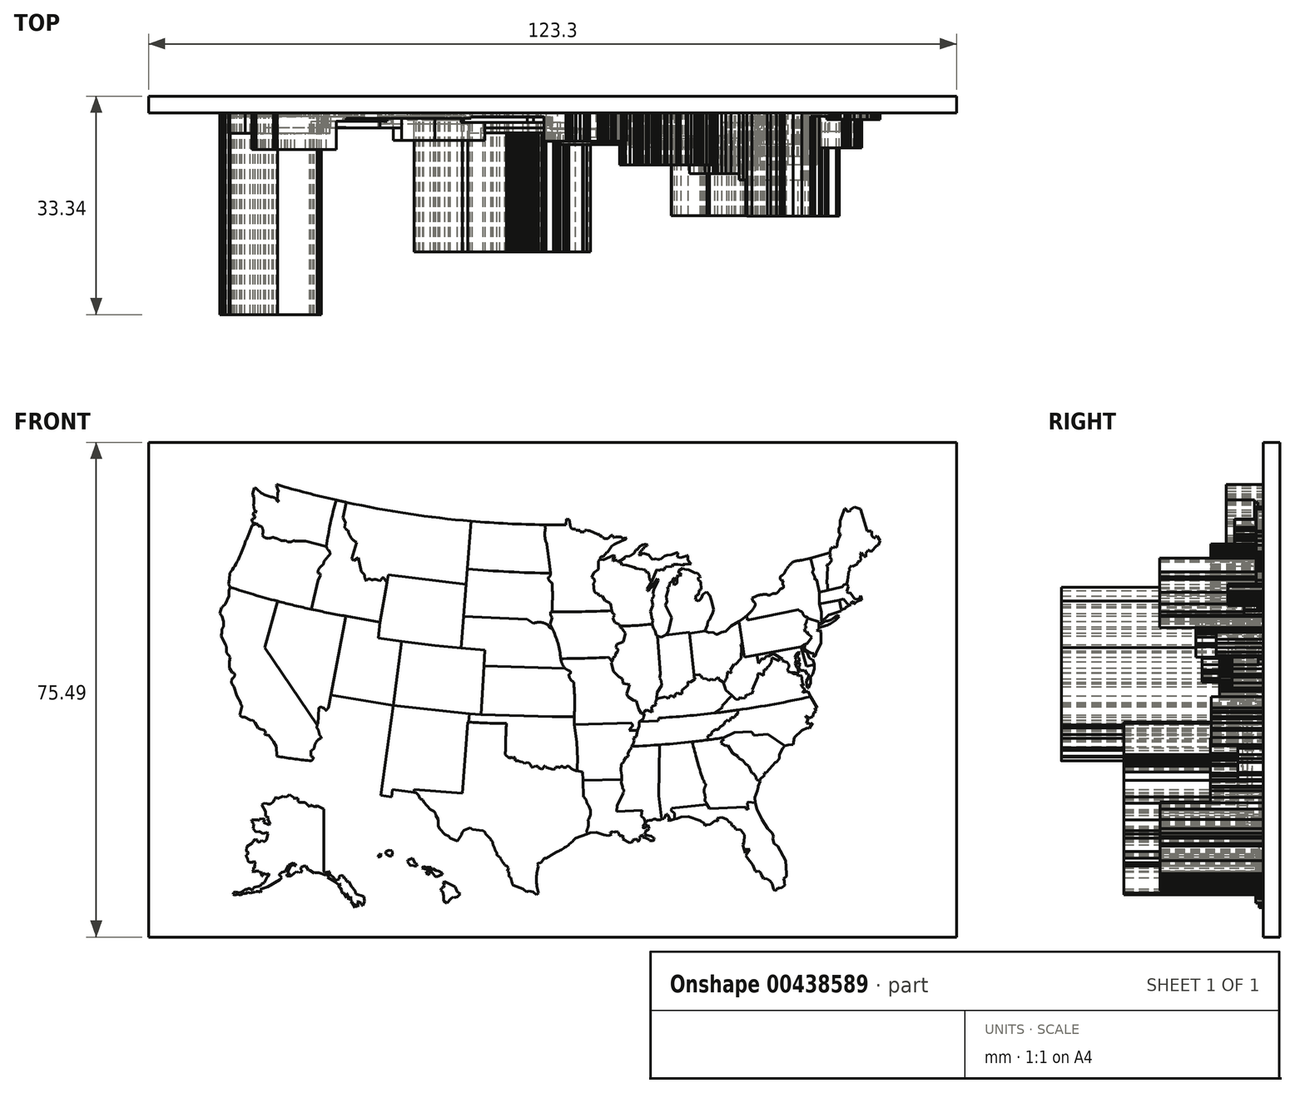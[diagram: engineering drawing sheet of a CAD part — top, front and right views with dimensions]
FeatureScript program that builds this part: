
annotation { "Feature Type Name" : "Feature", "Feature Type Description" : "" }
export const myFeature = defineFeature(function(context is Context, id is Id, definition is map)
    precondition{}
    {
        {
            var Q0;
            Q0=qCreatedBy(makeId("Front.planeOp"),FACE);
            var sketch = newSketch(context, id + "F0", { "sketchPlane" : qUnion([Q0])});
            skLineSegment(sketch, "E0.bottom", {"start": v(-61.56, 41.77) * mm, "end": v(61.74, 41.77) * mm});
            skLineSegment(sketch, "E0.top", {"start": v(-61.56, -33.72) * mm, "end": v(61.74, -33.72) * mm});
            skLineSegment(sketch, "E0.left", {"start": v(-61.56, 41.77) * mm, "end": v(-61.56, -33.72) * mm});
            skLineSegment(sketch, "E0.right", {"start": v(61.74, 41.77) * mm, "end": v(61.74, -33.72) * mm});
            skSolve(sketch);
        }
        {
            var Q0;
            Q0 = qSketchRegion(id + "F0", true);
            extrude(context, id + "F1", {"entities" : qUnion([Q0]), "depth" : 2.54 * mm, "offsetDistance" : 25.4 * mm});
        }
        {
            var Q0;
            Q0=makeQuery(id+"F1.opExtrude","CAP_FACE",FACE,{"disambiguationData":[OSD([sQuery(id+"F0.wireOp",EDGE,"E0.bottom"),sQuery(id+"F0.wireOp",EDGE,"E0.top"),sQuery(id+"F0.wireOp",EDGE,"E0.left"),sQuery(id+"F0.wireOp",EDGE,"E0.right")])],"isStart":false});
            var sketch = newSketch(context, id + "F2", { "sketchPlane" : qUnion([Q0])});
            skLineSegment(sketch, "E1", {"start": v(-6.58, -23.8) * mm, "end": v(-6.79, -23.67) * mm});
            skLineSegment(sketch, "E2", {"start": v(-6.79, -23.67) * mm, "end": v(-6.62, -23.2) * mm});
            skLineSegment(sketch, "E3", {"start": v(-6.86, -22.87) * mm, "end": v(-6.62, -23.2) * mm});
            skLineSegment(sketch, "E4", {"start": v(-6.86, -22.87) * mm, "end": v(-7.18, -22.74) * mm});
            skArc(sketch, "E5", {"start": v(-7.96, -21.52) * mm, "mid": v(-7.6, -22.15) * mm, "end": v(-7.18, -22.74) * mm});
            skArc(sketch, "E6", {"start": v(-8.39, -21.24) * mm, "mid": v(-8.17, -21.38) * mm, "end": v(-7.96, -21.52) * mm});
            skArc(sketch, "E7", {"start": v(-8.39, -20.98) * mm, "mid": v(-8.39, -21.1) * mm, "end": v(-8.39, -21.24) * mm});
            skArc(sketch, "E8", {"start": v(-8.98, -19.66) * mm, "mid": v(-8.7, -20.33) * mm, "end": v(-8.39, -20.98) * mm});
            skArc(sketch, "E9", {"start": v(-9.07, -19.19) * mm, "mid": v(-9.17, -19.07) * mm, "end": v(-9.29, -18.98) * mm});
            skArc(sketch, "E10", {"start": v(-9.07, -19.19) * mm, "mid": v(-9.03, -19.42) * mm, "end": v(-8.98, -19.66) * mm});
            skLineSegment(sketch, "E11", {"start": v(-22.96, 11.38) * mm, "end": v(-24.2, 1.61) * mm});
            skLineSegment(sketch, "E12", {"start": v(-10.22, 10.07) * mm, "end": v(-10.37, 7.64) * mm});
            skLineSegment(sketch, "E13", {"start": v(-31.44, 15.25) * mm, "end": v(-26.22, 14.33) * mm});
            skLineSegment(sketch, "E14", {"start": v(-26.22, 14.33) * mm, "end": v(-26.5, 11.9) * mm});
            skLineSegment(sketch, "E15", {"start": v(-26.5, 11.9) * mm, "end": v(-22.96, 11.38) * mm});
            skLineSegment(sketch, "E16", {"start": v(-33.75, 3.22) * mm, "end": v(-31.44, 15.25) * mm});
            skArc(sketch, "E17", {"start": v(-49.13, 19.66) * mm, "mid": v(-40.36, 17.15) * mm, "end": v(-31.44, 15.25) * mm});
            skLineSegment(sketch, "E18", {"start": v(-43.82, 10.48) * mm, "end": v(-41.9, 17.54) * mm});
            skLineSegment(sketch, "E19", {"start": v(-43.82, 10.48) * mm, "end": v(-35.84, -1.39) * mm});
            skLineSegment(sketch, "E20", {"start": v(-26.22, 14.33) * mm, "end": v(-24.95, 21.56) * mm});
            skLineSegment(sketch, "E21", {"start": v(-13.08, 20.1) * mm, "end": v(-24.95, 21.56) * mm});
            skLineSegment(sketch, "E22", {"start": v(-13.67, -11.77) * mm, "end": v(-12.83, -0.9) * mm});
            skLineSegment(sketch, "E23", {"start": v(-12.83, -0.9) * mm, "end": v(-12.71, -0.9) * mm});
            skLineSegment(sketch, "E24", {"start": v(-12.71, -0.9) * mm, "end": v(-12.62, 0.37) * mm});
            skLineSegment(sketch, "E25", {"start": v(-26.15, -12.1) * mm, "end": v(-24.45, -12.34) * mm});
            skLineSegment(sketch, "E26", {"start": v(-24.45, -12.34) * mm, "end": v(-24.33, -11.2) * mm});
            skLineSegment(sketch, "E27", {"start": v(-24.33, -11.2) * mm, "end": v(-21.02, -11.66) * mm});
            skLineSegment(sketch, "E28", {"start": v(-21.02, -11.66) * mm, "end": v(-21.02, -11.2) * mm});
            skLineSegment(sketch, "E29", {"start": v(-21.02, -11.2) * mm, "end": v(-13.67, -11.77) * mm});
            skLineSegment(sketch, "E30", {"start": v(-37.29, -7.31) * mm, "end": v(-30.35, -11.42) * mm});
            skLineSegment(sketch, "E31", {"start": v(-30.35, -11.42) * mm, "end": v(-26.15, -12.1) * mm});
            skArc(sketch, "E32", {"start": v(-12.71, -0.9) * mm, "mid": v(-9.83, -1.07) * mm, "end": v(-6.95, -1.13) * mm});
            skArc(sketch, "E33", {"start": v(-6.95, -1.13) * mm, "mid": v(-7.05, -3.5) * mm, "end": v(-7.1, -5.86) * mm});
            skArc(sketch, "E34", {"start": v(-41.92, 35.31) * mm, "mid": v(-20.1, 30.62) * mm, "end": v(2.16, 29.2) * mm});
            skLineSegment(sketch, "E35", {"start": v(-13.08, 20.1) * mm, "end": v(-12.32, 29.75) * mm});
            skLineSegment(sketch, "E36", {"start": v(-13.46, 15.24) * mm, "end": v(-3.77, 14.75) * mm});
            skLineSegment(sketch, "E37", {"start": v(-10.37, 7.64) * mm, "end": v(2.04, 7.28) * mm});
            skArc(sketch, "E38", {"start": v(-0.2, 15.89) * mm, "mid": v(4.47, 15.94) * mm, "end": v(9.13, 16.1) * mm});
            skArc(sketch, "E39", {"start": v(1.33, 8.76) * mm, "mid": v(4.97, 8.83) * mm, "end": v(8.6, 8.97) * mm});
            skArc(sketch, "E40", {"start": v(10.38, 13.78) * mm, "mid": v(12.85, 13.82) * mm, "end": v(15.3, 14.07) * mm});
            skLineSegment(sketch, "E41", {"start": v(17.33, 12.38) * mm, "end": v(20.97, 12.8) * mm});
            skLineSegment(sketch, "E42", {"start": v(20.97, 12.8) * mm, "end": v(21.7, 6.25) * mm});
            skLineSegment(sketch, "E43", {"start": v(21, 12.63) * mm, "end": v(23.37, 13) * mm});
            skLineSegment(sketch, "E44", {"start": v(29.76, 15.36) * mm, "end": v(29.82, 14.67) * mm});
            skLineSegment(sketch, "E45", {"start": v(29.82, 14.67) * mm, "end": v(37.59, 16.24) * mm});
            skLineSegment(sketch, "E46", {"start": v(3.4, -0.12) * mm, "end": v(3.4, -1.32) * mm});
            skLineSegment(sketch, "E47", {"start": v(3.4, -1.32) * mm, "end": v(12.08, -1.02) * mm});
            skArc(sketch, "E48", {"start": v(3.4, -0.12) * mm, "mid": v(3.46, 2.54) * mm, "end": v(3.32, 5.2) * mm});
            skArc(sketch, "E49", {"start": v(-32.92, 32.97) * mm, "mid": v(-33.8, 29.44) * mm, "end": v(-34.4, 25.85) * mm});
            skArc(sketch, "E50", {"start": v(16.29, -0.29) * mm, "mid": v(27.94, 0.87) * mm, "end": v(39.47, 2.95) * mm});
            skLineSegment(sketch, "E51", {"start": v(13.29, -0.87) * mm, "end": v(16.25, -0.73) * mm});
            skLineSegment(sketch, "E52", {"start": v(16.25, -0.73) * mm, "end": v(16.29, -0.29) * mm});
            skArc(sketch, "E53", {"start": v(12.12, -4.62) * mm, "mid": v(19.15, -4.15) * mm, "end": v(26.15, -3.3) * mm});
            skLineSegment(sketch, "E54", {"start": v(4.75, -9.79) * mm, "end": v(10.62, -9.67) * mm});
            skLineSegment(sketch, "E55", {"start": v(-35.84, -1.39) * mm, "end": v(-35.69, -1.16) * mm});
            skLineSegment(sketch, "E56", {"start": v(-35.69, -1.16) * mm, "end": v(-35.58, 1.24) * mm});
            skArc(sketch, "E57", {"start": v(-35.22, 1.38) * mm, "mid": v(-35.42, 1.34) * mm, "end": v(-35.58, 1.24) * mm});
            skArc(sketch, "E58", {"start": v(-34.96, 1.24) * mm, "mid": v(-35.08, 1.33) * mm, "end": v(-35.22, 1.38) * mm});
            skArc(sketch, "E59", {"start": v(-34.77, 1.24) * mm, "mid": v(-34.86, 1.24) * mm, "end": v(-34.96, 1.24) * mm});
            skArc(sketch, "E60", {"start": v(-34.1, 1.24) * mm, "mid": v(-34.26, 1.1) * mm, "end": v(-34.37, 0.9) * mm});
            skArc(sketch, "E61", {"start": v(-34.61, 0.92) * mm, "mid": v(-34.67, 1.09) * mm, "end": v(-34.77, 1.24) * mm});
            skArc(sketch, "E62", {"start": v(-34.61, 0.92) * mm, "mid": v(-34.5, 0.9) * mm, "end": v(-34.37, 0.9) * mm});
            skLineSegment(sketch, "E63", {"start": v(-34.1, 1.24) * mm, "end": v(-33.75, 3.22) * mm});
            skArc(sketch, "E64", {"start": v(-42, -6.13) * mm, "mid": v(-39.51, -6.5) * mm, "end": v(-37, -6.82) * mm});
            skArc(sketch, "E65", {"start": v(-37, -6.82) * mm, "mid": v(-37.16, -7.06) * mm, "end": v(-37.29, -7.31) * mm});
            skLineSegment(sketch, "E66", {"start": v(-42.06, -4.67) * mm, "end": v(-42, -6.13) * mm});
            skLineSegment(sketch, "E67", {"start": v(-42.06, -4.67) * mm, "end": v(-42.49, -3.88) * mm});
            skLineSegment(sketch, "E68", {"start": v(-42.49, -3.88) * mm, "end": v(-42.72, -3.66) * mm});
            skLineSegment(sketch, "E69", {"start": v(-42.72, -3.66) * mm, "end": v(-43.18, -2.97) * mm});
            skLineSegment(sketch, "E70", {"start": v(-43.18, -2.97) * mm, "end": v(-43.84, -2.85) * mm});
            skLineSegment(sketch, "E71", {"start": v(-43.84, -2.85) * mm, "end": v(-43.84, -2.72) * mm});
            skLineSegment(sketch, "E72", {"start": v(-43.84, -2.72) * mm, "end": v(-43.74, -2.65) * mm});
            skLineSegment(sketch, "E73", {"start": v(-43.74, -2.65) * mm, "end": v(-43.78, -2.32) * mm});
            skLineSegment(sketch, "E74", {"start": v(-43.78, -2.32) * mm, "end": v(-43.93, -2.1) * mm});
            skLineSegment(sketch, "E75", {"start": v(-43.93, -2.1) * mm, "end": v(-44.47, -2) * mm});
            skLineSegment(sketch, "E76", {"start": v(-44.47, -2) * mm, "end": v(-44.88, -1.78) * mm});
            skLineSegment(sketch, "E77", {"start": v(-44.88, -1.78) * mm, "end": v(-45.3, -1.03) * mm});
            skLineSegment(sketch, "E78", {"start": v(-45.3, -1.03) * mm, "end": v(-45.63, -0.64) * mm});
            skLineSegment(sketch, "E79", {"start": v(-45.63, -0.64) * mm, "end": v(-46.03, -0.6) * mm});
            skLineSegment(sketch, "E80", {"start": v(-46.03, -0.6) * mm, "end": v(-46.9, -0.18) * mm});
            skLineSegment(sketch, "E81", {"start": v(-46.9, -0.18) * mm, "end": v(-47.32, -0.12) * mm});
            skLineSegment(sketch, "E82", {"start": v(-47.32, -0.12) * mm, "end": v(-47.62, 0.17) * mm});
            skLineSegment(sketch, "E83", {"start": v(-47.62, 0.17) * mm, "end": v(-47.32, 1.4) * mm});
            skLineSegment(sketch, "E84", {"start": v(-47.32, 1.4) * mm, "end": v(-47.32, 1.65) * mm});
            skLineSegment(sketch, "E85", {"start": v(-47.32, 1.65) * mm, "end": v(-47.5, 1.8) * mm});
            skLineSegment(sketch, "E86", {"start": v(-47.5, 1.8) * mm, "end": v(-47.5, 2.07) * mm});
            skLineSegment(sketch, "E87", {"start": v(-47.5, 2.07) * mm, "end": v(-48.07, 3.06) * mm});
            skLineSegment(sketch, "E88", {"start": v(-48.07, 3.06) * mm, "end": v(-48.53, 4.45) * mm});
            skLineSegment(sketch, "E89", {"start": v(-48.53, 4.45) * mm, "end": v(-48.84, 4.92) * mm});
            skLineSegment(sketch, "E90", {"start": v(-48.84, 4.92) * mm, "end": v(-48.94, 5.2) * mm});
            skLineSegment(sketch, "E91", {"start": v(-48.94, 5.2) * mm, "end": v(-48.88, 5.7) * mm});
            skArc(sketch, "E92", {"start": v(-48.88, 5.7) * mm, "mid": v(-48.47, 6.05) * mm, "end": v(-48.5, 6.58) * mm});
            skLineSegment(sketch, "E93", {"start": v(-48.5, 6.58) * mm, "end": v(-48.77, 6.64) * mm});
            skLineSegment(sketch, "E94", {"start": v(-48.77, 6.64) * mm, "end": v(-49.26, 7.32) * mm});
            skLineSegment(sketch, "E95", {"start": v(-49.26, 7.32) * mm, "end": v(-49.26, 8.3) * mm});
            skLineSegment(sketch, "E96", {"start": v(-49.26, 8.3) * mm, "end": v(-49.08, 9) * mm});
            skLineSegment(sketch, "E97", {"start": v(-49.08, 9) * mm, "end": v(-49.69, 9.7) * mm});
            skLineSegment(sketch, "E98", {"start": v(-49.69, 9.7) * mm, "end": v(-49.69, 9.96) * mm});
            skArc(sketch, "E99", {"start": v(-49.69, 9.96) * mm, "mid": v(-49.66, 10.43) * mm, "end": v(-49.81, 10.88) * mm});
            skLineSegment(sketch, "E100", {"start": v(-50.52, 12.25) * mm, "end": v(-49.81, 10.88) * mm});
            skLineSegment(sketch, "E101", {"start": v(-50.52, 12.25) * mm, "end": v(-50.4, 12.67) * mm});
            skLineSegment(sketch, "E102", {"start": v(-50.4, 12.67) * mm, "end": v(-50.35, 13.32) * mm});
            skLineSegment(sketch, "E103", {"start": v(-50.35, 13.32) * mm, "end": v(-50.15, 13.64) * mm});
            skLineSegment(sketch, "E104", {"start": v(-50.15, 13.64) * mm, "end": v(-50.12, 14.44) * mm});
            skLineSegment(sketch, "E105", {"start": v(-50.12, 14.44) * mm, "end": v(-50.4, 15.26) * mm});
            skLineSegment(sketch, "E106", {"start": v(-50.4, 15.26) * mm, "end": v(-50.7, 15.68) * mm});
            skLineSegment(sketch, "E107", {"start": v(-50.7, 15.68) * mm, "end": v(-50.46, 16.55) * mm});
            skLineSegment(sketch, "E108", {"start": v(-50.46, 16.55) * mm, "end": v(-50.27, 16.6) * mm});
            skLineSegment(sketch, "E109", {"start": v(-50.27, 16.6) * mm, "end": v(-50.23, 16.77) * mm});
            skLineSegment(sketch, "E110", {"start": v(-50.23, 16.77) * mm, "end": v(-49.9, 17.06) * mm});
            skLineSegment(sketch, "E111", {"start": v(-49.9, 17.06) * mm, "end": v(-49.32, 18.34) * mm});
            skLineSegment(sketch, "E112", {"start": v(-49.32, 18.34) * mm, "end": v(-49.32, 19.18) * mm});
            skLineSegment(sketch, "E113", {"start": v(-49.32, 19.18) * mm, "end": v(-49.13, 19.66) * mm});
            skArc(sketch, "E114", {"start": v(-35.53, -2.8) * mm, "mid": v(-35.62, -2.26) * mm, "end": v(-35.89, -1.79) * mm});
            skLineSegment(sketch, "E115", {"start": v(-35.84, -1.39) * mm, "end": v(-35.89, -1.79) * mm});
            skArc(sketch, "E116", {"start": v(-37, -6.82) * mm, "mid": v(-36.56, -6.69) * mm, "end": v(-36.45, -6.23) * mm});
            skLineSegment(sketch, "E117", {"start": v(-36.45, -6.23) * mm, "end": v(-36.81, -6.15) * mm});
            skLineSegment(sketch, "E118", {"start": v(-36.81, -6.15) * mm, "end": v(-36.77, -5.26) * mm});
            skArc(sketch, "E119", {"start": v(-36.77, -5.26) * mm, "mid": v(-36.48, -5.1) * mm, "end": v(-36.25, -4.85) * mm});
            skArc(sketch, "E120", {"start": v(-35.2, -3.37) * mm, "mid": v(-35.98, -3.93) * mm, "end": v(-36.25, -4.85) * mm});
            skArc(sketch, "E121", {"start": v(-35.2, -3.37) * mm, "mid": v(-35.32, -3.06) * mm, "end": v(-35.53, -2.8) * mm});
            skLineSegment(sketch, "E122", {"start": v(-36.71, 16.3) * mm, "end": v(-35.69, 20.66) * mm});
            skLineSegment(sketch, "E123", {"start": v(-35.69, 20.66) * mm, "end": v(-35.3, 21.49) * mm});
            skLineSegment(sketch, "E124", {"start": v(-35.3, 21.49) * mm, "end": v(-35.42, 21.74) * mm});
            skLineSegment(sketch, "E125", {"start": v(-35.42, 21.74) * mm, "end": v(-35.73, 21.82) * mm});
            skLineSegment(sketch, "E126", {"start": v(-34.4, 25.85) * mm, "end": v(-37.6, 26.7) * mm});
            skLineSegment(sketch, "E127", {"start": v(-37.6, 26.7) * mm, "end": v(-39.29, 26.7) * mm});
            skLineSegment(sketch, "E128", {"start": v(-39.29, 26.7) * mm, "end": v(-39.29, 26.82) * mm});
            skLineSegment(sketch, "E129", {"start": v(-39.29, 26.82) * mm, "end": v(-39.85, 26.6) * mm});
            skLineSegment(sketch, "E130", {"start": v(-39.85, 26.6) * mm, "end": v(-40.34, 26.6) * mm});
            skLineSegment(sketch, "E131", {"start": v(-40.34, 26.6) * mm, "end": v(-40.67, 26.84) * mm});
            skLineSegment(sketch, "E132", {"start": v(-40.67, 26.84) * mm, "end": v(-40.81, 26.76) * mm});
            skLineSegment(sketch, "E133", {"start": v(-40.81, 26.76) * mm, "end": v(-41.31, 26.76) * mm});
            skArc(sketch, "E134", {"start": v(-41.31, 26.76) * mm, "mid": v(-41.96, 27.09) * mm, "end": v(-42.67, 27.29) * mm});
            skArc(sketch, "E135", {"start": v(-44.22, 27.59) * mm, "mid": v(-43.5, 27.14) * mm, "end": v(-42.67, 27.29) * mm});
            skArc(sketch, "E136", {"start": v(-44.22, 27.59) * mm, "mid": v(-44.1, 28.32) * mm, "end": v(-44.4, 29) * mm});
            skLineSegment(sketch, "E137", {"start": v(-44.4, 29) * mm, "end": v(-44.82, 29) * mm});
            skLineSegment(sketch, "E138", {"start": v(-44.82, 29) * mm, "end": v(-44.82, 29.3) * mm});
            skLineSegment(sketch, "E139", {"start": v(-44.82, 29.3) * mm, "end": v(-45.08, 29.3) * mm});
            skLineSegment(sketch, "E140", {"start": v(-45.08, 29.3) * mm, "end": v(-45.37, 29.53) * mm});
            skLineSegment(sketch, "E141", {"start": v(-45.37, 29.53) * mm, "end": v(-45.56, 29.45) * mm});
            skLineSegment(sketch, "E142", {"start": v(-45.56, 29.45) * mm, "end": v(-45.81, 29.75) * mm});
            skLineSegment(sketch, "E143", {"start": v(-45.81, 29.75) * mm, "end": v(-45.78, 30.08) * mm});
            skLineSegment(sketch, "E144", {"start": v(-45.78, 30.08) * mm, "end": v(-45.5, 30.08) * mm});
            skLineSegment(sketch, "E145", {"start": v(-45.5, 30.08) * mm, "end": v(-45.31, 30.55) * mm});
            skLineSegment(sketch, "E146", {"start": v(-45.31, 30.55) * mm, "end": v(-45.58, 30.7) * mm});
            skLineSegment(sketch, "E147", {"start": v(-45.58, 30.7) * mm, "end": v(-45.55, 31.09) * mm});
            skLineSegment(sketch, "E148", {"start": v(-45.55, 31.09) * mm, "end": v(-45.04, 31.14) * mm});
            skLineSegment(sketch, "E149", {"start": v(-45.04, 31.14) * mm, "end": v(-45.4, 31.48) * mm});
            skLineSegment(sketch, "E150", {"start": v(-45.4, 31.48) * mm, "end": v(-45.54, 32.25) * mm});
            skLineSegment(sketch, "E151", {"start": v(-45.54, 32.25) * mm, "end": v(-45.47, 32.5) * mm});
            skLineSegment(sketch, "E152", {"start": v(-45.47, 32.5) * mm, "end": v(-45.47, 33.45) * mm});
            skLineSegment(sketch, "E153", {"start": v(-45.47, 33.45) * mm, "end": v(-45.66, 33.77) * mm});
            skLineSegment(sketch, "E154", {"start": v(-45.66, 33.77) * mm, "end": v(-45.66, 33.96) * mm});
            skLineSegment(sketch, "E155", {"start": v(-45.66, 33.96) * mm, "end": v(-45.45, 34.83) * mm});
            skLineSegment(sketch, "E156", {"start": v(-45.45, 34.83) * mm, "end": v(-45.2, 34.8) * mm});
            skArc(sketch, "E157", {"start": v(-45.2, 34.8) * mm, "mid": v(-43.98, 33.84) * mm, "end": v(-42.5, 33.4) * mm});
            skArc(sketch, "E158", {"start": v(-41.95, 32.72) * mm, "mid": v(-42.12, 33.15) * mm, "end": v(-42.5, 33.4) * mm});
            skArc(sketch, "E159", {"start": v(-41.83, 33.55) * mm, "mid": v(-41.91, 33.21) * mm, "end": v(-41.75, 32.9) * mm});
            skArc(sketch, "E160", {"start": v(-41.71, 34.33) * mm, "mid": v(-41.88, 33.96) * mm, "end": v(-41.83, 33.55) * mm});
            skLineSegment(sketch, "E161", {"start": v(-41.75, 32.9) * mm, "end": v(-41.75, 32.72) * mm});
            skLineSegment(sketch, "E162", {"start": v(-41.75, 32.72) * mm, "end": v(-41.95, 32.72) * mm});
            skLineSegment(sketch, "E163", {"start": v(-41.71, 34.33) * mm, "end": v(-42.05, 35.14) * mm});
            skLineSegment(sketch, "E164", {"start": v(-42.05, 35.14) * mm, "end": v(-42, 35.32) * mm});
            skLineSegment(sketch, "E165", {"start": v(-42, 35.32) * mm, "end": v(-41.92, 35.31) * mm});
            skArc(sketch, "E166", {"start": v(-34.98, 23.04) * mm, "mid": v(-35.52, 22.54) * mm, "end": v(-35.73, 21.82) * mm});
            skArc(sketch, "E167", {"start": v(-34.98, 23.04) * mm, "mid": v(-34.87, 23.25) * mm, "end": v(-34.84, 23.49) * mm});
            skArc(sketch, "E168", {"start": v(-33.85, 24.71) * mm, "mid": v(-34.37, 24.12) * mm, "end": v(-34.84, 23.49) * mm});
            skArc(sketch, "E169", {"start": v(-34.4, 25.85) * mm, "mid": v(-34.24, 25.45) * mm, "end": v(-33.9, 25.17) * mm});
            skLineSegment(sketch, "E170", {"start": v(-33.9, 25.17) * mm, "end": v(-33.85, 24.71) * mm});
            skArc(sketch, "E171", {"start": v(29.76, 15.36) * mm, "mid": v(30.49, 16.06) * mm, "end": v(31.05, 16.9) * mm});
            skArc(sketch, "E172", {"start": v(30.53, 18) * mm, "mid": v(30.63, 17.74) * mm, "end": v(30.73, 17.47) * mm});
            skArc(sketch, "E173", {"start": v(31.05, 16.9) * mm, "mid": v(30.98, 17.24) * mm, "end": v(30.73, 17.47) * mm});
            skArc(sketch, "E174", {"start": v(32.87, 18.54) * mm, "mid": v(31.66, 18.47) * mm, "end": v(30.53, 18) * mm});
            skArc(sketch, "E175", {"start": v(32.87, 18.54) * mm, "mid": v(33.13, 18.43) * mm, "end": v(33.4, 18.54) * mm});
            skArc(sketch, "E176", {"start": v(34.3, 18.7) * mm, "mid": v(33.83, 18.7) * mm, "end": v(33.4, 18.54) * mm});
            skArc(sketch, "E177", {"start": v(34.3, 18.7) * mm, "mid": v(34.63, 19.09) * mm, "end": v(34.94, 19.49) * mm});
            skArc(sketch, "E178", {"start": v(34.94, 19.49) * mm, "mid": v(35.35, 19.65) * mm, "end": v(35.2, 20.07) * mm});
            skArc(sketch, "E179", {"start": v(35.34, 20.66) * mm, "mid": v(35.23, 20.38) * mm, "end": v(35.2, 20.07) * mm});
            skArc(sketch, "E180", {"start": v(35.14, 21.47) * mm, "mid": v(34.83, 20.97) * mm, "end": v(35.34, 20.66) * mm});
            skArc(sketch, "E181", {"start": v(35.14, 21.47) * mm, "mid": v(35.32, 21.65) * mm, "end": v(35.49, 21.84) * mm});
            skArc(sketch, "E182", {"start": v(36.8, 23.54) * mm, "mid": v(36.05, 22.76) * mm, "end": v(35.49, 21.84) * mm});
            skArc(sketch, "E183", {"start": v(37.59, 16.24) * mm, "mid": v(37.87, 16.03) * mm, "end": v(38.21, 15.93) * mm});
            skArc(sketch, "E184", {"start": v(38.21, 15.93) * mm, "mid": v(38.36, 15.5) * mm, "end": v(38.65, 15.13) * mm});
            skArc(sketch, "E185", {"start": v(39.13, 14.92) * mm, "mid": v(38.93, 15.11) * mm, "end": v(38.65, 15.13) * mm});
            skLineSegment(sketch, "E186", {"start": v(39.13, 14.92) * mm, "end": v(40.77, 14.41) * mm});
            skLineSegment(sketch, "E187", {"start": v(40.77, 14.41) * mm, "end": v(40.77, 13.52) * mm});
            skArc(sketch, "E188", {"start": v(40.77, 13.52) * mm, "mid": v(42.45, 14.08) * mm, "end": v(43.84, 15.2) * mm});
            skLineSegment(sketch, "E189", {"start": v(43.84, 15.2) * mm, "end": v(43.42, 15.38) * mm});
            skArc(sketch, "E190", {"start": v(42.11, 14.53) * mm, "mid": v(42.84, 14.85) * mm, "end": v(43.42, 15.38) * mm});
            skArc(sketch, "E191", {"start": v(41.68, 14.53) * mm, "mid": v(41.9, 14.5) * mm, "end": v(42.11, 14.53) * mm});
            skLineSegment(sketch, "E192", {"start": v(41.68, 14.53) * mm, "end": v(41.18, 14.1) * mm});
            skLineSegment(sketch, "E193", {"start": v(41.18, 14.1) * mm, "end": v(40.99, 14.05) * mm});
            skLineSegment(sketch, "E194", {"start": v(40.99, 14.05) * mm, "end": v(40.99, 14.2) * mm});
            skLineSegment(sketch, "E195", {"start": v(40.99, 14.2) * mm, "end": v(41.18, 14.4) * mm});
            skLineSegment(sketch, "E196", {"start": v(41.18, 14.4) * mm, "end": v(41.18, 14.59) * mm});
            skLineSegment(sketch, "E197", {"start": v(41.18, 14.59) * mm, "end": v(40.98, 14.78) * mm});
            skLineSegment(sketch, "E198", {"start": v(40.98, 14.78) * mm, "end": v(41.1, 14.92) * mm});
            skLineSegment(sketch, "E199", {"start": v(41.1, 14.92) * mm, "end": v(41.1, 15.93) * mm});
            skLineSegment(sketch, "E200", {"start": v(41.1, 15.93) * mm, "end": v(40.82, 17.1) * mm});
            skLineSegment(sketch, "E201", {"start": v(40.82, 17.1) * mm, "end": v(40.82, 18.87) * mm});
            skLineSegment(sketch, "E202", {"start": v(40.82, 18.87) * mm, "end": v(40.42, 20.72) * mm});
            skArc(sketch, "E203", {"start": v(40.42, 20.72) * mm, "mid": v(40.27, 20.87) * mm, "end": v(40.08, 20.79) * mm});
            skArc(sketch, "E204", {"start": v(38.13, 23.76) * mm, "mid": v(37.46, 23.7) * mm, "end": v(36.8, 23.54) * mm});
            skLineSegment(sketch, "E205", {"start": v(38.13, 23.76) * mm, "end": v(39.46, 24.13) * mm});
            skLineSegment(sketch, "E206", {"start": v(39.46, 24.13) * mm, "end": v(39.88, 22.6) * mm});
            skArc(sketch, "E207", {"start": v(39.74, 21.98) * mm, "mid": v(39.89, 22.27) * mm, "end": v(39.88, 22.6) * mm});
            skLineSegment(sketch, "E208", {"start": v(39.74, 21.98) * mm, "end": v(40.12, 21.25) * mm});
            skLineSegment(sketch, "E209", {"start": v(40.12, 21.25) * mm, "end": v(40.08, 20.79) * mm});
            skLineSegment(sketch, "E210", {"start": v(-49.13, 19.66) * mm, "end": v(-49.38, 20.16) * mm});
            skLineSegment(sketch, "E211", {"start": v(-49.38, 20.16) * mm, "end": v(-49.22, 20.84) * mm});
            skLineSegment(sketch, "E212", {"start": v(-49.22, 20.84) * mm, "end": v(-49.15, 21.8) * mm});
            skArc(sketch, "E213", {"start": v(-49.15, 21.8) * mm, "mid": v(-47.77, 24.1) * mm, "end": v(-46.8, 26.59) * mm});
            skLineSegment(sketch, "E214", {"start": v(-45.08, 29.3) * mm, "end": v(-45.78, 29.15) * mm});
            skArc(sketch, "E215", {"start": v(-46.8, 26.59) * mm, "mid": v(-46.23, 27.84) * mm, "end": v(-45.78, 29.15) * mm});
            skLineSegment(sketch, "E216", {"start": v(-3.77, 14.75) * mm, "end": v(-2.83, 14.13) * mm});
            skArc(sketch, "E217", {"start": v(-0.54, 13.83) * mm, "mid": v(-1.65, 14.3) * mm, "end": v(-2.83, 14.13) * mm});
            skArc(sketch, "E218", {"start": v(-0.54, 13.83) * mm, "mid": v(-0.35, 13.5) * mm, "end": v(0.01, 13.4) * mm});
            skArc(sketch, "E219", {"start": v(1.33, 8.76) * mm, "mid": v(0.9, 11.14) * mm, "end": v(0.01, 13.4) * mm});
            skArc(sketch, "E220", {"start": v(1.33, 8.76) * mm, "mid": v(1.57, 7.96) * mm, "end": v(2.04, 7.28) * mm});
            skArc(sketch, "E221", {"start": v(2.04, 7.28) * mm, "mid": v(2.37, 7.03) * mm, "end": v(2.76, 6.9) * mm});
            skArc(sketch, "E222", {"start": v(2.6, 6.36) * mm, "mid": v(2.84, 6.58) * mm, "end": v(2.76, 6.9) * mm});
            skArc(sketch, "E223", {"start": v(2.6, 6.36) * mm, "mid": v(2.8, 5.67) * mm, "end": v(3.32, 5.2) * mm});
            skLineSegment(sketch, "E224", {"start": v(-31.41, 32.63) * mm, "end": v(-31.88, 30.28) * mm});
            skLineSegment(sketch, "E225", {"start": v(-31.88, 30.28) * mm, "end": v(-31.53, 29.54) * mm});
            skLineSegment(sketch, "E226", {"start": v(-31.53, 29.54) * mm, "end": v(-31.64, 28.82) * mm});
            skArc(sketch, "E227", {"start": v(-31.64, 28.82) * mm, "mid": v(-31.43, 28.53) * mm, "end": v(-31.12, 28.34) * mm});
            skArc(sketch, "E228", {"start": v(-31.12, 28.34) * mm, "mid": v(-30.7, 27.26) * mm, "end": v(-29.8, 26.51) * mm});
            skLineSegment(sketch, "E229", {"start": v(-30.57, 23.98) * mm, "end": v(-29.8, 26.51) * mm});
            skLineSegment(sketch, "E230", {"start": v(-30.24, 23.7) * mm, "end": v(-30.57, 23.98) * mm});
            skLineSegment(sketch, "E231", {"start": v(-28.57, 21.55) * mm, "end": v(-29.1, 22.08) * mm});
            skLineSegment(sketch, "E232", {"start": v(-29.1, 22.08) * mm, "end": v(-29.53, 24.14) * mm});
            skLineSegment(sketch, "E233", {"start": v(-29.53, 24.14) * mm, "end": v(-30.24, 23.7) * mm});
            skArc(sketch, "E234", {"start": v(-28.57, 21.55) * mm, "mid": v(-28.55, 21.07) * mm, "end": v(-28.35, 20.63) * mm});
            skArc(sketch, "E235", {"start": v(-27.48, 20.74) * mm, "mid": v(-27.95, 20.92) * mm, "end": v(-28.35, 20.63) * mm});
            skArc(sketch, "E236", {"start": v(-26.39, 20.63) * mm, "mid": v(-26.92, 20.86) * mm, "end": v(-27.48, 20.74) * mm});
            skArc(sketch, "E237", {"start": v(-26.39, 20.63) * mm, "mid": v(-26.1, 20.75) * mm, "end": v(-25.98, 21.04) * mm});
            skArc(sketch, "E238", {"start": v(-25.56, 21.03) * mm, "mid": v(-25.41, 20.68) * mm, "end": v(-25.15, 20.41) * mm});
            skArc(sketch, "E239", {"start": v(-25.56, 21.03) * mm, "mid": v(-25.77, 21.1) * mm, "end": v(-25.98, 21.04) * mm});
            skArc(sketch, "E240", {"start": v(3.84, -8.37) * mm, "mid": v(3.84, -4.83) * mm, "end": v(3.4, -1.32) * mm});
            skLineSegment(sketch, "E241", {"start": v(3.84, -8.37) * mm, "end": v(4.68, -8.52) * mm});
            skLineSegment(sketch, "E242", {"start": v(4.68, -8.52) * mm, "end": v(4.75, -9.79) * mm});
            skLineSegment(sketch, "E243", {"start": v(4.75, -9.79) * mm, "end": v(4.8, -12.33) * mm});
            skLineSegment(sketch, "E244", {"start": v(-6.58, -23.8) * mm, "end": v(-6.58, -24.24) * mm});
            skArc(sketch, "E245", {"start": v(-6.58, -24.24) * mm, "mid": v(-6.5, -24.51) * mm, "end": v(-6.25, -24.67) * mm});
            skArc(sketch, "E246", {"start": v(-6.25, -24.67) * mm, "mid": v(-6.14, -25.25) * mm, "end": v(-5.96, -25.81) * mm});
            skLineSegment(sketch, "E247", {"start": v(-2.03, -27) * mm, "end": v(-2.35, -27.24) * mm});
            skLineSegment(sketch, "E248", {"start": v(-2.35, -27.24) * mm, "end": v(-2.88, -26.82) * mm});
            skLineSegment(sketch, "E249", {"start": v(-2.88, -26.82) * mm, "end": v(-3.49, -26.72) * mm});
            skLineSegment(sketch, "E250", {"start": v(-3.49, -26.72) * mm, "end": v(-3.72, -26.79) * mm});
            skLineSegment(sketch, "E251", {"start": v(-3.72, -26.79) * mm, "end": v(-3.92, -26.8) * mm});
            skLineSegment(sketch, "E252", {"start": v(-3.92, -26.8) * mm, "end": v(-4.38, -26.37) * mm});
            skLineSegment(sketch, "E253", {"start": v(-4.38, -26.37) * mm, "end": v(-5.96, -25.81) * mm});
            skLineSegment(sketch, "E254", {"start": v(13.06, -2.2) * mm, "end": v(11.8, -2.2) * mm});
            skArc(sketch, "E255", {"start": v(12.28, -1.61) * mm, "mid": v(12, -1.86) * mm, "end": v(11.8, -2.2) * mm});
            skArc(sketch, "E256", {"start": v(12.28, -1.61) * mm, "mid": v(12.26, -1.29) * mm, "end": v(12.08, -1.02) * mm});
            skLineSegment(sketch, "E257", {"start": v(0.01, 13.4) * mm, "end": v(-0.29, 13.99) * mm});
            skLineSegment(sketch, "E258", {"start": v(-0.29, 13.99) * mm, "end": v(0.01, 15.11) * mm});
            skArc(sketch, "E259", {"start": v(-0.2, 15.89) * mm, "mid": v(-0.2, 15.47) * mm, "end": v(0.01, 15.11) * mm});
            skArc(sketch, "E260", {"start": v(-12.9, 22.47) * mm, "mid": v(-6.57, 22.02) * mm, "end": v(-0.24, 21.8) * mm});
            skArc(sketch, "E261", {"start": v(0.01, 15.89) * mm, "mid": v(0.08, 18.1) * mm, "end": v(0.04, 20.3) * mm});
            skArc(sketch, "E262", {"start": v(-0.58, 21.14) * mm, "mid": v(-0.28, 21.4) * mm, "end": v(-0.24, 21.8) * mm});
            skArc(sketch, "E263", {"start": v(-0.58, 21.14) * mm, "mid": v(-0.37, 20.65) * mm, "end": v(0.04, 20.3) * mm});
            skArc(sketch, "E264", {"start": v(-1.03, 28.4) * mm, "mid": v(-1.02, 28.82) * mm, "end": v(-1.2, 29.2) * mm});
            skArc(sketch, "E265", {"start": v(-1.03, 28.4) * mm, "mid": v(-1.06, 27.27) * mm, "end": v(-0.76, 26.18) * mm});
            skLineSegment(sketch, "E266", {"start": v(-0.76, 26.18) * mm, "end": v(-0.31, 22.92) * mm});
            skLineSegment(sketch, "E267", {"start": v(-0.31, 22.92) * mm, "end": v(-0.24, 21.8) * mm});
            skArc(sketch, "E268", {"start": v(5.3, -13.32) * mm, "mid": v(5.2, -12.75) * mm, "end": v(4.8, -12.33) * mm});
            skArc(sketch, "E269", {"start": v(5.5, -15.85) * mm, "mid": v(5.9, -14.55) * mm, "end": v(5.3, -13.32) * mm});
            skArc(sketch, "E270", {"start": v(5.3, -17.48) * mm, "mid": v(5.56, -16.68) * mm, "end": v(5.5, -15.85) * mm});
            skLineSegment(sketch, "E271", {"start": v(5.3, -17.48) * mm, "end": v(5.4, -17.97) * mm});
            skLineSegment(sketch, "E272", {"start": v(5.4, -17.97) * mm, "end": v(3.57, -18.63) * mm});
            skArc(sketch, "E273", {"start": v(0.84, -20.66) * mm, "mid": v(2.33, -19.81) * mm, "end": v(3.57, -18.63) * mm});
            skArc(sketch, "E274", {"start": v(0.84, -20.66) * mm, "mid": v(-0.02, -21.14) * mm, "end": v(-0.82, -21.71) * mm});
            skArc(sketch, "E275", {"start": v(-2.03, -22.86) * mm, "mid": v(-2.37, -24.93) * mm, "end": v(-2.03, -27) * mm});
            skLineSegment(sketch, "E276", {"start": v(-0.82, -21.71) * mm, "end": v(-1.19, -21.71) * mm});
            skLineSegment(sketch, "E277", {"start": v(-1.19, -21.71) * mm, "end": v(-1.65, -22.39) * mm});
            skLineSegment(sketch, "E278", {"start": v(-1.65, -22.39) * mm, "end": v(-2.1, -22.43) * mm});
            skLineSegment(sketch, "E279", {"start": v(-2.1, -22.43) * mm, "end": v(-2.22, -22.65) * mm});
            skLineSegment(sketch, "E280", {"start": v(-2.22, -22.65) * mm, "end": v(-2.03, -22.86) * mm});
            skLineSegment(sketch, "E281", {"start": v(-9.29, -18.98) * mm, "end": v(-9.29, -18.82) * mm});
            skLineSegment(sketch, "E282", {"start": v(-9.29, -18.82) * mm, "end": v(-10.2, -17.93) * mm});
            skLineSegment(sketch, "E283", {"start": v(-10.2, -17.93) * mm, "end": v(-10.2, -17.76) * mm});
            skLineSegment(sketch, "E284", {"start": v(-10.2, -17.76) * mm, "end": v(-10.52, -17.52) * mm});
            skLineSegment(sketch, "E285", {"start": v(-10.52, -17.52) * mm, "end": v(-12.13, -17.32) * mm});
            skLineSegment(sketch, "E286", {"start": v(-12.13, -17.32) * mm, "end": v(-12.48, -17.04) * mm});
            skLineSegment(sketch, "E287", {"start": v(-12.48, -17.04) * mm, "end": v(-13.4, -17.41) * mm});
            skLineSegment(sketch, "E288", {"start": v(-13.4, -17.41) * mm, "end": v(-13.74, -17.82) * mm});
            skLineSegment(sketch, "E289", {"start": v(-13.74, -17.82) * mm, "end": v(-13.77, -18.12) * mm});
            skLineSegment(sketch, "E290", {"start": v(-13.77, -18.12) * mm, "end": v(-14.47, -19.07) * mm});
            skLineSegment(sketch, "E291", {"start": v(-14.47, -19.07) * mm, "end": v(-15.5, -18.65) * mm});
            skLineSegment(sketch, "E292", {"start": v(-15.5, -18.65) * mm, "end": v(-15.75, -18.3) * mm});
            skLineSegment(sketch, "E293", {"start": v(-15.75, -18.3) * mm, "end": v(-16.33, -18.05) * mm});
            skLineSegment(sketch, "E294", {"start": v(-16.33, -18.05) * mm, "end": v(-17.1, -17.24) * mm});
            skLineSegment(sketch, "E295", {"start": v(-17.1, -17.24) * mm, "end": v(-17.35, -16.8) * mm});
            skLineSegment(sketch, "E296", {"start": v(-17.35, -16.8) * mm, "end": v(-17.37, -15.79) * mm});
            skLineSegment(sketch, "E297", {"start": v(-17.37, -15.79) * mm, "end": v(-17.71, -15.17) * mm});
            skLineSegment(sketch, "E298", {"start": v(-17.71, -15.17) * mm, "end": v(-17.78, -14.79) * mm});
            skLineSegment(sketch, "E299", {"start": v(-17.78, -14.79) * mm, "end": v(-18.07, -14.5) * mm});
            skLineSegment(sketch, "E300", {"start": v(-18.07, -14.5) * mm, "end": v(-18.6, -14.24) * mm});
            skLineSegment(sketch, "E301", {"start": v(-18.6, -14.24) * mm, "end": v(-19.57, -13.1) * mm});
            skLineSegment(sketch, "E302", {"start": v(-19.57, -13.1) * mm, "end": v(-19.7, -12.79) * mm});
            skLineSegment(sketch, "E303", {"start": v(-19.7, -12.79) * mm, "end": v(-20.17, -12.57) * mm});
            skLineSegment(sketch, "E304", {"start": v(-20.17, -12.57) * mm, "end": v(-20.35, -12.1) * mm});
            skLineSegment(sketch, "E305", {"start": v(-20.35, -12.1) * mm, "end": v(-20.72, -11.73) * mm});
            skLineSegment(sketch, "E306", {"start": v(-20.72, -11.73) * mm, "end": v(-21.02, -11.66) * mm});
            skArc(sketch, "E307", {"start": v(21.4, -3.92) * mm, "mid": v(22.16, -6.77) * mm, "end": v(23, -9.6) * mm});
            skLineSegment(sketch, "E308", {"start": v(16.4, -4.38) * mm, "end": v(16.3, -12.15) * mm});
            skLineSegment(sketch, "E309", {"start": v(16.3, -12.15) * mm, "end": v(16.74, -15.71) * mm});
            skLineSegment(sketch, "E310", {"start": v(16.74, -15.71) * mm, "end": v(17.12, -15.67) * mm});
            skLineSegment(sketch, "E311", {"start": v(17.12, -15.67) * mm, "end": v(17.42, -14.93) * mm});
            skLineSegment(sketch, "E312", {"start": v(17.42, -14.93) * mm, "end": v(17.64, -15.03) * mm});
            skLineSegment(sketch, "E313", {"start": v(17.64, -15.03) * mm, "end": v(18, -15.7) * mm});
            skLineSegment(sketch, "E314", {"start": v(18, -15.7) * mm, "end": v(17.67, -15.93) * mm});
            skLineSegment(sketch, "E315", {"start": v(17.67, -15.93) * mm, "end": v(17.92, -15.98) * mm});
            skLineSegment(sketch, "E316", {"start": v(17.92, -15.98) * mm, "end": v(18.7, -15.69) * mm});
            skLineSegment(sketch, "E317", {"start": v(18.7, -15.69) * mm, "end": v(19.12, -15.62) * mm});
            skLineSegment(sketch, "E318", {"start": v(19.12, -15.62) * mm, "end": v(19.74, -15.42) * mm});
            skLineSegment(sketch, "E319", {"start": v(19.74, -15.42) * mm, "end": v(20.83, -15.3) * mm});
            skLineSegment(sketch, "E320", {"start": v(20.83, -15.3) * mm, "end": v(22.65, -15.95) * mm});
            skLineSegment(sketch, "E321", {"start": v(22.65, -15.95) * mm, "end": v(22.84, -16.18) * mm});
            skLineSegment(sketch, "E322", {"start": v(22.84, -16.18) * mm, "end": v(22.97, -16.18) * mm});
            skLineSegment(sketch, "E323", {"start": v(22.97, -16.18) * mm, "end": v(23.2, -16.38) * mm});
            skLineSegment(sketch, "E324", {"start": v(23.2, -16.38) * mm, "end": v(23.32, -16.75) * mm});
            skLineSegment(sketch, "E325", {"start": v(23.32, -16.75) * mm, "end": v(23.59, -16.59) * mm});
            skLineSegment(sketch, "E326", {"start": v(23.59, -16.59) * mm, "end": v(24.18, -16.54) * mm});
            skLineSegment(sketch, "E327", {"start": v(24.18, -16.54) * mm, "end": v(24.9, -15.95) * mm});
            skLineSegment(sketch, "E328", {"start": v(24.9, -15.95) * mm, "end": v(25.29, -16) * mm});
            skLineSegment(sketch, "E329", {"start": v(25.29, -16) * mm, "end": v(25.26, -15.57) * mm});
            skLineSegment(sketch, "E330", {"start": v(25.26, -15.57) * mm, "end": v(25.98, -15.46) * mm});
            skLineSegment(sketch, "E331", {"start": v(25.98, -15.46) * mm, "end": v(26.74, -15.74) * mm});
            skLineSegment(sketch, "E332", {"start": v(26.74, -15.74) * mm, "end": v(27.04, -16.15) * mm});
            skLineSegment(sketch, "E333", {"start": v(27.04, -16.15) * mm, "end": v(27.35, -16.3) * mm});
            skLineSegment(sketch, "E334", {"start": v(27.35, -16.3) * mm, "end": v(27.48, -16.75) * mm});
            skLineSegment(sketch, "E335", {"start": v(27.48, -16.75) * mm, "end": v(27.83, -16.84) * mm});
            skLineSegment(sketch, "E336", {"start": v(27.83, -16.84) * mm, "end": v(28.06, -17.27) * mm});
            skLineSegment(sketch, "E337", {"start": v(28.06, -17.27) * mm, "end": v(28.8, -17.36) * mm});
            skLineSegment(sketch, "E338", {"start": v(24.01, -14.13) * mm, "end": v(29.58, -13.85) * mm});
            skLineSegment(sketch, "E339", {"start": v(18.26, -14.07) * mm, "end": v(23.65, -13.52) * mm});
            skLineSegment(sketch, "E340", {"start": v(23.65, -13.52) * mm, "end": v(24.01, -14.13) * mm});
            skLineSegment(sketch, "E341", {"start": v(18.26, -14.07) * mm, "end": v(18.22, -14.42) * mm});
            skLineSegment(sketch, "E342", {"start": v(18.22, -14.42) * mm, "end": v(18.69, -14.83) * mm});
            skLineSegment(sketch, "E343", {"start": v(18.69, -14.83) * mm, "end": v(18.7, -15.69) * mm});
            skArc(sketch, "E344", {"start": v(23.2, -10.17) * mm, "mid": v(23.18, -9.86) * mm, "end": v(23, -9.6) * mm});
            skArc(sketch, "E345", {"start": v(23.48, -10.56) * mm, "mid": v(23.4, -10.32) * mm, "end": v(23.2, -10.17) * mm});
            skArc(sketch, "E346", {"start": v(23.48, -10.56) * mm, "mid": v(23.23, -11.23) * mm, "end": v(23.33, -11.93) * mm});
            skArc(sketch, "E347", {"start": v(23.33, -12.94) * mm, "mid": v(23.39, -12.44) * mm, "end": v(23.33, -11.93) * mm});
            skArc(sketch, "E348", {"start": v(23.65, -13.52) * mm, "mid": v(23.55, -13.2) * mm, "end": v(23.33, -12.94) * mm});
            skLineSegment(sketch, "E349", {"start": v(13.79, -14.4) * mm, "end": v(9.9, -14.59) * mm});
            skLineSegment(sketch, "E350", {"start": v(9.9, -14.59) * mm, "end": v(9.95, -13.65) * mm});
            skLineSegment(sketch, "E351", {"start": v(9.95, -13.65) * mm, "end": v(10.92, -11.8) * mm});
            skLineSegment(sketch, "E352", {"start": v(13.79, -14.4) * mm, "end": v(13.65, -15.29) * mm});
            skLineSegment(sketch, "E353", {"start": v(13.65, -15.29) * mm, "end": v(14.05, -15.68) * mm});
            skLineSegment(sketch, "E354", {"start": v(14.05, -15.68) * mm, "end": v(14.29, -16.3) * mm});
            skLineSegment(sketch, "E355", {"start": v(14.29, -16.3) * mm, "end": v(14.72, -15.87) * mm});
            skArc(sketch, "E356", {"start": v(14.72, -15.87) * mm, "mid": v(15.01, -15.92) * mm, "end": v(15.3, -15.87) * mm});
            skArc(sketch, "E357", {"start": v(16.05, -15.87) * mm, "mid": v(15.68, -15.72) * mm, "end": v(15.3, -15.87) * mm});
            skLineSegment(sketch, "E358", {"start": v(16.74, -15.71) * mm, "end": v(16.62, -15.84) * mm});
            skLineSegment(sketch, "E359", {"start": v(16.62, -15.84) * mm, "end": v(16.05, -15.87) * mm});
            skArc(sketch, "E360", {"start": v(2.57, -7.66) * mm, "mid": v(3.14, -8.12) * mm, "end": v(3.84, -8.37) * mm});
            skArc(sketch, "E361", {"start": v(2.57, -7.66) * mm, "mid": v(2.33, -7.64) * mm, "end": v(2.17, -7.83) * mm});
            skArc(sketch, "E362", {"start": v(1.75, -7.81) * mm, "mid": v(1.47, -7.67) * mm, "end": v(1.22, -7.87) * mm});
            skLineSegment(sketch, "E363", {"start": v(2.17, -7.83) * mm, "end": v(1.75, -7.81) * mm});
            skLineSegment(sketch, "E364", {"start": v(1.22, -7.87) * mm, "end": v(1.01, -7.77) * mm});
            skLineSegment(sketch, "E365", {"start": v(1.01, -7.77) * mm, "end": v(0.54, -7.78) * mm});
            skLineSegment(sketch, "E366", {"start": v(0.54, -7.78) * mm, "end": v(0.47, -8) * mm});
            skLineSegment(sketch, "E367", {"start": v(0.47, -8) * mm, "end": v(0.22, -8.13) * mm});
            skLineSegment(sketch, "E368", {"start": v(0.22, -8.13) * mm, "end": v(-0.9, -7.81) * mm});
            skLineSegment(sketch, "E369", {"start": v(-0.9, -7.81) * mm, "end": v(-1.04, -7.61) * mm});
            skLineSegment(sketch, "E370", {"start": v(-1.04, -7.61) * mm, "end": v(-1.17, -7.62) * mm});
            skLineSegment(sketch, "E371", {"start": v(-1.17, -7.62) * mm, "end": v(-1.4, -8.05) * mm});
            skLineSegment(sketch, "E372", {"start": v(-1.4, -8.05) * mm, "end": v(-1.55, -8.11) * mm});
            skLineSegment(sketch, "E373", {"start": v(-1.55, -8.11) * mm, "end": v(-2.06, -7.92) * mm});
            skLineSegment(sketch, "E374", {"start": v(-2.06, -7.92) * mm, "end": v(-2.13, -7.67) * mm});
            skLineSegment(sketch, "E375", {"start": v(-2.13, -7.67) * mm, "end": v(-2.49, -7.65) * mm});
            skLineSegment(sketch, "E376", {"start": v(-2.49, -7.65) * mm, "end": v(-2.59, -7.58) * mm});
            skLineSegment(sketch, "E377", {"start": v(-2.59, -7.58) * mm, "end": v(-2.87, -7.84) * mm});
            skLineSegment(sketch, "E378", {"start": v(-2.87, -7.84) * mm, "end": v(-3.13, -7.76) * mm});
            skLineSegment(sketch, "E379", {"start": v(-3.13, -7.76) * mm, "end": v(-3.17, -7.52) * mm});
            skLineSegment(sketch, "E380", {"start": v(-3.17, -7.52) * mm, "end": v(-3.53, -7.12) * mm});
            skLineSegment(sketch, "E381", {"start": v(-3.53, -7.12) * mm, "end": v(-3.9, -7.06) * mm});
            skLineSegment(sketch, "E382", {"start": v(-3.9, -7.06) * mm, "end": v(-4.13, -7.25) * mm});
            skLineSegment(sketch, "E383", {"start": v(-4.13, -7.25) * mm, "end": v(-4.47, -7.01) * mm});
            skLineSegment(sketch, "E384", {"start": v(-4.47, -7.01) * mm, "end": v(-4.87, -6.98) * mm});
            skLineSegment(sketch, "E385", {"start": v(-4.87, -6.98) * mm, "end": v(-5.14, -6.85) * mm});
            skLineSegment(sketch, "E386", {"start": v(-5.14, -6.85) * mm, "end": v(-5.6, -6.82) * mm});
            skLineSegment(sketch, "E387", {"start": v(-5.6, -6.82) * mm, "end": v(-5.6, -6.38) * mm});
            skLineSegment(sketch, "E388", {"start": v(-5.6, -6.38) * mm, "end": v(-5.85, -6.27) * mm});
            skLineSegment(sketch, "E389", {"start": v(-5.85, -6.27) * mm, "end": v(-5.88, -6.4) * mm});
            skLineSegment(sketch, "E390", {"start": v(-5.88, -6.4) * mm, "end": v(-6.06, -6.42) * mm});
            skLineSegment(sketch, "E391", {"start": v(-6.06, -6.42) * mm, "end": v(-6.25, -6.2) * mm});
            skLineSegment(sketch, "E392", {"start": v(-6.25, -6.2) * mm, "end": v(-6.35, -6.4) * mm});
            skLineSegment(sketch, "E393", {"start": v(-6.35, -6.4) * mm, "end": v(-6.48, -6.42) * mm});
            skLineSegment(sketch, "E394", {"start": v(-6.48, -6.42) * mm, "end": v(-7.1, -5.86) * mm});
            skLineSegment(sketch, "E395", {"start": v(5.4, -17.97) * mm, "end": v(5.84, -17.82) * mm});
            skLineSegment(sketch, "E396", {"start": v(5.84, -17.82) * mm, "end": v(6.78, -17.76) * mm});
            skLineSegment(sketch, "E397", {"start": v(6.78, -17.76) * mm, "end": v(7.93, -18.15) * mm});
            skLineSegment(sketch, "E398", {"start": v(7.93, -18.15) * mm, "end": v(8.61, -18.27) * mm});
            skLineSegment(sketch, "E399", {"start": v(8.61, -18.27) * mm, "end": v(9.13, -18.04) * mm});
            skLineSegment(sketch, "E400", {"start": v(9.13, -18.04) * mm, "end": v(8.9, -17.9) * mm});
            skLineSegment(sketch, "E401", {"start": v(8.9, -17.9) * mm, "end": v(8.96, -17.72) * mm});
            skLineSegment(sketch, "E402", {"start": v(8.96, -17.72) * mm, "end": v(9.3, -17.6) * mm});
            skLineSegment(sketch, "E403", {"start": v(9.3, -17.6) * mm, "end": v(9.5, -17.75) * mm});
            skLineSegment(sketch, "E404", {"start": v(9.5, -17.75) * mm, "end": v(9.73, -17.63) * mm});
            skLineSegment(sketch, "E405", {"start": v(9.73, -17.63) * mm, "end": v(10.06, -17.7) * mm});
            skLineSegment(sketch, "E406", {"start": v(10.06, -17.7) * mm, "end": v(10.26, -18.04) * mm});
            skLineSegment(sketch, "E407", {"start": v(10.26, -18.04) * mm, "end": v(10.26, -18.26) * mm});
            skLineSegment(sketch, "E408", {"start": v(10.26, -18.26) * mm, "end": v(10.76, -18.27) * mm});
            skLineSegment(sketch, "E409", {"start": v(10.76, -18.27) * mm, "end": v(10.97, -18.44) * mm});
            skLineSegment(sketch, "E410", {"start": v(10.97, -18.44) * mm, "end": v(10.78, -18.74) * mm});
            skLineSegment(sketch, "E411", {"start": v(10.78, -18.74) * mm, "end": v(11.84, -19.33) * mm});
            skLineSegment(sketch, "E412", {"start": v(11.84, -19.33) * mm, "end": v(12.27, -19.17) * mm});
            skLineSegment(sketch, "E413", {"start": v(12.27, -19.17) * mm, "end": v(12.34, -18.9) * mm});
            skLineSegment(sketch, "E414", {"start": v(12.34, -18.9) * mm, "end": v(12.65, -18.85) * mm});
            skLineSegment(sketch, "E415", {"start": v(12.65, -18.85) * mm, "end": v(12.8, -18.67) * mm});
            skLineSegment(sketch, "E416", {"start": v(12.8, -18.67) * mm, "end": v(13, -18.8) * mm});
            skLineSegment(sketch, "E417", {"start": v(13, -18.8) * mm, "end": v(13.07, -19.1) * mm});
            skLineSegment(sketch, "E418", {"start": v(13.07, -19.1) * mm, "end": v(13.19, -19.16) * mm});
            skLineSegment(sketch, "E419", {"start": v(13.19, -19.16) * mm, "end": v(13.47, -18.77) * mm});
            skLineSegment(sketch, "E420", {"start": v(13.47, -18.77) * mm, "end": v(13.47, -18.7) * mm});
            skLineSegment(sketch, "E421", {"start": v(13.47, -18.7) * mm, "end": v(13.34, -18.66) * mm});
            skLineSegment(sketch, "E422", {"start": v(13.34, -18.66) * mm, "end": v(13.41, -18.54) * mm});
            skLineSegment(sketch, "E423", {"start": v(13.41, -18.54) * mm, "end": v(13.44, -18.3) * mm});
            skLineSegment(sketch, "E424", {"start": v(13.44, -18.3) * mm, "end": v(13.65, -18.27) * mm});
            skLineSegment(sketch, "E425", {"start": v(13.65, -18.27) * mm, "end": v(13.79, -18.11) * mm});
            skLineSegment(sketch, "E426", {"start": v(13.79, -18.11) * mm, "end": v(13.89, -18.2) * mm});
            skLineSegment(sketch, "E427", {"start": v(13.89, -18.2) * mm, "end": v(13.86, -18.5) * mm});
            skLineSegment(sketch, "E428", {"start": v(13.86, -18.5) * mm, "end": v(14.22, -18.57) * mm});
            skLineSegment(sketch, "E429", {"start": v(14.22, -18.57) * mm, "end": v(14.83, -18.85) * mm});
            skLineSegment(sketch, "E430", {"start": v(14.83, -18.85) * mm, "end": v(14.92, -18.99) * mm});
            skLineSegment(sketch, "E431", {"start": v(14.92, -18.99) * mm, "end": v(15.26, -19) * mm});
            skLineSegment(sketch, "E432", {"start": v(15.26, -19) * mm, "end": v(15.38, -19.09) * mm});
            skLineSegment(sketch, "E433", {"start": v(15.38, -19.09) * mm, "end": v(15.64, -18.77) * mm});
            skLineSegment(sketch, "E434", {"start": v(15.64, -18.77) * mm, "end": v(15.63, -18.63) * mm});
            skLineSegment(sketch, "E435", {"start": v(15.63, -18.63) * mm, "end": v(15.48, -18.6) * mm});
            skLineSegment(sketch, "E436", {"start": v(15.48, -18.6) * mm, "end": v(15.13, -18.3) * mm});
            skLineSegment(sketch, "E437", {"start": v(15.13, -18.3) * mm, "end": v(14.45, -18.18) * mm});
            skLineSegment(sketch, "E438", {"start": v(14.45, -18.18) * mm, "end": v(14.13, -17.98) * mm});
            skLineSegment(sketch, "E439", {"start": v(14.13, -17.98) * mm, "end": v(14.36, -17.6) * mm});
            skLineSegment(sketch, "E440", {"start": v(14.36, -17.6) * mm, "end": v(14.32, -17.45) * mm});
            skLineSegment(sketch, "E441", {"start": v(14.32, -17.45) * mm, "end": v(14.66, -17.45) * mm});
            skLineSegment(sketch, "E442", {"start": v(14.66, -17.45) * mm, "end": v(14.85, -17.17) * mm});
            skLineSegment(sketch, "E443", {"start": v(14.85, -17.17) * mm, "end": v(14.68, -16.63) * mm});
            skLineSegment(sketch, "E444", {"start": v(14.68, -16.63) * mm, "end": v(14.34, -16.79) * mm});
            skLineSegment(sketch, "E445", {"start": v(14.34, -16.79) * mm, "end": v(14.3, -17.13) * mm});
            skLineSegment(sketch, "E446", {"start": v(14.3, -17.13) * mm, "end": v(13.94, -17.07) * mm});
            skLineSegment(sketch, "E447", {"start": v(13.94, -17.07) * mm, "end": v(13.83, -16.86) * mm});
            skLineSegment(sketch, "E448", {"start": v(13.83, -16.86) * mm, "end": v(14.29, -16.3) * mm});
            skLineSegment(sketch, "E449", {"start": v(10.92, -11.8) * mm, "end": v(10.83, -11.56) * mm});
            skLineSegment(sketch, "E450", {"start": v(10.83, -11.56) * mm, "end": v(10.99, -11.53) * mm});
            skLineSegment(sketch, "E451", {"start": v(10.99, -11.53) * mm, "end": v(10.97, -11.22) * mm});
            skLineSegment(sketch, "E452", {"start": v(10.97, -11.22) * mm, "end": v(10.79, -11.05) * mm});
            skLineSegment(sketch, "E453", {"start": v(10.79, -11.05) * mm, "end": v(10.78, -10.74) * mm});
            skLineSegment(sketch, "E454", {"start": v(10.78, -10.74) * mm, "end": v(10.57, -10.21) * mm});
            skLineSegment(sketch, "E455", {"start": v(10.57, -10.21) * mm, "end": v(10.62, -9.67) * mm});
            skLineSegment(sketch, "E456", {"start": v(10.62, -9.67) * mm, "end": v(10.67, -9.04) * mm});
            skLineSegment(sketch, "E457", {"start": v(10.67, -9.04) * mm, "end": v(10.51, -8.26) * mm});
            skLineSegment(sketch, "E458", {"start": v(10.51, -8.26) * mm, "end": v(10.59, -7.34) * mm});
            skLineSegment(sketch, "E459", {"start": v(10.59, -7.34) * mm, "end": v(11, -7.03) * mm});
            skLineSegment(sketch, "E460", {"start": v(11, -7.03) * mm, "end": v(10.94, -6.83) * mm});
            skLineSegment(sketch, "E461", {"start": v(10.94, -6.83) * mm, "end": v(11.28, -6.28) * mm});
            skLineSegment(sketch, "E462", {"start": v(11.28, -6.28) * mm, "end": v(11.66, -6.15) * mm});
            skLineSegment(sketch, "E463", {"start": v(11.66, -6.15) * mm, "end": v(11.59, -5.66) * mm});
            skLineSegment(sketch, "E464", {"start": v(11.59, -5.66) * mm, "end": v(11.9, -5.08) * mm});
            skLineSegment(sketch, "E465", {"start": v(11.9, -5.08) * mm, "end": v(12.06, -5) * mm});
            skLineSegment(sketch, "E466", {"start": v(12.06, -5) * mm, "end": v(12.18, -4.83) * mm});
            skLineSegment(sketch, "E467", {"start": v(12.18, -4.83) * mm, "end": v(12.12, -4.62) * mm});
            skLineSegment(sketch, "E468", {"start": v(12.12, -4.62) * mm, "end": v(12.45, -4.23) * mm});
            skLineSegment(sketch, "E469", {"start": v(12.45, -4.23) * mm, "end": v(12.56, -3.73) * mm});
            skLineSegment(sketch, "E470", {"start": v(12.56, -3.73) * mm, "end": v(12.43, -3.35) * mm});
            skLineSegment(sketch, "E471", {"start": v(12.43, -3.35) * mm, "end": v(12.88, -3.15) * mm});
            skLineSegment(sketch, "E472", {"start": v(12.88, -3.15) * mm, "end": v(13.06, -2.2) * mm});
            skLineSegment(sketch, "E473", {"start": v(13.29, -0.87) * mm, "end": v(13.29, -1.54) * mm});
            skLineSegment(sketch, "E474", {"start": v(13.29, -1.54) * mm, "end": v(13.06, -2.2) * mm});
            skLineSegment(sketch, "E475", {"start": v(13.29, -0.87) * mm, "end": v(13.96, -0.41) * mm});
            skLineSegment(sketch, "E476", {"start": v(13.96, -0.41) * mm, "end": v(14, -0.01) * mm});
            skLineSegment(sketch, "E477", {"start": v(14, -0.01) * mm, "end": v(14.08, 0.17) * mm});
            skLineSegment(sketch, "E478", {"start": v(14.08, 0.17) * mm, "end": v(14.07, 0.33) * mm});
            skLineSegment(sketch, "E479", {"start": v(14.07, 0.33) * mm, "end": v(13.9, 0.38) * mm});
            skLineSegment(sketch, "E480", {"start": v(13.9, 0.38) * mm, "end": v(13.61, 0.4) * mm});
            skLineSegment(sketch, "E481", {"start": v(13.61, 0.4) * mm, "end": v(13.22, 1.04) * mm});
            skLineSegment(sketch, "E482", {"start": v(13.22, 1.04) * mm, "end": v(12.9, 2.32) * mm});
            skLineSegment(sketch, "E483", {"start": v(12.9, 2.32) * mm, "end": v(12.49, 2.36) * mm});
            skLineSegment(sketch, "E484", {"start": v(12.49, 2.36) * mm, "end": v(11.62, 2.99) * mm});
            skLineSegment(sketch, "E485", {"start": v(11.62, 2.99) * mm, "end": v(11.43, 3.39) * mm});
            skLineSegment(sketch, "E486", {"start": v(11.43, 3.39) * mm, "end": v(11.68, 4.17) * mm});
            skLineSegment(sketch, "E487", {"start": v(11.68, 4.17) * mm, "end": v(11.83, 4.78) * mm});
            skLineSegment(sketch, "E488", {"start": v(11.83, 4.78) * mm, "end": v(10.82, 5.01) * mm});
            skLineSegment(sketch, "E489", {"start": v(10.82, 5.01) * mm, "end": v(10.78, 5.68) * mm});
            skLineSegment(sketch, "E490", {"start": v(10.78, 5.68) * mm, "end": v(10.19, 6.02) * mm});
            skLineSegment(sketch, "E491", {"start": v(10.19, 6.02) * mm, "end": v(9.38, 6.84) * mm});
            skLineSegment(sketch, "E492", {"start": v(9.38, 6.84) * mm, "end": v(9.07, 8.17) * mm});
            skLineSegment(sketch, "E493", {"start": v(9.07, 8.17) * mm, "end": v(9.16, 8.38) * mm});
            skLineSegment(sketch, "E494", {"start": v(9.16, 8.38) * mm, "end": v(9.32, 8.57) * mm});
            skLineSegment(sketch, "E495", {"start": v(9.32, 8.57) * mm, "end": v(9.3, 8.94) * mm});
            skLineSegment(sketch, "E496", {"start": v(9.3, 8.94) * mm, "end": v(9.7, 9.14) * mm});
            skLineSegment(sketch, "E497", {"start": v(8.6, 8.97) * mm, "end": v(9.16, 8.38) * mm});
            skLineSegment(sketch, "E498", {"start": v(9.7, 9.14) * mm, "end": v(9.7, 9.56) * mm});
            skLineSegment(sketch, "E499", {"start": v(9.7, 9.56) * mm, "end": v(9.98, 9.73) * mm});
            skLineSegment(sketch, "E500", {"start": v(9.98, 9.73) * mm, "end": v(10.05, 10.21) * mm});
            skLineSegment(sketch, "E501", {"start": v(10.05, 10.21) * mm, "end": v(9.73, 10.47) * mm});
            skLineSegment(sketch, "E502", {"start": v(9.73, 10.47) * mm, "end": v(9.86, 10.95) * mm});
            skLineSegment(sketch, "E503", {"start": v(9.86, 10.95) * mm, "end": v(10.91, 11.37) * mm});
            skLineSegment(sketch, "E504", {"start": v(10.91, 11.37) * mm, "end": v(11.25, 12.66) * mm});
            skLineSegment(sketch, "E505", {"start": v(11.25, 12.66) * mm, "end": v(10.78, 13.17) * mm});
            skLineSegment(sketch, "E506", {"start": v(10.78, 13.17) * mm, "end": v(10.76, 13.35) * mm});
            skLineSegment(sketch, "E507", {"start": v(10.76, 13.35) * mm, "end": v(10.37, 13.57) * mm});
            skLineSegment(sketch, "E508", {"start": v(10.37, 13.57) * mm, "end": v(10.38, 13.78) * mm});
            skLineSegment(sketch, "E509", {"start": v(10.23, 14.01) * mm, "end": v(9.62, 14.23) * mm});
            skLineSegment(sketch, "E510", {"start": v(10.23, 14.01) * mm, "end": v(10.38, 13.78) * mm});
            skLineSegment(sketch, "E511", {"start": v(9.62, 14.23) * mm, "end": v(9.36, 14.68) * mm});
            skLineSegment(sketch, "E512", {"start": v(9.36, 14.68) * mm, "end": v(9.34, 15.02) * mm});
            skLineSegment(sketch, "E513", {"start": v(9.34, 15.02) * mm, "end": v(9.54, 15.38) * mm});
            skLineSegment(sketch, "E514", {"start": v(9.54, 15.38) * mm, "end": v(9.53, 15.54) * mm});
            skLineSegment(sketch, "E515", {"start": v(9.53, 15.54) * mm, "end": v(9.27, 15.73) * mm});
            skLineSegment(sketch, "E516", {"start": v(9.27, 15.73) * mm, "end": v(9.13, 16.1) * mm});
            skLineSegment(sketch, "E517", {"start": v(16.58, 6.46) * mm, "end": v(16.1, 12.23) * mm});
            skLineSegment(sketch, "E518", {"start": v(16.1, 12.23) * mm, "end": v(16.68, 12.04) * mm});
            skLineSegment(sketch, "E519", {"start": v(16.68, 12.04) * mm, "end": v(17.33, 12.38) * mm});
            skLineSegment(sketch, "E520", {"start": v(15.3, 14.07) * mm, "end": v(15.45, 13.44) * mm});
            skLineSegment(sketch, "E521", {"start": v(15.45, 13.44) * mm, "end": v(15.74, 13.03) * mm});
            skLineSegment(sketch, "E522", {"start": v(15.74, 13.03) * mm, "end": v(15.95, 12.33) * mm});
            skLineSegment(sketch, "E523", {"start": v(15.95, 12.33) * mm, "end": v(16.1, 12.23) * mm});
            skLineSegment(sketch, "E524", {"start": v(2.16, 29.2) * mm, "end": v(2.23, 30.1) * mm});
            skLineSegment(sketch, "E525", {"start": v(2.23, 30.1) * mm, "end": v(2.62, 30.02) * mm});
            skLineSegment(sketch, "E526", {"start": v(2.62, 30.02) * mm, "end": v(2.86, 28.78) * mm});
            skLineSegment(sketch, "E527", {"start": v(2.86, 28.78) * mm, "end": v(3.1, 28.52) * mm});
            skLineSegment(sketch, "E528", {"start": v(3.1, 28.52) * mm, "end": v(3.63, 28.53) * mm});
            skLineSegment(sketch, "E529", {"start": v(3.63, 28.53) * mm, "end": v(3.64, 28.38) * mm});
            skLineSegment(sketch, "E530", {"start": v(3.64, 28.38) * mm, "end": v(4.32, 28.33) * mm});
            skLineSegment(sketch, "E531", {"start": v(4.32, 28.33) * mm, "end": v(4.3, 28.08) * mm});
            skLineSegment(sketch, "E532", {"start": v(4.3, 28.08) * mm, "end": v(4.95, 28.1) * mm});
            skLineSegment(sketch, "E533", {"start": v(4.95, 28.1) * mm, "end": v(5.08, 28.34) * mm});
            skLineSegment(sketch, "E534", {"start": v(5.08, 28.34) * mm, "end": v(5.3, 28.43) * mm});
            skLineSegment(sketch, "E535", {"start": v(5.3, 28.43) * mm, "end": v(5.47, 28.32) * mm});
            skLineSegment(sketch, "E536", {"start": v(5.47, 28.32) * mm, "end": v(5.77, 28.32) * mm});
            skLineSegment(sketch, "E537", {"start": v(5.77, 28.32) * mm, "end": v(7.03, 27.7) * mm});
            skLineSegment(sketch, "E538", {"start": v(7.03, 27.7) * mm, "end": v(7.26, 27.75) * mm});
            skLineSegment(sketch, "E539", {"start": v(7.26, 27.75) * mm, "end": v(7.29, 27.58) * mm});
            skLineSegment(sketch, "E540", {"start": v(7.29, 27.58) * mm, "end": v(7.6, 27.43) * mm});
            skLineSegment(sketch, "E541", {"start": v(7.6, 27.43) * mm, "end": v(7.74, 27.42) * mm});
            skLineSegment(sketch, "E542", {"start": v(7.74, 27.42) * mm, "end": v(7.78, 27.23) * mm});
            skLineSegment(sketch, "E543", {"start": v(7.78, 27.23) * mm, "end": v(8.07, 27.1) * mm});
            skLineSegment(sketch, "E544", {"start": v(8.07, 27.1) * mm, "end": v(8.32, 27.07) * mm});
            skLineSegment(sketch, "E545", {"start": v(8.32, 27.07) * mm, "end": v(8.53, 27.11) * mm});
            skLineSegment(sketch, "E546", {"start": v(8.53, 27.11) * mm, "end": v(9.05, 27.57) * mm});
            skLineSegment(sketch, "E547", {"start": v(9.05, 27.57) * mm, "end": v(9.25, 27.58) * mm});
            skLineSegment(sketch, "E548", {"start": v(9.25, 27.58) * mm, "end": v(9.35, 27.3) * mm});
            skLineSegment(sketch, "E549", {"start": v(9.35, 27.3) * mm, "end": v(9.52, 27.23) * mm});
            skLineSegment(sketch, "E550", {"start": v(9.52, 27.23) * mm, "end": v(9.66, 27.35) * mm});
            skLineSegment(sketch, "E551", {"start": v(9.66, 27.35) * mm, "end": v(10.56, 27.36) * mm});
            skLineSegment(sketch, "E552", {"start": v(10.56, 27.36) * mm, "end": v(10.76, 27.07) * mm});
            skLineSegment(sketch, "E553", {"start": v(10.76, 27.07) * mm, "end": v(10.93, 27.06) * mm});
            skLineSegment(sketch, "E554", {"start": v(10.93, 27.06) * mm, "end": v(11.02, 27.15) * mm});
            skLineSegment(sketch, "E555", {"start": v(11.02, 27.15) * mm, "end": v(11.42, 27.19) * mm});
            skLineSegment(sketch, "E556", {"start": v(11.42, 27.19) * mm, "end": v(11.2, 26.95) * mm});
            skLineSegment(sketch, "E557", {"start": v(11.2, 26.95) * mm, "end": v(10.74, 26.77) * mm});
            skLineSegment(sketch, "E558", {"start": v(10.74, 26.77) * mm, "end": v(9.5, 26.2) * mm});
            skLineSegment(sketch, "E559", {"start": v(9.5, 26.2) * mm, "end": v(9.13, 25.94) * mm});
            skLineSegment(sketch, "E560", {"start": v(9.13, 25.94) * mm, "end": v(8.9, 25.6) * mm});
            skLineSegment(sketch, "E561", {"start": v(8.9, 25.6) * mm, "end": v(8.52, 25) * mm});
            skLineSegment(sketch, "E562", {"start": v(8.52, 25) * mm, "end": v(8.36, 24.97) * mm});
            skLineSegment(sketch, "E563", {"start": v(8.36, 24.97) * mm, "end": v(7.86, 24.36) * mm});
            skLineSegment(sketch, "E564", {"start": v(7.86, 24.36) * mm, "end": v(7.54, 24.37) * mm});
            skLineSegment(sketch, "E565", {"start": v(7.54, 24.37) * mm, "end": v(7.28, 24.06) * mm});
            skLineSegment(sketch, "E566", {"start": v(7.28, 24.06) * mm, "end": v(7.37, 23.92) * mm});
            skLineSegment(sketch, "E567", {"start": v(7.37, 23.92) * mm, "end": v(7.82, 23.88) * mm});
            skLineSegment(sketch, "E568", {"start": v(7.82, 23.88) * mm, "end": v(9.42, 24.57) * mm});
            skLineSegment(sketch, "E569", {"start": v(9.42, 24.57) * mm, "end": v(9.64, 24.4) * mm});
            skLineSegment(sketch, "E570", {"start": v(9.64, 24.4) * mm, "end": v(9.28, 23.82) * mm});
            skLineSegment(sketch, "E571", {"start": v(9.28, 23.82) * mm, "end": v(9.32, 23.63) * mm});
            skLineSegment(sketch, "E572", {"start": v(9.32, 23.63) * mm, "end": v(9.59, 23.77) * mm});
            skLineSegment(sketch, "E573", {"start": v(9.59, 23.77) * mm, "end": v(9.92, 23.77) * mm});
            skLineSegment(sketch, "E574", {"start": v(9.92, 23.77) * mm, "end": v(10.05, 23.54) * mm});
            skLineSegment(sketch, "E575", {"start": v(10.05, 23.54) * mm, "end": v(10.13, 23.54) * mm});
            skLineSegment(sketch, "E576", {"start": v(10.13, 23.54) * mm, "end": v(10.3, 23.74) * mm});
            skLineSegment(sketch, "E577", {"start": v(10.3, 23.74) * mm, "end": v(10.65, 23.88) * mm});
            skLineSegment(sketch, "E578", {"start": v(10.65, 23.88) * mm, "end": v(11.13, 24.16) * mm});
            skLineSegment(sketch, "E579", {"start": v(11.13, 24.16) * mm, "end": v(11.11, 24.24) * mm});
            skLineSegment(sketch, "E580", {"start": v(11.11, 24.24) * mm, "end": v(11.2, 24.36) * mm});
            skLineSegment(sketch, "E581", {"start": v(11.2, 24.36) * mm, "end": v(11.91, 24.45) * mm});
            skLineSegment(sketch, "E582", {"start": v(11.91, 24.45) * mm, "end": v(12.56, 24.87) * mm});
            skLineSegment(sketch, "E583", {"start": v(12.56, 24.87) * mm, "end": v(12.83, 25.37) * mm});
            skLineSegment(sketch, "E584", {"start": v(12.83, 25.37) * mm, "end": v(13.03, 25.42) * mm});
            skLineSegment(sketch, "E585", {"start": v(13.03, 25.42) * mm, "end": v(13.4, 25.9) * mm});
            skLineSegment(sketch, "E586", {"start": v(13.4, 25.9) * mm, "end": v(13.83, 26.16) * mm});
            skLineSegment(sketch, "E587", {"start": v(13.83, 26.16) * mm, "end": v(14.37, 26.23) * mm});
            skLineSegment(sketch, "E588", {"start": v(14.37, 26.23) * mm, "end": v(14.56, 26.12) * mm});
            skLineSegment(sketch, "E589", {"start": v(14.56, 26.12) * mm, "end": v(14.52, 25.98) * mm});
            skLineSegment(sketch, "E590", {"start": v(14.52, 25.98) * mm, "end": v(14.13, 25.9) * mm});
            skLineSegment(sketch, "E591", {"start": v(14.13, 25.9) * mm, "end": v(13.93, 25.53) * mm});
            skLineSegment(sketch, "E592", {"start": v(13.93, 25.53) * mm, "end": v(13.69, 25.4) * mm});
            skLineSegment(sketch, "E593", {"start": v(13.69, 25.4) * mm, "end": v(13.65, 25.23) * mm});
            skLineSegment(sketch, "E594", {"start": v(13.65, 25.23) * mm, "end": v(13.33, 24.78) * mm});
            skLineSegment(sketch, "E595", {"start": v(13.33, 24.78) * mm, "end": v(13.37, 24.52) * mm});
            skLineSegment(sketch, "E596", {"start": v(13.37, 24.52) * mm, "end": v(13.43, 24.46) * mm});
            skLineSegment(sketch, "E597", {"start": v(13.43, 24.46) * mm, "end": v(13.93, 24.93) * mm});
            skLineSegment(sketch, "E598", {"start": v(13.93, 24.93) * mm, "end": v(14.07, 24.78) * mm});
            skLineSegment(sketch, "E599", {"start": v(14.07, 24.78) * mm, "end": v(14.8, 24.6) * mm});
            skLineSegment(sketch, "E600", {"start": v(14.8, 24.6) * mm, "end": v(15.26, 23.94) * mm});
            skLineSegment(sketch, "E601", {"start": v(15.26, 23.94) * mm, "end": v(15.75, 23.95) * mm});
            skLineSegment(sketch, "E602", {"start": v(29.76, 15.36) * mm, "end": v(29.21, 14.87) * mm});
            skLineSegment(sketch, "E603", {"start": v(29.21, 14.87) * mm, "end": v(28.57, 14.43) * mm});
            skLineSegment(sketch, "E604", {"start": v(28.57, 14.43) * mm, "end": v(29.41, 8.98) * mm});
            skLineSegment(sketch, "E605", {"start": v(29.41, 8.98) * mm, "end": v(38, 10.58) * mm});
            skLineSegment(sketch, "E606", {"start": v(38, 10.58) * mm, "end": v(38.85, 7.6) * mm});
            skLineSegment(sketch, "E607", {"start": v(38.85, 7.6) * mm, "end": v(40.04, 7.82) * mm});
            skLineSegment(sketch, "E608", {"start": v(44.17, 16.2) * mm, "end": v(43.85, 17.71) * mm});
            skLineSegment(sketch, "E609", {"start": v(43.85, 17.71) * mm, "end": v(44.5, 17.9) * mm});
            skLineSegment(sketch, "E610", {"start": v(44.5, 17.9) * mm, "end": v(45.32, 16.86) * mm});
            skLineSegment(sketch, "E611", {"start": v(45.32, 16.86) * mm, "end": v(44.86, 16.58) * mm});
            skLineSegment(sketch, "E612", {"start": v(44.86, 16.58) * mm, "end": v(44.75, 16.41) * mm});
            skLineSegment(sketch, "E613", {"start": v(44.75, 16.41) * mm, "end": v(44.17, 16.2) * mm});
            skLineSegment(sketch, "E614", {"start": v(44.17, 16.2) * mm, "end": v(44.1, 16.06) * mm});
            skLineSegment(sketch, "E615", {"start": v(44.1, 16.06) * mm, "end": v(42.42, 15.45) * mm});
            skLineSegment(sketch, "E616", {"start": v(42.42, 15.45) * mm, "end": v(42.36, 15.51) * mm});
            skLineSegment(sketch, "E617", {"start": v(42.36, 15.51) * mm, "end": v(41.75, 14.94) * mm});
            skLineSegment(sketch, "E618", {"start": v(41.75, 14.94) * mm, "end": v(41.18, 14.59) * mm});
            skLineSegment(sketch, "E619", {"start": v(43.85, 17.71) * mm, "end": v(40.82, 17.1) * mm});
            skLineSegment(sketch, "E620", {"start": v(40.82, 18.87) * mm, "end": v(44.33, 19.7) * mm});
            skLineSegment(sketch, "E621", {"start": v(44.33, 19.7) * mm, "end": v(44.58, 20.05) * mm});
            skLineSegment(sketch, "E622", {"start": v(44.58, 20.05) * mm, "end": v(44.98, 20.2) * mm});
            skLineSegment(sketch, "E623", {"start": v(44.98, 20.2) * mm, "end": v(45.26, 19.77) * mm});
            skLineSegment(sketch, "E624", {"start": v(45.26, 19.77) * mm, "end": v(45.02, 19.04) * mm});
            skLineSegment(sketch, "E625", {"start": v(45.02, 19.04) * mm, "end": v(45.22, 18.74) * mm});
            skLineSegment(sketch, "E626", {"start": v(45.22, 18.74) * mm, "end": v(45.33, 18.83) * mm});
            skLineSegment(sketch, "E627", {"start": v(45.33, 18.83) * mm, "end": v(45.57, 18.77) * mm});
            skLineSegment(sketch, "E628", {"start": v(45.57, 18.77) * mm, "end": v(46.18, 17.87) * mm});
            skLineSegment(sketch, "E629", {"start": v(46.18, 17.87) * mm, "end": v(46.65, 17.82) * mm});
            skLineSegment(sketch, "E630", {"start": v(46.65, 17.82) * mm, "end": v(46.9, 17.95) * mm});
            skLineSegment(sketch, "E631", {"start": v(46.9, 17.95) * mm, "end": v(47.02, 18.08) * mm});
            skLineSegment(sketch, "E632", {"start": v(45.32, 16.86) * mm, "end": v(45.63, 17) * mm});
            skLineSegment(sketch, "E633", {"start": v(45.63, 17) * mm, "end": v(45.6, 17.26) * mm});
            skLineSegment(sketch, "E634", {"start": v(45.6, 17.26) * mm, "end": v(46, 17.54) * mm});
            skLineSegment(sketch, "E635", {"start": v(46, 17.54) * mm, "end": v(46.11, 17.06) * mm});
            skLineSegment(sketch, "E636", {"start": v(46.11, 17.06) * mm, "end": v(46.36, 17.34) * mm});
            skLineSegment(sketch, "E637", {"start": v(46.36, 17.34) * mm, "end": v(46.69, 17.54) * mm});
            skLineSegment(sketch, "E638", {"start": v(46.69, 17.54) * mm, "end": v(47.07, 17.68) * mm});
            skLineSegment(sketch, "E639", {"start": v(47.07, 17.68) * mm, "end": v(47.3, 17.75) * mm});
            skLineSegment(sketch, "E640", {"start": v(47.3, 17.75) * mm, "end": v(47.25, 18.16) * mm});
            skLineSegment(sketch, "E641", {"start": v(47.25, 18.16) * mm, "end": v(47.07, 18.4) * mm});
            skLineSegment(sketch, "E642", {"start": v(47.02, 18.08) * mm, "end": v(47.07, 18.4) * mm});
            skLineSegment(sketch, "E643", {"start": v(39.46, 24.13) * mm, "end": v(42.4, 24.95) * mm});
            skLineSegment(sketch, "E644", {"start": v(42.4, 24.95) * mm, "end": v(42.52, 24.67) * mm});
            skLineSegment(sketch, "E645", {"start": v(42.52, 24.67) * mm, "end": v(42.42, 24.26) * mm});
            skLineSegment(sketch, "E646", {"start": v(42.42, 24.26) * mm, "end": v(42.69, 23.94) * mm});
            skLineSegment(sketch, "E647", {"start": v(42.69, 23.94) * mm, "end": v(42.63, 23.86) * mm});
            skLineSegment(sketch, "E648", {"start": v(42.63, 23.86) * mm, "end": v(42.7, 23.7) * mm});
            skLineSegment(sketch, "E649", {"start": v(42.7, 23.7) * mm, "end": v(42.23, 23.18) * mm});
            skLineSegment(sketch, "E650", {"start": v(42.23, 23.18) * mm, "end": v(41.98, 23.07) * mm});
            skLineSegment(sketch, "E651", {"start": v(41.98, 23.07) * mm, "end": v(41.98, 22.87) * mm});
            skLineSegment(sketch, "E652", {"start": v(41.98, 22.87) * mm, "end": v(42.09, 22.75) * mm});
            skLineSegment(sketch, "E653", {"start": v(42.09, 22.75) * mm, "end": v(41.98, 20.18) * mm});
            skLineSegment(sketch, "E654", {"start": v(41.98, 20.18) * mm, "end": v(42.09, 20.14) * mm});
            skLineSegment(sketch, "E655", {"start": v(42.09, 20.14) * mm, "end": v(42.07, 19.61) * mm});
            skLineSegment(sketch, "E656", {"start": v(42.07, 19.61) * mm, "end": v(42.07, 19.38) * mm});
            skLineSegment(sketch, "E657", {"start": v(42.07, 19.38) * mm, "end": v(42.26, 19.2) * mm});
            skLineSegment(sketch, "E658", {"start": v(13.9, 0.38) * mm, "end": v(14.14, 0.73) * mm});
            skLineSegment(sketch, "E659", {"start": v(14.14, 0.73) * mm, "end": v(14.44, 0.92) * mm});
            skLineSegment(sketch, "E660", {"start": v(14.44, 0.92) * mm, "end": v(15.25, 0.63) * mm});
            skLineSegment(sketch, "E661", {"start": v(15.25, 0.63) * mm, "end": v(15.36, 0.8) * mm});
            skLineSegment(sketch, "E662", {"start": v(15.36, 0.8) * mm, "end": v(15.2, 1.05) * mm});
            skLineSegment(sketch, "E663", {"start": v(15.2, 1.05) * mm, "end": v(15.23, 1.43) * mm});
            skLineSegment(sketch, "E664", {"start": v(15.23, 1.43) * mm, "end": v(15.62, 1.62) * mm});
            skLineSegment(sketch, "E665", {"start": v(15.62, 1.62) * mm, "end": v(15.93, 1.78) * mm});
            skLineSegment(sketch, "E666", {"start": v(15.93, 1.78) * mm, "end": v(15.72, 2.14) * mm});
            skLineSegment(sketch, "E667", {"start": v(15.72, 2.14) * mm, "end": v(15.93, 2.35) * mm});
            skLineSegment(sketch, "E668", {"start": v(15.93, 2.35) * mm, "end": v(16, 2.63) * mm});
            skLineSegment(sketch, "E669", {"start": v(16, 2.63) * mm, "end": v(16.07, 3.6) * mm});
            skLineSegment(sketch, "E670", {"start": v(16.07, 3.6) * mm, "end": v(16.76, 4.67) * mm});
            skLineSegment(sketch, "E671", {"start": v(16.76, 4.67) * mm, "end": v(16.7, 5.42) * mm});
            skLineSegment(sketch, "E672", {"start": v(16.7, 5.42) * mm, "end": v(16.45, 5.8) * mm});
            skLineSegment(sketch, "E673", {"start": v(16.45, 5.8) * mm, "end": v(16.58, 6.46) * mm});
            skLineSegment(sketch, "E674", {"start": v(16, 2.63) * mm, "end": v(17.3, 2.95) * mm});
            skLineSegment(sketch, "E675", {"start": v(17.3, 2.95) * mm, "end": v(17.75, 2.61) * mm});
            skLineSegment(sketch, "E676", {"start": v(17.75, 2.61) * mm, "end": v(17.89, 2.98) * mm});
            skLineSegment(sketch, "E677", {"start": v(17.89, 2.98) * mm, "end": v(18.25, 3.16) * mm});
            skLineSegment(sketch, "E678", {"start": v(18.25, 3.16) * mm, "end": v(18.57, 2.88) * mm});
            skLineSegment(sketch, "E679", {"start": v(18.57, 2.88) * mm, "end": v(18.74, 2.9) * mm});
            skLineSegment(sketch, "E680", {"start": v(18.74, 2.9) * mm, "end": v(18.8, 3.33) * mm});
            skLineSegment(sketch, "E681", {"start": v(18.8, 3.33) * mm, "end": v(19.19, 3.58) * mm});
            skLineSegment(sketch, "E682", {"start": v(19.19, 3.58) * mm, "end": v(19.33, 3.4) * mm});
            skLineSegment(sketch, "E683", {"start": v(19.33, 3.4) * mm, "end": v(19.83, 3.38) * mm});
            skLineSegment(sketch, "E684", {"start": v(19.83, 3.38) * mm, "end": v(19.87, 3.95) * mm});
            skLineSegment(sketch, "E685", {"start": v(19.87, 3.95) * mm, "end": v(20.75, 4.7) * mm});
            skLineSegment(sketch, "E686", {"start": v(20.75, 4.7) * mm, "end": v(20.77, 5.23) * mm});
            skLineSegment(sketch, "E687", {"start": v(20.77, 5.23) * mm, "end": v(21.13, 5.21) * mm});
            skLineSegment(sketch, "E688", {"start": v(21.13, 5.21) * mm, "end": v(21.83, 5.62) * mm});
            skLineSegment(sketch, "E689", {"start": v(21.83, 5.62) * mm, "end": v(21.81, 5.85) * mm});
            skLineSegment(sketch, "E690", {"start": v(21.81, 5.85) * mm, "end": v(21.55, 6.05) * mm});
            skLineSegment(sketch, "E691", {"start": v(21.55, 6.05) * mm, "end": v(21.7, 6.25) * mm});
            skLineSegment(sketch, "E692", {"start": v(23.88, -3.62) * mm, "end": v(23.8, -3.01) * mm});
            skLineSegment(sketch, "E693", {"start": v(23.8, -3.01) * mm, "end": v(24.38, -2.84) * mm});
            skLineSegment(sketch, "E694", {"start": v(24.38, -2.84) * mm, "end": v(24.35, -2.5) * mm});
            skLineSegment(sketch, "E695", {"start": v(24.35, -2.5) * mm, "end": v(24.86, -2.08) * mm});
            skLineSegment(sketch, "E696", {"start": v(24.86, -2.08) * mm, "end": v(25.36, -2.05) * mm});
            skLineSegment(sketch, "E697", {"start": v(25.36, -2.05) * mm, "end": v(25.72, -1.6) * mm});
            skLineSegment(sketch, "E698", {"start": v(25.72, -1.6) * mm, "end": v(26.28, -1.33) * mm});
            skLineSegment(sketch, "E699", {"start": v(26.28, -1.33) * mm, "end": v(26.31, -1) * mm});
            skLineSegment(sketch, "E700", {"start": v(26.31, -1) * mm, "end": v(26.81, -0.54) * mm});
            skLineSegment(sketch, "E701", {"start": v(26.81, -0.54) * mm, "end": v(26.93, -0.71) * mm});
            skLineSegment(sketch, "E702", {"start": v(26.93, -0.71) * mm, "end": v(27.15, -0.74) * mm});
            skLineSegment(sketch, "E703", {"start": v(27.15, -0.74) * mm, "end": v(27.37, -0.24) * mm});
            skLineSegment(sketch, "E704", {"start": v(27.37, -0.24) * mm, "end": v(27.85, -0.24) * mm});
            skLineSegment(sketch, "E705", {"start": v(27.85, -0.24) * mm, "end": v(28.02, 0.15) * mm});
            skLineSegment(sketch, "E706", {"start": v(28.02, 0.15) * mm, "end": v(28.35, 0.38) * mm});
            skLineSegment(sketch, "E707", {"start": v(28.35, 0.38) * mm, "end": v(28.4, 0.93) * mm});
            skLineSegment(sketch, "E708", {"start": v(24.8, 0.46) * mm, "end": v(25.99, 1.28) * mm});
            skLineSegment(sketch, "E709", {"start": v(25.99, 1.28) * mm, "end": v(25.97, 1.56) * mm});
            skLineSegment(sketch, "E710", {"start": v(25.97, 1.56) * mm, "end": v(27.45, 3.14) * mm});
            skLineSegment(sketch, "E711", {"start": v(27.45, 3.14) * mm, "end": v(26.52, 3.97) * mm});
            skLineSegment(sketch, "E712", {"start": v(26.52, 3.97) * mm, "end": v(26.46, 4.24) * mm});
            skLineSegment(sketch, "E713", {"start": v(26.46, 4.24) * mm, "end": v(26.13, 5.17) * mm});
            skLineSegment(sketch, "E714", {"start": v(26.13, 5.17) * mm, "end": v(25.51, 5.55) * mm});
            skLineSegment(sketch, "E715", {"start": v(25.51, 5.55) * mm, "end": v(25.36, 5.92) * mm});
            skLineSegment(sketch, "E716", {"start": v(25.36, 5.92) * mm, "end": v(24.74, 5.43) * mm});
            skLineSegment(sketch, "E717", {"start": v(24.74, 5.43) * mm, "end": v(24.58, 5.59) * mm});
            skLineSegment(sketch, "E718", {"start": v(24.58, 5.59) * mm, "end": v(24.27, 5.65) * mm});
            skLineSegment(sketch, "E719", {"start": v(24.27, 5.65) * mm, "end": v(23.91, 5.43) * mm});
            skLineSegment(sketch, "E720", {"start": v(23.91, 5.43) * mm, "end": v(23.62, 5.7) * mm});
            skLineSegment(sketch, "E721", {"start": v(23.62, 5.7) * mm, "end": v(22.98, 5.73) * mm});
            skLineSegment(sketch, "E722", {"start": v(22.98, 5.73) * mm, "end": v(22.69, 6.22) * mm});
            skLineSegment(sketch, "E723", {"start": v(22.69, 6.22) * mm, "end": v(22.45, 6.34) * mm});
            skLineSegment(sketch, "E724", {"start": v(22.45, 6.34) * mm, "end": v(21.7, 6.25) * mm});
            skLineSegment(sketch, "E725", {"start": v(38, 10.58) * mm, "end": v(38.43, 10.88) * mm});
            skLineSegment(sketch, "E726", {"start": v(38.43, 10.88) * mm, "end": v(39, 11.1) * mm});
            skLineSegment(sketch, "E727", {"start": v(39, 11.1) * mm, "end": v(39.68, 12.03) * mm});
            skLineSegment(sketch, "E728", {"start": v(39.68, 12.03) * mm, "end": v(39.07, 12.56) * mm});
            skLineSegment(sketch, "E729", {"start": v(39.07, 12.56) * mm, "end": v(38.93, 12.87) * mm});
            skLineSegment(sketch, "E730", {"start": v(38.93, 12.87) * mm, "end": v(38.67, 12.86) * mm});
            skLineSegment(sketch, "E731", {"start": v(38.67, 12.86) * mm, "end": v(38.53, 13.32) * mm});
            skLineSegment(sketch, "E732", {"start": v(38.53, 13.32) * mm, "end": v(38.78, 13.42) * mm});
            skLineSegment(sketch, "E733", {"start": v(38.78, 13.42) * mm, "end": v(38.77, 13.69) * mm});
            skLineSegment(sketch, "E734", {"start": v(38.77, 13.69) * mm, "end": v(38.58, 13.82) * mm});
            skLineSegment(sketch, "E735", {"start": v(38.58, 13.82) * mm, "end": v(38.85, 14.3) * mm});
            skLineSegment(sketch, "E736", {"start": v(38.85, 14.3) * mm, "end": v(38.92, 14.7) * mm});
            skLineSegment(sketch, "E737", {"start": v(38.92, 14.7) * mm, "end": v(39.13, 14.92) * mm});
            skLineSegment(sketch, "E738", {"start": v(38.64, 10.96) * mm, "end": v(38.55, 10.38) * mm});
            skLineSegment(sketch, "E739", {"start": v(38.55, 10.38) * mm, "end": v(38.87, 10) * mm});
            skLineSegment(sketch, "E740", {"start": v(38.87, 10) * mm, "end": v(39.52, 9.66) * mm});
            skLineSegment(sketch, "E741", {"start": v(39.52, 9.66) * mm, "end": v(40, 9.59) * mm});
            skLineSegment(sketch, "E742", {"start": v(40, 9.59) * mm, "end": v(40, 9.38) * mm});
            skLineSegment(sketch, "E743", {"start": v(40, 9.38) * mm, "end": v(39.92, 9.32) * mm});
            skLineSegment(sketch, "E744", {"start": v(39.92, 9.32) * mm, "end": v(39.93, 9) * mm});
            skLineSegment(sketch, "E745", {"start": v(39.93, 9) * mm, "end": v(40.26, 9.24) * mm});
            skLineSegment(sketch, "E746", {"start": v(40.26, 9.24) * mm, "end": v(40.35, 9.73) * mm});
            skLineSegment(sketch, "E747", {"start": v(40.35, 9.73) * mm, "end": v(40.77, 10.44) * mm});
            skLineSegment(sketch, "E748", {"start": v(40.77, 10.44) * mm, "end": v(41.07, 11.18) * mm});
            skLineSegment(sketch, "E749", {"start": v(41.07, 11.18) * mm, "end": v(41.04, 11.74) * mm});
            skLineSegment(sketch, "E750", {"start": v(41.04, 11.74) * mm, "end": v(41.04, 12.81) * mm});
            skLineSegment(sketch, "E751", {"start": v(41.04, 12.81) * mm, "end": v(40.87, 13.1) * mm});
            skLineSegment(sketch, "E752", {"start": v(40.87, 13.1) * mm, "end": v(40.47, 12.97) * mm});
            skLineSegment(sketch, "E753", {"start": v(40.47, 12.97) * mm, "end": v(40.4, 13.08) * mm});
            skLineSegment(sketch, "E754", {"start": v(40.4, 13.08) * mm, "end": v(40.72, 13.34) * mm});
            skLineSegment(sketch, "E755", {"start": v(40.72, 13.34) * mm, "end": v(40.77, 13.52) * mm});
            skLineSegment(sketch, "E756", {"start": v(26.13, 5.17) * mm, "end": v(26.47, 5.3) * mm});
            skLineSegment(sketch, "E757", {"start": v(26.47, 5.3) * mm, "end": v(26.54, 5.67) * mm});
            skLineSegment(sketch, "E758", {"start": v(26.54, 5.67) * mm, "end": v(26.7, 5.72) * mm});
            skLineSegment(sketch, "E759", {"start": v(26.7, 5.72) * mm, "end": v(26.78, 6.72) * mm});
            skLineSegment(sketch, "E760", {"start": v(26.78, 6.72) * mm, "end": v(27, 6.77) * mm});
            skLineSegment(sketch, "E761", {"start": v(27, 6.77) * mm, "end": v(27.18, 6.52) * mm});
            skLineSegment(sketch, "E762", {"start": v(27.18, 6.52) * mm, "end": v(27.38, 6.62) * mm});
            skLineSegment(sketch, "E763", {"start": v(27.38, 6.62) * mm, "end": v(27.4, 6.76) * mm});
            skLineSegment(sketch, "E764", {"start": v(27.4, 6.76) * mm, "end": v(27.22, 7.04) * mm});
            skLineSegment(sketch, "E765", {"start": v(27.22, 7.04) * mm, "end": v(27.82, 7.92) * mm});
            skLineSegment(sketch, "E766", {"start": v(27.82, 7.92) * mm, "end": v(28, 7.83) * mm});
            skLineSegment(sketch, "E767", {"start": v(28, 7.83) * mm, "end": v(28.86, 8.77) * mm});
            skLineSegment(sketch, "E768", {"start": v(28.86, 8.77) * mm, "end": v(28.94, 10.52) * mm});
            skLineSegment(sketch, "E769", {"start": v(28.94, 10.52) * mm, "end": v(28.78, 10.94) * mm});
            skLineSegment(sketch, "E770", {"start": v(28.78, 10.94) * mm, "end": v(29.08, 11.11) * mm});
            skLineSegment(sketch, "E771", {"start": v(23.37, 13) * mm, "end": v(24, 12.75) * mm});
            skLineSegment(sketch, "E772", {"start": v(24, 12.75) * mm, "end": v(24.6, 12.78) * mm});
            skLineSegment(sketch, "E773", {"start": v(24.6, 12.78) * mm, "end": v(25.01, 12.46) * mm});
            skLineSegment(sketch, "E774", {"start": v(25.01, 12.46) * mm, "end": v(25.25, 12.5) * mm});
            skLineSegment(sketch, "E775", {"start": v(25.25, 12.5) * mm, "end": v(25.86, 12.79) * mm});
            skLineSegment(sketch, "E776", {"start": v(25.86, 12.79) * mm, "end": v(26.55, 12.9) * mm});
            skLineSegment(sketch, "E777", {"start": v(26.55, 12.9) * mm, "end": v(27.36, 13.73) * mm});
            skLineSegment(sketch, "E778", {"start": v(27.36, 13.73) * mm, "end": v(28.57, 14.43) * mm});
            skLineSegment(sketch, "E779", {"start": v(9.13, 16.1) * mm, "end": v(9, 16.92) * mm});
            skLineSegment(sketch, "E780", {"start": v(9, 16.92) * mm, "end": v(8.87, 17.22) * mm});
            skLineSegment(sketch, "E781", {"start": v(8.87, 17.22) * mm, "end": v(8.11, 17.61) * mm});
            skLineSegment(sketch, "E782", {"start": v(8.11, 17.61) * mm, "end": v(7.68, 18.31) * mm});
            skLineSegment(sketch, "E783", {"start": v(7.68, 18.31) * mm, "end": v(7.16, 18.36) * mm});
            skLineSegment(sketch, "E784", {"start": v(7.16, 18.36) * mm, "end": v(7.03, 18.74) * mm});
            skLineSegment(sketch, "E785", {"start": v(7.03, 18.74) * mm, "end": v(6.76, 18.73) * mm});
            skLineSegment(sketch, "E786", {"start": v(6.76, 18.73) * mm, "end": v(6.45, 19) * mm});
            skLineSegment(sketch, "E787", {"start": v(6.45, 19) * mm, "end": v(6.33, 20.26) * mm});
            skLineSegment(sketch, "E788", {"start": v(6.33, 20.26) * mm, "end": v(6.5, 20.5) * mm});
            skLineSegment(sketch, "E789", {"start": v(6.5, 20.5) * mm, "end": v(6.45, 20.94) * mm});
            skLineSegment(sketch, "E790", {"start": v(6.45, 20.94) * mm, "end": v(6.1, 21.15) * mm});
            skLineSegment(sketch, "E791", {"start": v(6.1, 21.15) * mm, "end": v(6.37, 21.87) * mm});
            skLineSegment(sketch, "E792", {"start": v(6.37, 21.87) * mm, "end": v(7.08, 22.38) * mm});
            skLineSegment(sketch, "E793", {"start": v(7.08, 22.38) * mm, "end": v(7.08, 23.68) * mm});
            skLineSegment(sketch, "E794", {"start": v(7.08, 23.68) * mm, "end": v(7.37, 23.92) * mm});
            skLineSegment(sketch, "E795", {"start": v(10.3, 23.74) * mm, "end": v(10.72, 23.09) * mm});
            skLineSegment(sketch, "E796", {"start": v(10.72, 23.09) * mm, "end": v(11.41, 23.02) * mm});
            skLineSegment(sketch, "E797", {"start": v(11.41, 23.02) * mm, "end": v(12.57, 22.72) * mm});
            skLineSegment(sketch, "E798", {"start": v(12.57, 22.72) * mm, "end": v(12.84, 22.54) * mm});
            skLineSegment(sketch, "E799", {"start": v(12.84, 22.54) * mm, "end": v(14.25, 22.3) * mm});
            skLineSegment(sketch, "E800", {"start": v(14.25, 22.3) * mm, "end": v(14.34, 22.02) * mm});
            skLineSegment(sketch, "E801", {"start": v(14.34, 22.02) * mm, "end": v(14.76, 21.9) * mm});
            skLineSegment(sketch, "E802", {"start": v(14.76, 21.9) * mm, "end": v(14.88, 20.82) * mm});
            skLineSegment(sketch, "E803", {"start": v(14.88, 20.82) * mm, "end": v(15.23, 20.5) * mm});
            skLineSegment(sketch, "E804", {"start": v(15.75, 23.95) * mm, "end": v(15.9, 24.05) * mm});
            skLineSegment(sketch, "E805", {"start": v(15.9, 24.05) * mm, "end": v(16.17, 23.83) * mm});
            skLineSegment(sketch, "E806", {"start": v(16.17, 23.83) * mm, "end": v(16.41, 23.98) * mm});
            skLineSegment(sketch, "E807", {"start": v(16.41, 23.98) * mm, "end": v(16.57, 23.91) * mm});
            skLineSegment(sketch, "E808", {"start": v(16.57, 23.91) * mm, "end": v(17.18, 24.45) * mm});
            skLineSegment(sketch, "E809", {"start": v(17.18, 24.45) * mm, "end": v(17.6, 24.56) * mm});
            skLineSegment(sketch, "E810", {"start": v(17.6, 24.56) * mm, "end": v(18.21, 24.6) * mm});
            skLineSegment(sketch, "E811", {"start": v(18.21, 24.6) * mm, "end": v(19, 24.93) * mm});
            skLineSegment(sketch, "E812", {"start": v(19, 24.93) * mm, "end": v(19.19, 24.9) * mm});
            skLineSegment(sketch, "E813", {"start": v(19.19, 24.9) * mm, "end": v(19.17, 24.32) * mm});
            skLineSegment(sketch, "E814", {"start": v(19.17, 24.32) * mm, "end": v(19.62, 24.18) * mm});
            skLineSegment(sketch, "E815", {"start": v(19.62, 24.18) * mm, "end": v(20.48, 24.43) * mm});
            skLineSegment(sketch, "E816", {"start": v(20.48, 24.43) * mm, "end": v(20.57, 24.55) * mm});
            skLineSegment(sketch, "E817", {"start": v(20.57, 24.55) * mm, "end": v(20.74, 24.48) * mm});
            skLineSegment(sketch, "E818", {"start": v(20.74, 24.48) * mm, "end": v(20.74, 23.76) * mm});
            skLineSegment(sketch, "E819", {"start": v(20.74, 23.76) * mm, "end": v(21.27, 23.21) * mm});
            skLineSegment(sketch, "E820", {"start": v(21.27, 23.21) * mm, "end": v(20.81, 23.22) * mm});
            skLineSegment(sketch, "E821", {"start": v(20.81, 23.22) * mm, "end": v(20.6, 23.16) * mm});
            skLineSegment(sketch, "E822", {"start": v(20.6, 23.16) * mm, "end": v(20.27, 23.2) * mm});
            skLineSegment(sketch, "E823", {"start": v(20.27, 23.2) * mm, "end": v(19.95, 23.01) * mm});
            skLineSegment(sketch, "E824", {"start": v(19.95, 23.01) * mm, "end": v(19.23, 23.13) * mm});
            skLineSegment(sketch, "E825", {"start": v(19.23, 23.13) * mm, "end": v(18.53, 23.13) * mm});
            skLineSegment(sketch, "E826", {"start": v(18.53, 23.13) * mm, "end": v(18.33, 22.85) * mm});
            skLineSegment(sketch, "E827", {"start": v(18.33, 22.85) * mm, "end": v(17.31, 22.74) * mm});
            skLineSegment(sketch, "E828", {"start": v(17.31, 22.74) * mm, "end": v(17.1, 22.31) * mm});
            skLineSegment(sketch, "E829", {"start": v(17.1, 22.31) * mm, "end": v(17, 22.26) * mm});
            skLineSegment(sketch, "E830", {"start": v(17, 22.26) * mm, "end": v(16.75, 22.41) * mm});
            skLineSegment(sketch, "E831", {"start": v(16.75, 22.41) * mm, "end": v(16.24, 22.18) * mm});
            skLineSegment(sketch, "E832", {"start": v(16.24, 22.18) * mm, "end": v(16.02, 22.36) * mm});
            skLineSegment(sketch, "E833", {"start": v(16.02, 22.36) * mm, "end": v(15.96, 22.35) * mm});
            skLineSegment(sketch, "E834", {"start": v(15.96, 22.35) * mm, "end": v(15.23, 20.5) * mm});
            skLineSegment(sketch, "E835", {"start": v(15.23, 20.5) * mm, "end": v(14.53, 19.36) * mm});
            skLineSegment(sketch, "E836", {"start": v(14.53, 19.36) * mm, "end": v(14.56, 19.13) * mm});
            skLineSegment(sketch, "E837", {"start": v(14.56, 19.13) * mm, "end": v(14.74, 19.07) * mm});
            skLineSegment(sketch, "E838", {"start": v(14.74, 19.07) * mm, "end": v(14.81, 19.34) * mm});
            skLineSegment(sketch, "E839", {"start": v(14.81, 19.34) * mm, "end": v(15.32, 19.77) * mm});
            skLineSegment(sketch, "E840", {"start": v(15.32, 19.77) * mm, "end": v(16.13, 20.99) * mm});
            skLineSegment(sketch, "E841", {"start": v(16.13, 20.99) * mm, "end": v(16.22, 20.7) * mm});
            skLineSegment(sketch, "E842", {"start": v(16.22, 20.7) * mm, "end": v(15.54, 19.3) * mm});
            skLineSegment(sketch, "E843", {"start": v(15.54, 19.3) * mm, "end": v(15.43, 18.64) * mm});
            skLineSegment(sketch, "E844", {"start": v(15.43, 18.64) * mm, "end": v(15.52, 18.54) * mm});
            skLineSegment(sketch, "E845", {"start": v(15.52, 18.54) * mm, "end": v(15.55, 18.28) * mm});
            skLineSegment(sketch, "E846", {"start": v(15.55, 18.28) * mm, "end": v(15.23, 17.83) * mm});
            skLineSegment(sketch, "E847", {"start": v(15.23, 17.83) * mm, "end": v(15.39, 16.95) * mm});
            skLineSegment(sketch, "E848", {"start": v(15.39, 16.95) * mm, "end": v(15.04, 15.99) * mm});
            skLineSegment(sketch, "E849", {"start": v(15.04, 15.99) * mm, "end": v(15.17, 15.6) * mm});
            skLineSegment(sketch, "E850", {"start": v(15.17, 15.6) * mm, "end": v(15.22, 15) * mm});
            skLineSegment(sketch, "E851", {"start": v(15.22, 15) * mm, "end": v(15.41, 14.57) * mm});
            skLineSegment(sketch, "E852", {"start": v(15.41, 14.57) * mm, "end": v(15.3, 14.07) * mm});
            skLineSegment(sketch, "E853", {"start": v(44.98, 20.2) * mm, "end": v(45.14, 20.76) * mm});
            skLineSegment(sketch, "E854", {"start": v(45.14, 20.76) * mm, "end": v(44.84, 20.88) * mm});
            skLineSegment(sketch, "E855", {"start": v(44.84, 20.88) * mm, "end": v(44.83, 21.22) * mm});
            skLineSegment(sketch, "E856", {"start": v(44.83, 21.22) * mm, "end": v(44.43, 21.32) * mm});
            skLineSegment(sketch, "E857", {"start": v(44.43, 21.32) * mm, "end": v(42.98, 25.8) * mm});
            skLineSegment(sketch, "E858", {"start": v(42.98, 25.8) * mm, "end": v(42.92, 25.54) * mm});
            skLineSegment(sketch, "E859", {"start": v(42.92, 25.54) * mm, "end": v(42.71, 25.71) * mm});
            skLineSegment(sketch, "E860", {"start": v(42.71, 25.71) * mm, "end": v(42.6, 25.67) * mm});
            skLineSegment(sketch, "E861", {"start": v(42.6, 25.67) * mm, "end": v(42.4, 24.95) * mm});
            skLineSegment(sketch, "E862", {"start": v(42.98, 25.8) * mm, "end": v(43.13, 25.84) * mm});
            skLineSegment(sketch, "E863", {"start": v(43.13, 25.84) * mm, "end": v(43.5, 25.78) * mm});
            skLineSegment(sketch, "E864", {"start": v(43.5, 25.78) * mm, "end": v(43.59, 26.73) * mm});
            skLineSegment(sketch, "E865", {"start": v(43.59, 26.73) * mm, "end": v(44.04, 27.76) * mm});
            skLineSegment(sketch, "E866", {"start": v(44.04, 27.76) * mm, "end": v(43.82, 28) * mm});
            skLineSegment(sketch, "E867", {"start": v(43.82, 28) * mm, "end": v(43.82, 28.64) * mm});
            skLineSegment(sketch, "E868", {"start": v(43.82, 28.64) * mm, "end": v(44, 28.97) * mm});
            skLineSegment(sketch, "E869", {"start": v(44, 28.97) * mm, "end": v(44, 29.83) * mm});
            skLineSegment(sketch, "E870", {"start": v(44, 29.83) * mm, "end": v(44.67, 31.66) * mm});
            skLineSegment(sketch, "E871", {"start": v(44.67, 31.66) * mm, "end": v(44.84, 31.67) * mm});
            skLineSegment(sketch, "E872", {"start": v(44.84, 31.67) * mm, "end": v(45.04, 31.26) * mm});
            skLineSegment(sketch, "E873", {"start": v(45.04, 31.26) * mm, "end": v(45.4, 31.2) * mm});
            skLineSegment(sketch, "E874", {"start": v(45.4, 31.2) * mm, "end": v(45.54, 31.33) * mm});
            skLineSegment(sketch, "E875", {"start": v(45.54, 31.33) * mm, "end": v(45.52, 31.5) * mm});
            skLineSegment(sketch, "E876", {"start": v(45.52, 31.5) * mm, "end": v(46.15, 31.93) * mm});
            skLineSegment(sketch, "E877", {"start": v(46.15, 31.93) * mm, "end": v(47.1, 31.58) * mm});
            skLineSegment(sketch, "E878", {"start": v(47.1, 31.58) * mm, "end": v(48.1, 28.24) * mm});
            skLineSegment(sketch, "E879", {"start": v(48.1, 28.24) * mm, "end": v(48.72, 28.25) * mm});
            skLineSegment(sketch, "E880", {"start": v(48.72, 28.25) * mm, "end": v(48.84, 28.12) * mm});
            skLineSegment(sketch, "E881", {"start": v(48.84, 28.12) * mm, "end": v(48.81, 27.54) * mm});
            skLineSegment(sketch, "E882", {"start": v(48.81, 27.54) * mm, "end": v(49.16, 27.24) * mm});
            skLineSegment(sketch, "E883", {"start": v(49.16, 27.24) * mm, "end": v(49.35, 27.23) * mm});
            skLineSegment(sketch, "E884", {"start": v(49.35, 27.23) * mm, "end": v(49.39, 27.42) * mm});
            skLineSegment(sketch, "E885", {"start": v(49.39, 27.42) * mm, "end": v(49.65, 27.45) * mm});
            skLineSegment(sketch, "E886", {"start": v(49.65, 27.45) * mm, "end": v(50.1, 26.8) * mm});
            skLineSegment(sketch, "E887", {"start": v(50.1, 26.8) * mm, "end": v(49.84, 26.09) * mm});
            skLineSegment(sketch, "E888", {"start": v(49.84, 26.09) * mm, "end": v(49.66, 26.09) * mm});
            skLineSegment(sketch, "E889", {"start": v(49.66, 26.09) * mm, "end": v(48.7, 25.05) * mm});
            skLineSegment(sketch, "E890", {"start": v(48.7, 25.05) * mm, "end": v(48.54, 25.16) * mm});
            skLineSegment(sketch, "E891", {"start": v(48.54, 25.16) * mm, "end": v(48.45, 25.33) * mm});
            skLineSegment(sketch, "E892", {"start": v(48.45, 25.33) * mm, "end": v(48.22, 25.32) * mm});
            skLineSegment(sketch, "E893", {"start": v(48.22, 25.32) * mm, "end": v(48.16, 25.15) * mm});
            skLineSegment(sketch, "E894", {"start": v(48.16, 25.15) * mm, "end": v(47.85, 24.82) * mm});
            skLineSegment(sketch, "E895", {"start": v(47.85, 24.82) * mm, "end": v(47.91, 24.64) * mm});
            skLineSegment(sketch, "E896", {"start": v(47.91, 24.64) * mm, "end": v(47.9, 24.3) * mm});
            skLineSegment(sketch, "E897", {"start": v(47.9, 24.3) * mm, "end": v(47.68, 24.33) * mm});
            skLineSegment(sketch, "E898", {"start": v(47.68, 24.33) * mm, "end": v(47.63, 24.58) * mm});
            skLineSegment(sketch, "E899", {"start": v(47.44, 24.59) * mm, "end": v(47.23, 24.93) * mm});
            skLineSegment(sketch, "E900", {"start": v(47.23, 24.93) * mm, "end": v(47.04, 24.84) * mm});
            skLineSegment(sketch, "E901", {"start": v(47.04, 24.84) * mm, "end": v(47.16, 24.64) * mm});
            skLineSegment(sketch, "E902", {"start": v(47.16, 24.64) * mm, "end": v(47.12, 24.21) * mm});
            skLineSegment(sketch, "E903", {"start": v(47.12, 24.21) * mm, "end": v(47.13, 23.88) * mm});
            skLineSegment(sketch, "E904", {"start": v(47.13, 23.88) * mm, "end": v(46.97, 23.59) * mm});
            skLineSegment(sketch, "E905", {"start": v(46.97, 23.59) * mm, "end": v(46.77, 23.57) * mm});
            skLineSegment(sketch, "E906", {"start": v(46.77, 23.57) * mm, "end": v(46.65, 23.54) * mm});
            skLineSegment(sketch, "E907", {"start": v(46.65, 23.54) * mm, "end": v(46.65, 23.23) * mm});
            skLineSegment(sketch, "E908", {"start": v(46.65, 23.23) * mm, "end": v(45.9, 22.83) * mm});
            skLineSegment(sketch, "E909", {"start": v(45.9, 22.83) * mm, "end": v(45.67, 22.94) * mm});
            skLineSegment(sketch, "E910", {"start": v(45.67, 22.94) * mm, "end": v(45.37, 22.58) * mm});
            skLineSegment(sketch, "E911", {"start": v(45.37, 22.58) * mm, "end": v(45.45, 22.2) * mm});
            skLineSegment(sketch, "E912", {"start": v(45.45, 22.2) * mm, "end": v(45.33, 22.11) * mm});
            skLineSegment(sketch, "E913", {"start": v(45.33, 22.11) * mm, "end": v(45.14, 20.76) * mm});
            skLineSegment(sketch, "E914", {"start": v(47.44, 24.59) * mm, "end": v(47.63, 24.58) * mm});
            skLineSegment(sketch, "E915", {"start": v(31.3, 9.34) * mm, "end": v(31.54, 8.06) * mm});
            skLineSegment(sketch, "E916", {"start": v(31.54, 8.06) * mm, "end": v(32.06, 8.77) * mm});
            skLineSegment(sketch, "E917", {"start": v(32.06, 8.77) * mm, "end": v(32.4, 8.7) * mm});
            skLineSegment(sketch, "E918", {"start": v(32.4, 8.7) * mm, "end": v(32.73, 9.17) * mm});
            skLineSegment(sketch, "E919", {"start": v(32.73, 9.17) * mm, "end": v(32.96, 9.09) * mm});
            skLineSegment(sketch, "E920", {"start": v(32.96, 9.09) * mm, "end": v(33.16, 9.15) * mm});
            skLineSegment(sketch, "E921", {"start": v(23.37, 13) * mm, "end": v(23.7, 13.86) * mm});
            skLineSegment(sketch, "E922", {"start": v(23.7, 13.86) * mm, "end": v(23.79, 14.47) * mm});
            skLineSegment(sketch, "E923", {"start": v(23.79, 14.47) * mm, "end": v(24.1, 14.77) * mm});
            skLineSegment(sketch, "E924", {"start": v(24.1, 14.77) * mm, "end": v(24.22, 15.18) * mm});
            skLineSegment(sketch, "E925", {"start": v(24.22, 15.18) * mm, "end": v(24.52, 15.6) * mm});
            skLineSegment(sketch, "E926", {"start": v(24.52, 15.6) * mm, "end": v(24.68, 16.23) * mm});
            skLineSegment(sketch, "E927", {"start": v(24.68, 16.23) * mm, "end": v(24.58, 16.82) * mm});
            skLineSegment(sketch, "E928", {"start": v(24.58, 16.82) * mm, "end": v(24.28, 17.75) * mm});
            skLineSegment(sketch, "E929", {"start": v(24.28, 17.75) * mm, "end": v(24.12, 18.4) * mm});
            skLineSegment(sketch, "E930", {"start": v(24.12, 18.4) * mm, "end": v(23.6, 18.94) * mm});
            skLineSegment(sketch, "E931", {"start": v(23.6, 18.94) * mm, "end": v(23.02, 18.6) * mm});
            skLineSegment(sketch, "E932", {"start": v(23.02, 18.6) * mm, "end": v(22.8, 17.95) * mm});
            skLineSegment(sketch, "E933", {"start": v(22.8, 17.95) * mm, "end": v(22.42, 17.57) * mm});
            skLineSegment(sketch, "E934", {"start": v(22.42, 17.57) * mm, "end": v(21.89, 17.77) * mm});
            skLineSegment(sketch, "E935", {"start": v(21.89, 17.77) * mm, "end": v(21.99, 18.42) * mm});
            skLineSegment(sketch, "E936", {"start": v(21.99, 18.42) * mm, "end": v(22.4, 18.54) * mm});
            skLineSegment(sketch, "E937", {"start": v(22.4, 18.54) * mm, "end": v(22.48, 19.21) * mm});
            skLineSegment(sketch, "E938", {"start": v(22.48, 19.21) * mm, "end": v(22.78, 19.35) * mm});
            skLineSegment(sketch, "E939", {"start": v(22.78, 19.35) * mm, "end": v(22.74, 20.46) * mm});
            skLineSegment(sketch, "E940", {"start": v(22.74, 20.46) * mm, "end": v(22.34, 20.83) * mm});
            skLineSegment(sketch, "E941", {"start": v(22.34, 20.83) * mm, "end": v(22.3, 21.01) * mm});
            skLineSegment(sketch, "E942", {"start": v(22.3, 21.01) * mm, "end": v(22.4, 21.19) * mm});
            skLineSegment(sketch, "E943", {"start": v(22.4, 21.19) * mm, "end": v(22.58, 21.15) * mm});
            skLineSegment(sketch, "E944", {"start": v(22.58, 21.15) * mm, "end": v(22.62, 21.29) * mm});
            skLineSegment(sketch, "E945", {"start": v(22.62, 21.29) * mm, "end": v(22.2, 21.84) * mm});
            skLineSegment(sketch, "E946", {"start": v(22.2, 21.84) * mm, "end": v(21.75, 21.88) * mm});
            skLineSegment(sketch, "E947", {"start": v(21.75, 21.88) * mm, "end": v(20.88, 22.35) * mm});
            skLineSegment(sketch, "E948", {"start": v(20.88, 22.35) * mm, "end": v(20.53, 22.4) * mm});
            skLineSegment(sketch, "E949", {"start": v(20.53, 22.4) * mm, "end": v(20.37, 22.3) * mm});
            skLineSegment(sketch, "E950", {"start": v(20.37, 22.3) * mm, "end": v(20.01, 22.6) * mm});
            skLineSegment(sketch, "E951", {"start": v(20.01, 22.6) * mm, "end": v(19.32, 22.22) * mm});
            skLineSegment(sketch, "E952", {"start": v(19.32, 22.22) * mm, "end": v(19.36, 21.8) * mm});
            skLineSegment(sketch, "E953", {"start": v(19.36, 21.8) * mm, "end": v(19.62, 21.74) * mm});
            skLineSegment(sketch, "E954", {"start": v(19.62, 21.74) * mm, "end": v(19.77, 21.56) * mm});
            skLineSegment(sketch, "E955", {"start": v(19.77, 21.56) * mm, "end": v(19.52, 21.45) * mm});
            skLineSegment(sketch, "E956", {"start": v(19.52, 21.45) * mm, "end": v(19.3, 21.49) * mm});
            skLineSegment(sketch, "E957", {"start": v(19.3, 21.49) * mm, "end": v(19.06, 21.2) * mm});
            skLineSegment(sketch, "E958", {"start": v(19.06, 21.2) * mm, "end": v(19.12, 20.28) * mm});
            skLineSegment(sketch, "E959", {"start": v(19.12, 20.28) * mm, "end": v(18.65, 19.96) * mm});
            skLineSegment(sketch, "E960", {"start": v(18.65, 19.96) * mm, "end": v(18.55, 20.46) * mm});
            skLineSegment(sketch, "E961", {"start": v(18.55, 20.46) * mm, "end": v(18.85, 20.97) * mm});
            skLineSegment(sketch, "E962", {"start": v(18.85, 20.97) * mm, "end": v(18.73, 21.1) * mm});
            skLineSegment(sketch, "E963", {"start": v(18.73, 21.1) * mm, "end": v(18.51, 21.01) * mm});
            skLineSegment(sketch, "E964", {"start": v(18.51, 21.01) * mm, "end": v(18.4, 20.62) * mm});
            skLineSegment(sketch, "E965", {"start": v(18.4, 20.62) * mm, "end": v(17.92, 20.24) * mm});
            skLineSegment(sketch, "E966", {"start": v(17.92, 20.24) * mm, "end": v(17.94, 20.08) * mm});
            skLineSegment(sketch, "E967", {"start": v(17.94, 20.08) * mm, "end": v(17.92, 19.75) * mm});
            skLineSegment(sketch, "E968", {"start": v(17.92, 19.75) * mm, "end": v(17.64, 19.73) * mm});
            skLineSegment(sketch, "E969", {"start": v(17.64, 19.73) * mm, "end": v(17.74, 19.27) * mm});
            skLineSegment(sketch, "E970", {"start": v(17.74, 19.27) * mm, "end": v(17.44, 18.26) * mm});
            skLineSegment(sketch, "E971", {"start": v(17.44, 18.26) * mm, "end": v(17.56, 17.5) * mm});
            skLineSegment(sketch, "E972", {"start": v(17.56, 17.5) * mm, "end": v(17.32, 16.92) * mm});
            skLineSegment(sketch, "E973", {"start": v(17.32, 16.92) * mm, "end": v(18.27, 15.02) * mm});
            skLineSegment(sketch, "E974", {"start": v(18.27, 15.02) * mm, "end": v(17.9, 13.34) * mm});
            skLineSegment(sketch, "E975", {"start": v(17.9, 13.34) * mm, "end": v(17.74, 12.87) * mm});
            skLineSegment(sketch, "E976", {"start": v(17.74, 12.87) * mm, "end": v(17.33, 12.38) * mm});
            skLineSegment(sketch, "E977", {"start": v(33.16, 9.15) * mm, "end": v(33.77, 9.59) * mm});
            skLineSegment(sketch, "E978", {"start": v(33.77, 9.59) * mm, "end": v(34.7, 9) * mm});
            skLineSegment(sketch, "E979", {"start": v(34.7, 9) * mm, "end": v(34.64, 8.42) * mm});
            skLineSegment(sketch, "E980", {"start": v(34.64, 8.42) * mm, "end": v(33.58, 8.9) * mm});
            skLineSegment(sketch, "E981", {"start": v(33.58, 8.9) * mm, "end": v(33.48, 8.25) * mm});
            skLineSegment(sketch, "E982", {"start": v(33.48, 8.25) * mm, "end": v(33.14, 7.63) * mm});
            skLineSegment(sketch, "E983", {"start": v(33.14, 7.63) * mm, "end": v(32.84, 7.4) * mm});
            skLineSegment(sketch, "E984", {"start": v(32.84, 7.4) * mm, "end": v(32.8, 7.15) * mm});
            skLineSegment(sketch, "E985", {"start": v(32.8, 7.15) * mm, "end": v(32.4, 7.06) * mm});
            skLineSegment(sketch, "E986", {"start": v(32.4, 7.06) * mm, "end": v(32.3, 6.18) * mm});
            skLineSegment(sketch, "E987", {"start": v(32.3, 6.18) * mm, "end": v(31.66, 6.49) * mm});
            skLineSegment(sketch, "E988", {"start": v(31.66, 6.49) * mm, "end": v(31.43, 6.48) * mm});
            skLineSegment(sketch, "E989", {"start": v(27.45, 3.14) * mm, "end": v(28.02, 2.6) * mm});
            skLineSegment(sketch, "E990", {"start": v(28.02, 2.6) * mm, "end": v(28.46, 2.5) * mm});
            skLineSegment(sketch, "E991", {"start": v(28.46, 2.5) * mm, "end": v(28.74, 2.87) * mm});
            skLineSegment(sketch, "E992", {"start": v(28.74, 2.87) * mm, "end": v(28.86, 2.68) * mm});
            skLineSegment(sketch, "E993", {"start": v(28.86, 2.68) * mm, "end": v(29.48, 2.77) * mm});
            skLineSegment(sketch, "E994", {"start": v(29.48, 2.77) * mm, "end": v(29.62, 3.3) * mm});
            skLineSegment(sketch, "E995", {"start": v(29.62, 3.3) * mm, "end": v(29.95, 3.24) * mm});
            skLineSegment(sketch, "E996", {"start": v(29.95, 3.24) * mm, "end": v(30.3, 3.46) * mm});
            skLineSegment(sketch, "E997", {"start": v(30.3, 3.46) * mm, "end": v(30.52, 3.43) * mm});
            skLineSegment(sketch, "E998", {"start": v(30.52, 3.43) * mm, "end": v(30.73, 3.9) * mm});
            skLineSegment(sketch, "E999", {"start": v(30.73, 3.9) * mm, "end": v(30.58, 4.07) * mm});
            skLineSegment(sketch, "E1000", {"start": v(30.58, 4.07) * mm, "end": v(31.44, 5.96) * mm});
            skLineSegment(sketch, "E1001", {"start": v(31.44, 5.96) * mm, "end": v(31.43, 6.48) * mm});
            skLineSegment(sketch, "E1002", {"start": v(38.55, 10.38) * mm, "end": v(38.43, 10.44) * mm});
            skLineSegment(sketch, "E1003", {"start": v(38.43, 10.44) * mm, "end": v(38.37, 10.27) * mm});
            skLineSegment(sketch, "E1004", {"start": v(38.37, 10.27) * mm, "end": v(38.66, 9.88) * mm});
            skLineSegment(sketch, "E1005", {"start": v(38.66, 9.88) * mm, "end": v(38.87, 9.81) * mm});
            skLineSegment(sketch, "E1006", {"start": v(38.87, 9.81) * mm, "end": v(39.3, 8.87) * mm});
            skLineSegment(sketch, "E1007", {"start": v(39.3, 8.87) * mm, "end": v(39.69, 8.59) * mm});
            skLineSegment(sketch, "E1008", {"start": v(39.69, 8.59) * mm, "end": v(39.82, 8.64) * mm});
            skLineSegment(sketch, "E1009", {"start": v(39.82, 8.64) * mm, "end": v(40.03, 7.9) * mm});
            skLineSegment(sketch, "E1010", {"start": v(40.03, 7.9) * mm, "end": v(40.04, 7.2) * mm});
            skLineSegment(sketch, "E1011", {"start": v(40.04, 7.2) * mm, "end": v(39.8, 6.36) * mm});
            skLineSegment(sketch, "E1012", {"start": v(39.8, 6.36) * mm, "end": v(39.48, 5.92) * mm});
            skLineSegment(sketch, "E1013", {"start": v(39.48, 5.92) * mm, "end": v(39.46, 5.04) * mm});
            skLineSegment(sketch, "E1014", {"start": v(39.46, 5.04) * mm, "end": v(39.18, 4.27) * mm});
            skLineSegment(sketch, "E1015", {"start": v(39.18, 4.27) * mm, "end": v(39.01, 4.27) * mm});
            skLineSegment(sketch, "E1016", {"start": v(39.01, 4.27) * mm, "end": v(38.88, 4.53) * mm});
            skLineSegment(sketch, "E1017", {"start": v(38.88, 4.53) * mm, "end": v(38.86, 5.39) * mm});
            skLineSegment(sketch, "E1018", {"start": v(38.86, 5.39) * mm, "end": v(39.15, 5.9) * mm});
            skLineSegment(sketch, "E1019", {"start": v(39.15, 5.9) * mm, "end": v(39.17, 6.42) * mm});
            skLineSegment(sketch, "E1020", {"start": v(39.17, 6.42) * mm, "end": v(38.97, 6.4) * mm});
            skLineSegment(sketch, "E1021", {"start": v(38.97, 6.4) * mm, "end": v(38.6, 7.05) * mm});
            skLineSegment(sketch, "E1022", {"start": v(38.6, 7.05) * mm, "end": v(38.51, 6.94) * mm});
            skLineSegment(sketch, "E1023", {"start": v(38.51, 6.94) * mm, "end": v(37.92, 6.95) * mm});
            skLineSegment(sketch, "E1024", {"start": v(37.92, 6.95) * mm, "end": v(37.73, 7.31) * mm});
            skLineSegment(sketch, "E1025", {"start": v(37.73, 7.31) * mm, "end": v(37.69, 7.7) * mm});
            skLineSegment(sketch, "E1026", {"start": v(37.69, 7.7) * mm, "end": v(37.92, 7.83) * mm});
            skLineSegment(sketch, "E1027", {"start": v(37.92, 7.83) * mm, "end": v(37.72, 8.11) * mm});
            skLineSegment(sketch, "E1028", {"start": v(37.72, 8.11) * mm, "end": v(37.58, 7.87) * mm});
            skLineSegment(sketch, "E1029", {"start": v(37.58, 7.87) * mm, "end": v(37.5, 8.2) * mm});
            skLineSegment(sketch, "E1030", {"start": v(37.5, 8.2) * mm, "end": v(37.77, 8.4) * mm});
            skLineSegment(sketch, "E1031", {"start": v(37.77, 8.4) * mm, "end": v(37.73, 8.95) * mm});
            skLineSegment(sketch, "E1032", {"start": v(37.73, 8.95) * mm, "end": v(37.5, 8.94) * mm});
            skLineSegment(sketch, "E1033", {"start": v(37.5, 8.94) * mm, "end": v(37.53, 9.33) * mm});
            skLineSegment(sketch, "E1034", {"start": v(37.53, 9.33) * mm, "end": v(37.84, 9.65) * mm});
            skLineSegment(sketch, "E1035", {"start": v(37.84, 9.65) * mm, "end": v(37.72, 9.82) * mm});
            skLineSegment(sketch, "E1036", {"start": v(37.72, 9.82) * mm, "end": v(37.32, 9.48) * mm});
            skLineSegment(sketch, "E1037", {"start": v(37.32, 9.48) * mm, "end": v(37.07, 8.98) * mm});
            skLineSegment(sketch, "E1038", {"start": v(37.07, 8.98) * mm, "end": v(37.3, 8.63) * mm});
            skLineSegment(sketch, "E1039", {"start": v(37.3, 8.63) * mm, "end": v(37.11, 8.07) * mm});
            skLineSegment(sketch, "E1040", {"start": v(37.11, 8.07) * mm, "end": v(37.37, 7.41) * mm});
            skLineSegment(sketch, "E1041", {"start": v(37.37, 7.41) * mm, "end": v(37.59, 7.22) * mm});
            skLineSegment(sketch, "E1042", {"start": v(37.59, 7.22) * mm, "end": v(37.56, 7.04) * mm});
            skLineSegment(sketch, "E1043", {"start": v(37.56, 7.04) * mm, "end": v(37.7, 6.59) * mm});
            skLineSegment(sketch, "E1044", {"start": v(37.7, 6.59) * mm, "end": v(37.1, 6.64) * mm});
            skLineSegment(sketch, "E1045", {"start": v(37.1, 6.64) * mm, "end": v(36.64, 6.67) * mm});
            skLineSegment(sketch, "E1046", {"start": v(36.64, 6.67) * mm, "end": v(36.04, 6.78) * mm});
            skLineSegment(sketch, "E1047", {"start": v(36.04, 6.78) * mm, "end": v(35.95, 7.22) * mm});
            skLineSegment(sketch, "E1048", {"start": v(35.95, 7.22) * mm, "end": v(36.16, 7.48) * mm});
            skLineSegment(sketch, "E1049", {"start": v(36.16, 7.48) * mm, "end": v(36.2, 7.83) * mm});
            skLineSegment(sketch, "E1050", {"start": v(36.2, 7.83) * mm, "end": v(35.86, 8.25) * mm});
            skLineSegment(sketch, "E1051", {"start": v(35.86, 8.25) * mm, "end": v(35.19, 8.42) * mm});
            skLineSegment(sketch, "E1052", {"start": v(35.19, 8.42) * mm, "end": v(35.21, 8.74) * mm});
            skLineSegment(sketch, "E1053", {"start": v(35.21, 8.74) * mm, "end": v(34.7, 9) * mm});
            skLineSegment(sketch, "E1054", {"start": v(36.64, 6.67) * mm, "end": v(36.82, 6.48) * mm});
            skLineSegment(sketch, "E1055", {"start": v(36.82, 6.48) * mm, "end": v(37.46, 6.43) * mm});
            skLineSegment(sketch, "E1056", {"start": v(37.46, 6.43) * mm, "end": v(37.66, 6.16) * mm});
            skLineSegment(sketch, "E1057", {"start": v(37.66, 6.16) * mm, "end": v(38.01, 6.17) * mm});
            skLineSegment(sketch, "E1058", {"start": v(38.01, 6.17) * mm, "end": v(38.16, 6) * mm});
            skLineSegment(sketch, "E1059", {"start": v(38.16, 6) * mm, "end": v(38.13, 5.48) * mm});
            skLineSegment(sketch, "E1060", {"start": v(38.13, 5.48) * mm, "end": v(38.23, 5.42) * mm});
            skLineSegment(sketch, "E1061", {"start": v(38.23, 5.42) * mm, "end": v(38.23, 5.14) * mm});
            skLineSegment(sketch, "E1062", {"start": v(38.23, 5.14) * mm, "end": v(38.42, 4.88) * mm});
            skLineSegment(sketch, "E1063", {"start": v(38.42, 4.88) * mm, "end": v(38.41, 4.7) * mm});
            skLineSegment(sketch, "E1064", {"start": v(38.41, 4.7) * mm, "end": v(38, 4.83) * mm});
            skLineSegment(sketch, "E1065", {"start": v(38, 4.83) * mm, "end": v(38, 4.73) * mm});
            skLineSegment(sketch, "E1066", {"start": v(38, 4.73) * mm, "end": v(38.22, 4.57) * mm});
            skLineSegment(sketch, "E1067", {"start": v(38.22, 4.57) * mm, "end": v(38.22, 4.44) * mm});
            skLineSegment(sketch, "E1068", {"start": v(38.22, 4.44) * mm, "end": v(38.53, 4.17) * mm});
            skLineSegment(sketch, "E1069", {"start": v(38.53, 4.17) * mm, "end": v(38.6, 3.82) * mm});
            skLineSegment(sketch, "E1070", {"start": v(38.6, 3.82) * mm, "end": v(38.3, 3.71) * mm});
            skLineSegment(sketch, "E1071", {"start": v(38.3, 3.71) * mm, "end": v(38.3, 3.6) * mm});
            skLineSegment(sketch, "E1072", {"start": v(38.3, 3.6) * mm, "end": v(39.12, 3.78) * mm});
            skLineSegment(sketch, "E1073", {"start": v(39.12, 3.78) * mm, "end": v(39.47, 2.95) * mm});
            skLineSegment(sketch, "E1074", {"start": v(39.47, 2.95) * mm, "end": v(40.52, 1.25) * mm});
            skLineSegment(sketch, "E1075", {"start": v(40.52, 1.25) * mm, "end": v(40.12, 1.25) * mm});
            skLineSegment(sketch, "E1076", {"start": v(26.15, -3.3) * mm, "end": v(27.83, -2.53) * mm});
            skLineSegment(sketch, "E1077", {"start": v(27.83, -2.53) * mm, "end": v(30.43, -2.37) * mm});
            skLineSegment(sketch, "E1078", {"start": v(30.43, -2.37) * mm, "end": v(30.72, -2.7) * mm});
            skLineSegment(sketch, "E1079", {"start": v(30.72, -2.7) * mm, "end": v(30.8, -2.96) * mm});
            skLineSegment(sketch, "E1080", {"start": v(30.8, -2.96) * mm, "end": v(32.94, -2.77) * mm});
            skLineSegment(sketch, "E1081", {"start": v(32.94, -2.77) * mm, "end": v(35.51, -4.54) * mm});
            skLineSegment(sketch, "E1082", {"start": v(35.51, -4.54) * mm, "end": v(36.07, -4.38) * mm});
            skLineSegment(sketch, "E1083", {"start": v(36.07, -4.38) * mm, "end": v(36.8, -4.32) * mm});
            skLineSegment(sketch, "E1084", {"start": v(36.8, -4.32) * mm, "end": v(36.98, -3.28) * mm});
            skLineSegment(sketch, "E1085", {"start": v(36.98, -3.28) * mm, "end": v(38.16, -2.16) * mm});
            skLineSegment(sketch, "E1086", {"start": v(38.16, -2.16) * mm, "end": v(39, -1.8) * mm});
            skLineSegment(sketch, "E1087", {"start": v(39, -1.8) * mm, "end": v(39.29, -1.89) * mm});
            skLineSegment(sketch, "E1088", {"start": v(39.29, -1.89) * mm, "end": v(39.8, -1.06) * mm});
            skLineSegment(sketch, "E1089", {"start": v(39.8, -1.06) * mm, "end": v(39.45, -1.27) * mm});
            skLineSegment(sketch, "E1090", {"start": v(39.45, -1.27) * mm, "end": v(39.31, -1.09) * mm});
            skLineSegment(sketch, "E1091", {"start": v(39.31, -1.09) * mm, "end": v(38.86, -1.11) * mm});
            skLineSegment(sketch, "E1092", {"start": v(38.86, -1.11) * mm, "end": v(39.12, -0.4) * mm});
            skLineSegment(sketch, "E1093", {"start": v(39.12, -0.4) * mm, "end": v(38.83, -0.28) * mm});
            skLineSegment(sketch, "E1094", {"start": v(38.83, -0.28) * mm, "end": v(38.7, 0.01) * mm});
            skLineSegment(sketch, "E1095", {"start": v(38.7, 0.01) * mm, "end": v(39.26, -0.26) * mm});
            skLineSegment(sketch, "E1096", {"start": v(39.26, -0.26) * mm, "end": v(39.8, -0.1) * mm});
            skLineSegment(sketch, "E1097", {"start": v(39.8, -0.1) * mm, "end": v(40, 0.57) * mm});
            skLineSegment(sketch, "E1098", {"start": v(40, 0.57) * mm, "end": v(40.28, 0.7) * mm});
            skLineSegment(sketch, "E1099", {"start": v(40.28, 0.7) * mm, "end": v(40.12, 1.25) * mm});
            skLineSegment(sketch, "E1100", {"start": v(26.15, -3.3) * mm, "end": v(26.26, -3.54) * mm});
            skLineSegment(sketch, "E1101", {"start": v(26.26, -3.54) * mm, "end": v(25.94, -3.73) * mm});
            skLineSegment(sketch, "E1102", {"start": v(25.94, -3.73) * mm, "end": v(25.85, -4.13) * mm});
            skLineSegment(sketch, "E1103", {"start": v(25.85, -4.13) * mm, "end": v(26.52, -4.53) * mm});
            skLineSegment(sketch, "E1104", {"start": v(26.52, -4.53) * mm, "end": v(26.82, -4.47) * mm});
            skLineSegment(sketch, "E1105", {"start": v(26.82, -4.47) * mm, "end": v(27.6, -5.68) * mm});
            skLineSegment(sketch, "E1106", {"start": v(27.6, -5.68) * mm, "end": v(28.36, -6.12) * mm});
            skLineSegment(sketch, "E1107", {"start": v(28.36, -6.12) * mm, "end": v(28.5, -6.42) * mm});
            skLineSegment(sketch, "E1108", {"start": v(28.5, -6.42) * mm, "end": v(29.1, -6.74) * mm});
            skLineSegment(sketch, "E1109", {"start": v(29.1, -6.74) * mm, "end": v(29.57, -7.32) * mm});
            skLineSegment(sketch, "E1110", {"start": v(29.57, -7.32) * mm, "end": v(30.02, -7.55) * mm});
            skLineSegment(sketch, "E1111", {"start": v(30.02, -7.55) * mm, "end": v(30.5, -8.75) * mm});
            skLineSegment(sketch, "E1112", {"start": v(30.5, -8.75) * mm, "end": v(30.72, -8.75) * mm});
            skLineSegment(sketch, "E1113", {"start": v(30.72, -8.75) * mm, "end": v(31.08, -9.2) * mm});
            skLineSegment(sketch, "E1114", {"start": v(31.08, -9.2) * mm, "end": v(31.19, -9.65) * mm});
            skLineSegment(sketch, "E1115", {"start": v(31.19, -9.65) * mm, "end": v(31.8, -9.9) * mm});
            skLineSegment(sketch, "E1116", {"start": v(31.8, -9.9) * mm, "end": v(31.73, -9.68) * mm});
            skLineSegment(sketch, "E1117", {"start": v(31.73, -9.68) * mm, "end": v(32.5, -9) * mm});
            skLineSegment(sketch, "E1118", {"start": v(32.5, -9) * mm, "end": v(32.34, -8.64) * mm});
            skLineSegment(sketch, "E1119", {"start": v(32.34, -8.64) * mm, "end": v(32.75, -8.62) * mm});
            skLineSegment(sketch, "E1120", {"start": v(32.75, -8.62) * mm, "end": v(34.08, -7.1) * mm});
            skLineSegment(sketch, "E1121", {"start": v(34.08, -7.1) * mm, "end": v(34.28, -7.02) * mm});
            skLineSegment(sketch, "E1122", {"start": v(34.28, -7.02) * mm, "end": v(34.7, -6.53) * mm});
            skLineSegment(sketch, "E1123", {"start": v(34.7, -6.53) * mm, "end": v(34.73, -5.86) * mm});
            skLineSegment(sketch, "E1124", {"start": v(34.73, -5.86) * mm, "end": v(35.23, -4.94) * mm});
            skLineSegment(sketch, "E1125", {"start": v(35.23, -4.94) * mm, "end": v(35.51, -4.54) * mm});
            skLineSegment(sketch, "E1126", {"start": v(31.8, -9.9) * mm, "end": v(31.44, -10.7) * mm});
            skLineSegment(sketch, "E1127", {"start": v(31.44, -10.7) * mm, "end": v(31.47, -10.88) * mm});
            skLineSegment(sketch, "E1128", {"start": v(31.47, -10.88) * mm, "end": v(31.32, -11.38) * mm});
            skLineSegment(sketch, "E1129", {"start": v(31.32, -11.38) * mm, "end": v(30.99, -12.4) * mm});
            skLineSegment(sketch, "E1130", {"start": v(30.99, -12.4) * mm, "end": v(31.05, -13.22) * mm});
            skLineSegment(sketch, "E1131", {"start": v(31.05, -13.22) * mm, "end": v(29.97, -13.13) * mm});
            skLineSegment(sketch, "E1132", {"start": v(29.97, -13.13) * mm, "end": v(29.8, -13.32) * mm});
            skLineSegment(sketch, "E1133", {"start": v(29.8, -13.32) * mm, "end": v(29.88, -13.72) * mm});
            skLineSegment(sketch, "E1134", {"start": v(29.88, -13.72) * mm, "end": v(29.92, -14.22) * mm});
            skLineSegment(sketch, "E1135", {"start": v(29.92, -14.22) * mm, "end": v(29.61, -14.2) * mm});
            skLineSegment(sketch, "E1136", {"start": v(29.61, -14.2) * mm, "end": v(29.57, -13.82) * mm});
            skLineSegment(sketch, "E1137", {"start": v(28.8, -17.36) * mm, "end": v(29.37, -18.15) * mm});
            skLineSegment(sketch, "E1138", {"start": v(29.37, -18.15) * mm, "end": v(29.34, -19.33) * mm});
            skLineSegment(sketch, "E1139", {"start": v(29.34, -19.33) * mm, "end": v(29.11, -19.64) * mm});
            skLineSegment(sketch, "E1140", {"start": v(29.11, -19.64) * mm, "end": v(29.54, -20.91) * mm});
            skLineSegment(sketch, "E1141", {"start": v(29.54, -20.91) * mm, "end": v(29.73, -20.58) * mm});
            skLineSegment(sketch, "E1142", {"start": v(29.73, -20.58) * mm, "end": v(29.4, -20.3) * mm});
            skLineSegment(sketch, "E1143", {"start": v(29.4, -20.3) * mm, "end": v(30.19, -20.32) * mm});
            skLineSegment(sketch, "E1144", {"start": v(30.19, -20.32) * mm, "end": v(29.56, -21.28) * mm});
            skLineSegment(sketch, "E1145", {"start": v(29.56, -21.28) * mm, "end": v(30.21, -22.1) * mm});
            skLineSegment(sketch, "E1146", {"start": v(30.21, -22.1) * mm, "end": v(30.67, -22.72) * mm});
            skLineSegment(sketch, "E1147", {"start": v(30.67, -22.72) * mm, "end": v(31.03, -23.65) * mm});
            skLineSegment(sketch, "E1148", {"start": v(31.03, -23.65) * mm, "end": v(31.26, -23.8) * mm});
            skLineSegment(sketch, "E1149", {"start": v(31.26, -23.8) * mm, "end": v(31.48, -23.6) * mm});
            skLineSegment(sketch, "E1150", {"start": v(31.48, -23.6) * mm, "end": v(31.88, -23.9) * mm});
            skLineSegment(sketch, "E1151", {"start": v(31.88, -23.9) * mm, "end": v(31.96, -24.27) * mm});
            skLineSegment(sketch, "E1152", {"start": v(31.96, -24.27) * mm, "end": v(32.3, -24.8) * mm});
            skLineSegment(sketch, "E1153", {"start": v(32.3, -24.8) * mm, "end": v(32.5, -24.78) * mm});
            skLineSegment(sketch, "E1154", {"start": v(32.5, -24.78) * mm, "end": v(32.87, -24.84) * mm});
            skLineSegment(sketch, "E1155", {"start": v(32.87, -24.84) * mm, "end": v(33.29, -25.18) * mm});
            skLineSegment(sketch, "E1156", {"start": v(33.29, -25.18) * mm, "end": v(33.63, -25.63) * mm});
            skLineSegment(sketch, "E1157", {"start": v(33.63, -25.63) * mm, "end": v(33.8, -26.45) * mm});
            skLineSegment(sketch, "E1158", {"start": v(33.8, -26.45) * mm, "end": v(34, -26.61) * mm});
            skLineSegment(sketch, "E1159", {"start": v(34, -26.61) * mm, "end": v(34.3, -26.5) * mm});
            skLineSegment(sketch, "E1160", {"start": v(34.3, -26.5) * mm, "end": v(34.48, -26.16) * mm});
            skLineSegment(sketch, "E1161", {"start": v(34.48, -26.16) * mm, "end": v(34.7, -26.22) * mm});
            skLineSegment(sketch, "E1162", {"start": v(34.7, -26.22) * mm, "end": v(35.07, -26.16) * mm});
            skLineSegment(sketch, "E1163", {"start": v(35.07, -26.16) * mm, "end": v(35.55, -25.82) * mm});
            skLineSegment(sketch, "E1164", {"start": v(35.55, -25.82) * mm, "end": v(35.46, -25.4) * mm});
            skLineSegment(sketch, "E1165", {"start": v(35.46, -25.4) * mm, "end": v(35.46, -25.15) * mm});
            skLineSegment(sketch, "E1166", {"start": v(35.46, -25.15) * mm, "end": v(35.38, -24.78) * mm});
            skLineSegment(sketch, "E1167", {"start": v(35.38, -24.78) * mm, "end": v(35.8, -24.47) * mm});
            skLineSegment(sketch, "E1168", {"start": v(35.8, -24.47) * mm, "end": v(35.8, -24.02) * mm});
            skLineSegment(sketch, "E1169", {"start": v(35.8, -24.02) * mm, "end": v(35.66, -22.07) * mm});
            skLineSegment(sketch, "E1170", {"start": v(35.66, -22.07) * mm, "end": v(34.45, -19.81) * mm});
            skLineSegment(sketch, "E1171", {"start": v(34.45, -19.81) * mm, "end": v(33.91, -19.45) * mm});
            skLineSegment(sketch, "E1172", {"start": v(33.91, -19.45) * mm, "end": v(33.69, -18.66) * mm});
            skLineSegment(sketch, "E1173", {"start": v(33.69, -18.66) * mm, "end": v(33.85, -18.37) * mm});
            skLineSegment(sketch, "E1174", {"start": v(33.85, -18.37) * mm, "end": v(33.66, -17.9) * mm});
            skLineSegment(sketch, "E1175", {"start": v(33.66, -17.9) * mm, "end": v(32.92, -17.19) * mm});
            skLineSegment(sketch, "E1176", {"start": v(32.92, -17.19) * mm, "end": v(32.02, -15.8) * mm});
            skLineSegment(sketch, "E1177", {"start": v(32.02, -15.8) * mm, "end": v(31.31, -14.17) * mm});
            skLineSegment(sketch, "E1178", {"start": v(31.31, -14.17) * mm, "end": v(31.05, -13.22) * mm});
            skLineSegment(sketch, "E1179", {"start": v(-34.84, -14.17) * mm, "end": v(-35.81, -13.68) * mm});
            skLineSegment(sketch, "E1180", {"start": v(-35.81, -13.68) * mm, "end": v(-36.16, -13.85) * mm});
            skLineSegment(sketch, "E1181", {"start": v(-36.16, -13.85) * mm, "end": v(-36.86, -13.55) * mm});
            skLineSegment(sketch, "E1182", {"start": v(-36.86, -13.55) * mm, "end": v(-36.95, -13.85) * mm});
            skLineSegment(sketch, "E1183", {"start": v(-36.95, -13.85) * mm, "end": v(-37.65, -13.2) * mm});
            skLineSegment(sketch, "E1184", {"start": v(-37.65, -13.2) * mm, "end": v(-38.48, -13.15) * mm});
            skLineSegment(sketch, "E1185", {"start": v(-38.48, -13.15) * mm, "end": v(-38.73, -13.03) * mm});
            skLineSegment(sketch, "E1186", {"start": v(-38.73, -13.03) * mm, "end": v(-38.74, -12.54) * mm});
            skLineSegment(sketch, "E1187", {"start": v(-38.74, -12.54) * mm, "end": v(-39.15, -12.5) * mm});
            skLineSegment(sketch, "E1188", {"start": v(-39.15, -12.5) * mm, "end": v(-39.3, -12.75) * mm});
            skLineSegment(sketch, "E1189", {"start": v(-39.3, -12.75) * mm, "end": v(-39.35, -12.45) * mm});
            skLineSegment(sketch, "E1190", {"start": v(-39.35, -12.45) * mm, "end": v(-40.07, -11.94) * mm});
            skLineSegment(sketch, "E1191", {"start": v(-40.07, -11.94) * mm, "end": v(-40.39, -12.28) * mm});
            skLineSegment(sketch, "E1192", {"start": v(-40.39, -12.28) * mm, "end": v(-40.86, -12.32) * mm});
            skLineSegment(sketch, "E1193", {"start": v(-40.86, -12.32) * mm, "end": v(-41.06, -12.22) * mm});
            skLineSegment(sketch, "E1194", {"start": v(-41.06, -12.22) * mm, "end": v(-41.84, -12.57) * mm});
            skLineSegment(sketch, "E1195", {"start": v(-41.84, -12.57) * mm, "end": v(-42.1, -12.37) * mm});
            skLineSegment(sketch, "E1196", {"start": v(-42.1, -12.37) * mm, "end": v(-42.4, -12.7) * mm});
            skLineSegment(sketch, "E1197", {"start": v(-42.4, -12.7) * mm, "end": v(-42.5, -13.03) * mm});
            skLineSegment(sketch, "E1198", {"start": v(-42.5, -13.03) * mm, "end": v(-42.95, -13.4) * mm});
            skLineSegment(sketch, "E1199", {"start": v(-42.95, -13.4) * mm, "end": v(-43.4, -13.4) * mm});
            skLineSegment(sketch, "E1200", {"start": v(-43.4, -13.4) * mm, "end": v(-43.48, -13.4) * mm});
            skLineSegment(sketch, "E1201", {"start": v(-43.48, -13.4) * mm, "end": v(-43.94, -13.3) * mm});
            skLineSegment(sketch, "E1202", {"start": v(-43.94, -13.3) * mm, "end": v(-44.27, -13.56) * mm});
            skLineSegment(sketch, "E1203", {"start": v(-44.27, -13.56) * mm, "end": v(-43.68, -14.58) * mm});
            skLineSegment(sketch, "E1204", {"start": v(-43.68, -14.58) * mm, "end": v(-43.68, -15.28) * mm});
            skLineSegment(sketch, "E1205", {"start": v(-43.68, -15.28) * mm, "end": v(-43.18, -15.5) * mm});
            skLineSegment(sketch, "E1206", {"start": v(-43.18, -15.5) * mm, "end": v(-43.36, -15.62) * mm});
            skLineSegment(sketch, "E1207", {"start": v(-43.36, -15.62) * mm, "end": v(-43, -16.45) * mm});
            skLineSegment(sketch, "E1208", {"start": v(-43, -16.45) * mm, "end": v(-43.2, -16.6) * mm});
            skLineSegment(sketch, "E1209", {"start": v(-43.2, -16.6) * mm, "end": v(-44.03, -16.24) * mm});
            skLineSegment(sketch, "E1210", {"start": v(-44.03, -16.24) * mm, "end": v(-43.83, -15.8) * mm});
            skLineSegment(sketch, "E1211", {"start": v(-43.83, -15.8) * mm, "end": v(-44.05, -15.63) * mm});
            skLineSegment(sketch, "E1212", {"start": v(-44.05, -15.63) * mm, "end": v(-44.66, -15.7) * mm});
            skLineSegment(sketch, "E1213", {"start": v(-44.66, -15.7) * mm, "end": v(-44.66, -15.9) * mm});
            skLineSegment(sketch, "E1214", {"start": v(-44.66, -15.9) * mm, "end": v(-44.78, -15.9) * mm});
            skLineSegment(sketch, "E1215", {"start": v(-44.78, -15.9) * mm, "end": v(-44.87, -15.81) * mm});
            skLineSegment(sketch, "E1216", {"start": v(-44.87, -15.81) * mm, "end": v(-45.78, -15.83) * mm});
            skLineSegment(sketch, "E1217", {"start": v(-45.78, -15.83) * mm, "end": v(-45.87, -16.01) * mm});
            skLineSegment(sketch, "E1218", {"start": v(-45.87, -16.01) * mm, "end": v(-45.5, -16.5) * mm});
            skLineSegment(sketch, "E1219", {"start": v(-45.5, -16.5) * mm, "end": v(-45.6, -17.19) * mm});
            skLineSegment(sketch, "E1220", {"start": v(-45.6, -17.19) * mm, "end": v(-45.17, -17.67) * mm});
            skLineSegment(sketch, "E1221", {"start": v(-45.17, -17.67) * mm, "end": v(-44.69, -17.64) * mm});
            skLineSegment(sketch, "E1222", {"start": v(-44.69, -17.64) * mm, "end": v(-44.1, -17.9) * mm});
            skLineSegment(sketch, "E1223", {"start": v(-44.1, -17.9) * mm, "end": v(-43.44, -17.75) * mm});
            skLineSegment(sketch, "E1224", {"start": v(-43.44, -17.75) * mm, "end": v(-43.31, -17.95) * mm});
            skLineSegment(sketch, "E1225", {"start": v(-43.31, -17.95) * mm, "end": v(-43.57, -18.9) * mm});
            skLineSegment(sketch, "E1226", {"start": v(-34.84, -14.17) * mm, "end": v(-34.84, -23.66) * mm});
            skLineSegment(sketch, "E1227", {"start": v(-34.84, -23.66) * mm, "end": v(-34.7, -23.92) * mm});
            skLineSegment(sketch, "E1228", {"start": v(-34.7, -23.92) * mm, "end": v(-34.43, -23.86) * mm});
            skLineSegment(sketch, "E1229", {"start": v(-34.43, -23.86) * mm, "end": v(-34.3, -23.86) * mm});
            skLineSegment(sketch, "E1230", {"start": v(-34.3, -23.86) * mm, "end": v(-34.1, -23.72) * mm});
            skLineSegment(sketch, "E1231", {"start": v(-34.1, -23.72) * mm, "end": v(-33.93, -23.77) * mm});
            skLineSegment(sketch, "E1232", {"start": v(-33.93, -23.77) * mm, "end": v(-33.9, -24.08) * mm});
            skLineSegment(sketch, "E1233", {"start": v(-33.9, -24.08) * mm, "end": v(-33.2, -24.73) * mm});
            skLineSegment(sketch, "E1234", {"start": v(-33.2, -24.73) * mm, "end": v(-33.04, -25.12) * mm});
            skLineSegment(sketch, "E1235", {"start": v(-33.04, -25.12) * mm, "end": v(-32.5, -24.86) * mm});
            skLineSegment(sketch, "E1236", {"start": v(-32.5, -24.86) * mm, "end": v(-32.48, -24.44) * mm});
            skLineSegment(sketch, "E1237", {"start": v(-32.48, -24.44) * mm, "end": v(-32.21, -24.3) * mm});
            skLineSegment(sketch, "E1238", {"start": v(-31.86, -24.4) * mm, "end": v(-31.72, -24.8) * mm});
            skLineSegment(sketch, "E1239", {"start": v(-31.72, -24.8) * mm, "end": v(-31.45, -24.8) * mm});
            skLineSegment(sketch, "E1240", {"start": v(-31.45, -24.8) * mm, "end": v(-31.4, -25.23) * mm});
            skLineSegment(sketch, "E1241", {"start": v(-32.21, -24.3) * mm, "end": v(-31.86, -24.4) * mm});
            skLineSegment(sketch, "E1242", {"start": v(-31.4, -25.23) * mm, "end": v(-31, -25.23) * mm});
            skLineSegment(sketch, "E1243", {"start": v(-31, -25.23) * mm, "end": v(-30.56, -26.08) * mm});
            skLineSegment(sketch, "E1244", {"start": v(-30.56, -26.08) * mm, "end": v(-30.05, -26.65) * mm});
            skLineSegment(sketch, "E1245", {"start": v(-30.05, -26.65) * mm, "end": v(-29.9, -27.13) * mm});
            skLineSegment(sketch, "E1246", {"start": v(-29.9, -27.13) * mm, "end": v(-28.73, -27.5) * mm});
            skLineSegment(sketch, "E1247", {"start": v(-28.73, -27.5) * mm, "end": v(-28.6, -28.24) * mm});
            skLineSegment(sketch, "E1248", {"start": v(-28.6, -28.24) * mm, "end": v(-28.87, -28.93) * mm});
            skLineSegment(sketch, "E1249", {"start": v(-28.87, -28.93) * mm, "end": v(-29.01, -28.84) * mm});
            skLineSegment(sketch, "E1250", {"start": v(-29.01, -28.84) * mm, "end": v(-29.12, -28.56) * mm});
            skLineSegment(sketch, "E1251", {"start": v(-29.12, -28.56) * mm, "end": v(-29.62, -28.26) * mm});
            skLineSegment(sketch, "E1252", {"start": v(-29.62, -28.26) * mm, "end": v(-29.77, -28.32) * mm});
            skLineSegment(sketch, "E1253", {"start": v(-29.77, -28.32) * mm, "end": v(-29.61, -28.54) * mm});
            skLineSegment(sketch, "E1254", {"start": v(-29.61, -28.54) * mm, "end": v(-29.61, -29.11) * mm});
            skLineSegment(sketch, "E1255", {"start": v(-29.61, -29.11) * mm, "end": v(-29.9, -28.87) * mm});
            skLineSegment(sketch, "E1256", {"start": v(-29.9, -28.87) * mm, "end": v(-30.19, -28.66) * mm});
            skLineSegment(sketch, "E1257", {"start": v(-30.19, -28.66) * mm, "end": v(-29.96, -29.08) * mm});
            skLineSegment(sketch, "E1258", {"start": v(-29.96, -29.08) * mm, "end": v(-30.06, -29.2) * mm});
            skLineSegment(sketch, "E1259", {"start": v(-30.06, -29.2) * mm, "end": v(-30.5, -28.46) * mm});
            skLineSegment(sketch, "E1260", {"start": v(-30.5, -28.46) * mm, "end": v(-30.61, -28.57) * mm});
            skLineSegment(sketch, "E1261", {"start": v(-30.53, -28.2) * mm, "end": v(-30.68, -28.08) * mm});
            skLineSegment(sketch, "E1262", {"start": v(-30.68, -28.08) * mm, "end": v(-30.68, -27.52) * mm});
            skLineSegment(sketch, "E1263", {"start": v(-30.68, -27.52) * mm, "end": v(-30.88, -27.88) * mm});
            skLineSegment(sketch, "E1264", {"start": v(-30.88, -27.88) * mm, "end": v(-31.06, -28) * mm});
            skLineSegment(sketch, "E1265", {"start": v(-31.06, -28) * mm, "end": v(-31.18, -27.13) * mm});
            skLineSegment(sketch, "E1266", {"start": v(-31.18, -27.13) * mm, "end": v(-31.3, -27.06) * mm});
            skLineSegment(sketch, "E1267", {"start": v(-31.3, -27.06) * mm, "end": v(-31.3, -27.73) * mm});
            skLineSegment(sketch, "E1268", {"start": v(-31.3, -27.73) * mm, "end": v(-31.79, -27.02) * mm});
            skLineSegment(sketch, "E1269", {"start": v(-31.79, -27.02) * mm, "end": v(-32.1, -26.96) * mm});
            skLineSegment(sketch, "E1270", {"start": v(-32.1, -26.96) * mm, "end": v(-32.12, -26.56) * mm});
            skLineSegment(sketch, "E1271", {"start": v(-32.12, -26.56) * mm, "end": v(-32.28, -26.24) * mm});
            skLineSegment(sketch, "E1272", {"start": v(-32.28, -26.24) * mm, "end": v(-32.53, -26.06) * mm});
            skLineSegment(sketch, "E1273", {"start": v(-32.53, -26.06) * mm, "end": v(-32.53, -25.85) * mm});
            skLineSegment(sketch, "E1274", {"start": v(-32.53, -25.85) * mm, "end": v(-32.2, -25.7) * mm});
            skLineSegment(sketch, "E1275", {"start": v(-32.2, -25.7) * mm, "end": v(-32.32, -25.61) * mm});
            skLineSegment(sketch, "E1276", {"start": v(-32.32, -25.61) * mm, "end": v(-32.55, -25.75) * mm});
            skLineSegment(sketch, "E1277", {"start": v(-32.55, -25.75) * mm, "end": v(-33.03, -25.4) * mm});
            skLineSegment(sketch, "E1278", {"start": v(-33.03, -25.4) * mm, "end": v(-33.16, -25.22) * mm});
            skLineSegment(sketch, "E1279", {"start": v(-33.16, -25.22) * mm, "end": v(-34.24, -24.6) * mm});
            skLineSegment(sketch, "E1280", {"start": v(-34.24, -24.6) * mm, "end": v(-34.06, -24.28) * mm});
            skLineSegment(sketch, "E1281", {"start": v(-34.06, -24.28) * mm, "end": v(-34.05, -23.96) * mm});
            skLineSegment(sketch, "E1282", {"start": v(-34.05, -23.96) * mm, "end": v(-34.52, -24.3) * mm});
            skLineSegment(sketch, "E1283", {"start": v(-34.52, -24.3) * mm, "end": v(-35.6, -23.92) * mm});
            skLineSegment(sketch, "E1284", {"start": v(-35.6, -23.92) * mm, "end": v(-36.22, -23.9) * mm});
            skLineSegment(sketch, "E1285", {"start": v(-36.22, -23.9) * mm, "end": v(-36.3, -23.98) * mm});
            skLineSegment(sketch, "E1286", {"start": v(-36.3, -23.98) * mm, "end": v(-36.96, -23.55) * mm});
            skLineSegment(sketch, "E1287", {"start": v(-36.96, -23.55) * mm, "end": v(-37.17, -23.53) * mm});
            skLineSegment(sketch, "E1288", {"start": v(-37.17, -23.53) * mm, "end": v(-37.52, -22.9) * mm});
            skLineSegment(sketch, "E1289", {"start": v(-37.52, -22.9) * mm, "end": v(-37.85, -22.89) * mm});
            skLineSegment(sketch, "E1290", {"start": v(-37.85, -22.89) * mm, "end": v(-38.34, -23.07) * mm});
            skLineSegment(sketch, "E1291", {"start": v(-38.34, -23.07) * mm, "end": v(-38.33, -23.48) * mm});
            skLineSegment(sketch, "E1292", {"start": v(-38.33, -23.48) * mm, "end": v(-38.16, -23.5) * mm});
            skLineSegment(sketch, "E1293", {"start": v(-38.16, -23.5) * mm, "end": v(-38.21, -23.74) * mm});
            skLineSegment(sketch, "E1294", {"start": v(-38.21, -23.74) * mm, "end": v(-38.39, -23.92) * mm});
            skLineSegment(sketch, "E1295", {"start": v(-38.39, -23.92) * mm, "end": v(-38.55, -23.78) * mm});
            skLineSegment(sketch, "E1296", {"start": v(-38.55, -23.78) * mm, "end": v(-38.7, -23.91) * mm});
            skLineSegment(sketch, "E1297", {"start": v(-38.7, -23.91) * mm, "end": v(-38.97, -23.7) * mm});
            skLineSegment(sketch, "E1298", {"start": v(-38.97, -23.7) * mm, "end": v(-39.33, -23.95) * mm});
            skLineSegment(sketch, "E1299", {"start": v(-39.33, -23.95) * mm, "end": v(-39.86, -24.4) * mm});
            skLineSegment(sketch, "E1300", {"start": v(-39.86, -24.4) * mm, "end": v(-40.47, -24.4) * mm});
            skLineSegment(sketch, "E1301", {"start": v(-40.47, -24.4) * mm, "end": v(-40.5, -24.18) * mm});
            skLineSegment(sketch, "E1302", {"start": v(-40.5, -24.18) * mm, "end": v(-40.1, -24.12) * mm});
            skLineSegment(sketch, "E1303", {"start": v(-40.1, -24.12) * mm, "end": v(-40.07, -23.94) * mm});
            skLineSegment(sketch, "E1304", {"start": v(-40.07, -23.94) * mm, "end": v(-40.38, -23.87) * mm});
            skLineSegment(sketch, "E1305", {"start": v(-40.38, -23.87) * mm, "end": v(-39.83, -22.83) * mm});
            skLineSegment(sketch, "E1306", {"start": v(-39.83, -22.83) * mm, "end": v(-39.5, -22.66) * mm});
            skLineSegment(sketch, "E1307", {"start": v(-39.5, -22.66) * mm, "end": v(-39.35, -22.8) * mm});
            skLineSegment(sketch, "E1308", {"start": v(-39.35, -22.8) * mm, "end": v(-39.04, -22.81) * mm});
            skLineSegment(sketch, "E1309", {"start": v(-39.04, -22.81) * mm, "end": v(-39.2, -22.5) * mm});
            skLineSegment(sketch, "E1310", {"start": v(-39.2, -22.5) * mm, "end": v(-39.57, -22.41) * mm});
            skLineSegment(sketch, "E1311", {"start": v(-39.57, -22.41) * mm, "end": v(-40.2, -22.74) * mm});
            skLineSegment(sketch, "E1312", {"start": v(-40.2, -22.74) * mm, "end": v(-40.73, -23.68) * mm});
            skLineSegment(sketch, "E1313", {"start": v(-40.73, -23.68) * mm, "end": v(-41.25, -23.86) * mm});
            skLineSegment(sketch, "E1314", {"start": v(-41.25, -23.86) * mm, "end": v(-41.6, -24.17) * mm});
            skLineSegment(sketch, "E1315", {"start": v(-41.6, -24.17) * mm, "end": v(-41.58, -24.3) * mm});
            skLineSegment(sketch, "E1316", {"start": v(-41.58, -24.3) * mm, "end": v(-41.4, -24.43) * mm});
            skLineSegment(sketch, "E1317", {"start": v(-41.4, -24.43) * mm, "end": v(-41.26, -24.66) * mm});
            skLineSegment(sketch, "E1318", {"start": v(-41.26, -24.66) * mm, "end": v(-41.54, -24.97) * mm});
            skLineSegment(sketch, "E1319", {"start": v(-41.54, -24.97) * mm, "end": v(-43.38, -26.06) * mm});
            skLineSegment(sketch, "E1320", {"start": v(-43.38, -26.06) * mm, "end": v(-44.5, -26.43) * mm});
            skLineSegment(sketch, "E1321", {"start": v(-44.5, -26.43) * mm, "end": v(-44.35, -26.6) * mm});
            skLineSegment(sketch, "E1322", {"start": v(-44.35, -26.6) * mm, "end": v(-44.56, -26.87) * mm});
            skLineSegment(sketch, "E1323", {"start": v(-44.56, -26.87) * mm, "end": v(-44.85, -26.78) * mm});
            skLineSegment(sketch, "E1324", {"start": v(-44.85, -26.78) * mm, "end": v(-45.14, -26.77) * mm});
            skLineSegment(sketch, "E1325", {"start": v(-45.14, -26.77) * mm, "end": v(-45.26, -26.94) * mm});
            skLineSegment(sketch, "E1326", {"start": v(-45.26, -26.94) * mm, "end": v(-45.34, -26.8) * mm});
            skLineSegment(sketch, "E1327", {"start": v(-45.34, -26.8) * mm, "end": v(-46.02, -27.02) * mm});
            skLineSegment(sketch, "E1328", {"start": v(-46.02, -27.02) * mm, "end": v(-46.45, -26.86) * mm});
            skLineSegment(sketch, "E1329", {"start": v(-46.45, -26.86) * mm, "end": v(-46.73, -27.08) * mm});
            skLineSegment(sketch, "E1330", {"start": v(-46.73, -27.08) * mm, "end": v(-47.11, -27.07) * mm});
            skLineSegment(sketch, "E1331", {"start": v(-47.11, -27.07) * mm, "end": v(-47.49, -27.31) * mm});
            skLineSegment(sketch, "E1332", {"start": v(-47.49, -27.31) * mm, "end": v(-48.04, -27.19) * mm});
            skLineSegment(sketch, "E1333", {"start": v(-48.04, -27.19) * mm, "end": v(-48.4, -27.33) * mm});
            skLineSegment(sketch, "E1334", {"start": v(-48.4, -27.33) * mm, "end": v(-48.63, -27.2) * mm});
            skLineSegment(sketch, "E1335", {"start": v(-48.63, -27.2) * mm, "end": v(-48.6, -26.96) * mm});
            skLineSegment(sketch, "E1336", {"start": v(-48.6, -26.96) * mm, "end": v(-48.34, -26.83) * mm});
            skLineSegment(sketch, "E1337", {"start": v(-48.34, -26.83) * mm, "end": v(-47.63, -26.92) * mm});
            skLineSegment(sketch, "E1338", {"start": v(-47.63, -26.92) * mm, "end": v(-47.32, -26.82) * mm});
            skLineSegment(sketch, "E1339", {"start": v(-47.32, -26.82) * mm, "end": v(-47.18, -26.75) * mm});
            skLineSegment(sketch, "E1340", {"start": v(-47.18, -26.75) * mm, "end": v(-46.82, -26.45) * mm});
            skLineSegment(sketch, "E1341", {"start": v(-46.82, -26.45) * mm, "end": v(-46.6, -26.41) * mm});
            skLineSegment(sketch, "E1342", {"start": v(-46.6, -26.41) * mm, "end": v(-46.3, -26.31) * mm});
            skLineSegment(sketch, "E1343", {"start": v(-46.3, -26.31) * mm, "end": v(-46.08, -26.34) * mm});
            skLineSegment(sketch, "E1344", {"start": v(-46.08, -26.34) * mm, "end": v(-45.95, -26.5) * mm});
            skLineSegment(sketch, "E1345", {"start": v(-45.95, -26.5) * mm, "end": v(-45.72, -26.49) * mm});
            skLineSegment(sketch, "E1346", {"start": v(-45.72, -26.49) * mm, "end": v(-45.42, -26.13) * mm});
            skLineSegment(sketch, "E1347", {"start": v(-45.42, -26.13) * mm, "end": v(-44.63, -25.96) * mm});
            skLineSegment(sketch, "E1348", {"start": v(-44.63, -25.96) * mm, "end": v(-44.52, -26) * mm});
            skLineSegment(sketch, "E1349", {"start": v(-44.52, -26) * mm, "end": v(-44.37, -25.6) * mm});
            skLineSegment(sketch, "E1350", {"start": v(-44.37, -25.6) * mm, "end": v(-43.88, -25.42) * mm});
            skLineSegment(sketch, "E1351", {"start": v(-43.88, -25.42) * mm, "end": v(-43.47, -24.55) * mm});
            skLineSegment(sketch, "E1352", {"start": v(-43.47, -24.55) * mm, "end": v(-43.22, -24.37) * mm});
            skLineSegment(sketch, "E1353", {"start": v(-43.22, -24.37) * mm, "end": v(-43.17, -24.03) * mm});
            skLineSegment(sketch, "E1354", {"start": v(-43.17, -24.03) * mm, "end": v(-43.62, -24.25) * mm});
            skLineSegment(sketch, "E1355", {"start": v(-43.62, -24.25) * mm, "end": v(-43.83, -24.04) * mm});
            skLineSegment(sketch, "E1356", {"start": v(-43.83, -24.04) * mm, "end": v(-43.97, -24) * mm});
            skLineSegment(sketch, "E1357", {"start": v(-43.97, -24) * mm, "end": v(-44.15, -24.08) * mm});
            skLineSegment(sketch, "E1358", {"start": v(-44.15, -24.08) * mm, "end": v(-44.17, -24.38) * mm});
            skLineSegment(sketch, "E1359", {"start": v(-44.17, -24.38) * mm, "end": v(-44.28, -24.38) * mm});
            skLineSegment(sketch, "E1360", {"start": v(-44.28, -24.38) * mm, "end": v(-44.4, -23.72) * mm});
            skLineSegment(sketch, "E1361", {"start": v(-44.4, -23.72) * mm, "end": v(-44.55, -23.84) * mm});
            skLineSegment(sketch, "E1362", {"start": v(-44.55, -23.84) * mm, "end": v(-44.66, -23.86) * mm});
            skLineSegment(sketch, "E1363", {"start": v(-44.66, -23.86) * mm, "end": v(-44.7, -23.64) * mm});
            skLineSegment(sketch, "E1364", {"start": v(-44.7, -23.64) * mm, "end": v(-45.17, -23.66) * mm});
            skLineSegment(sketch, "E1365", {"start": v(-45.17, -23.66) * mm, "end": v(-45.45, -23.78) * mm});
            skLineSegment(sketch, "E1366", {"start": v(-45.45, -23.78) * mm, "end": v(-45.74, -23.74) * mm});
            skLineSegment(sketch, "E1367", {"start": v(-45.74, -23.74) * mm, "end": v(-45.52, -23.48) * mm});
            skLineSegment(sketch, "E1368", {"start": v(-45.52, -23.48) * mm, "end": v(-45.55, -23.05) * mm});
            skLineSegment(sketch, "E1369", {"start": v(-45.55, -23.05) * mm, "end": v(-45.2, -22.98) * mm});
            skLineSegment(sketch, "E1370", {"start": v(-45.2, -22.98) * mm, "end": v(-45.34, -22.81) * mm});
            skLineSegment(sketch, "E1371", {"start": v(-45.34, -22.81) * mm, "end": v(-45.28, -22.3) * mm});
            skLineSegment(sketch, "E1372", {"start": v(-45.28, -22.3) * mm, "end": v(-45.48, -22.13) * mm});
            skLineSegment(sketch, "E1373", {"start": v(-45.48, -22.13) * mm, "end": v(-45.58, -22.32) * mm});
            skLineSegment(sketch, "E1374", {"start": v(-45.58, -22.32) * mm, "end": v(-46.2, -22.3) * mm});
            skLineSegment(sketch, "E1375", {"start": v(-46.2, -22.3) * mm, "end": v(-46.37, -22.16) * mm});
            skLineSegment(sketch, "E1376", {"start": v(-46.37, -22.16) * mm, "end": v(-46.44, -21.79) * mm});
            skLineSegment(sketch, "E1377", {"start": v(-46.44, -21.79) * mm, "end": v(-46.62, -21.4) * mm});
            skLineSegment(sketch, "E1378", {"start": v(-46.62, -21.4) * mm, "end": v(-46.66, -21.2) * mm});
            skLineSegment(sketch, "E1379", {"start": v(-46.66, -21.2) * mm, "end": v(-46.43, -21.14) * mm});
            skLineSegment(sketch, "E1380", {"start": v(-46.43, -21.14) * mm, "end": v(-46.44, -20.93) * mm});
            skLineSegment(sketch, "E1381", {"start": v(-46.44, -20.93) * mm, "end": v(-46.27, -20.82) * mm});
            skLineSegment(sketch, "E1382", {"start": v(-46.27, -20.82) * mm, "end": v(-46.37, -20.76) * mm});
            skLineSegment(sketch, "E1383", {"start": v(-46.37, -20.76) * mm, "end": v(-46.5, -20.79) * mm});
            skLineSegment(sketch, "E1384", {"start": v(-46.5, -20.79) * mm, "end": v(-46.64, -20.5) * mm});
            skLineSegment(sketch, "E1385", {"start": v(-46.64, -20.5) * mm, "end": v(-46.57, -19.9) * mm});
            skLineSegment(sketch, "E1386", {"start": v(-46.57, -19.9) * mm, "end": v(-45.77, -19.4) * mm});
            skLineSegment(sketch, "E1387", {"start": v(-45.77, -19.4) * mm, "end": v(-45.55, -19) * mm});
            skLineSegment(sketch, "E1388", {"start": v(-45.55, -19) * mm, "end": v(-45.26, -18.84) * mm});
            skLineSegment(sketch, "E1389", {"start": v(-45.26, -18.84) * mm, "end": v(-45, -18.9) * mm});
            skLineSegment(sketch, "E1390", {"start": v(-45, -18.9) * mm, "end": v(-44.92, -19.24) * mm});
            skLineSegment(sketch, "E1391", {"start": v(-44.92, -19.24) * mm, "end": v(-44.6, -19.18) * mm});
            skLineSegment(sketch, "E1392", {"start": v(-44.6, -19.18) * mm, "end": v(-44.27, -18.98) * mm});
            skLineSegment(sketch, "E1393", {"start": v(-44.27, -18.98) * mm, "end": v(-44, -19.12) * mm});
            skLineSegment(sketch, "E1394", {"start": v(-44, -19.12) * mm, "end": v(-43.84, -19.12) * mm});
            skLineSegment(sketch, "E1395", {"start": v(-43.84, -19.12) * mm, "end": v(-43.57, -18.9) * mm});
            skLineSegment(sketch, "E1396", {"start": v(-26.02, -21.18) * mm, "end": v(-26.22, -21.48) * mm});
            skLineSegment(sketch, "E1397", {"start": v(-26.22, -21.48) * mm, "end": v(-26.55, -21.5) * mm});
            skLineSegment(sketch, "E1398", {"start": v(-26.55, -21.5) * mm, "end": v(-26.36, -21.12) * mm});
            skLineSegment(sketch, "E1399", {"start": v(-26.36, -21.12) * mm, "end": v(-26.11, -21.07) * mm});
            skLineSegment(sketch, "E1400", {"start": v(-26.11, -21.07) * mm, "end": v(-26.02, -21.18) * mm});
            skLineSegment(sketch, "E1401", {"start": v(-24.78, -21.37) * mm, "end": v(-25.39, -21.07) * mm});
            skLineSegment(sketch, "E1402", {"start": v(-25.39, -21.07) * mm, "end": v(-25.35, -20.65) * mm});
            skLineSegment(sketch, "E1403", {"start": v(-25.35, -20.65) * mm, "end": v(-24.86, -20.46) * mm});
            skLineSegment(sketch, "E1404", {"start": v(-24.86, -20.46) * mm, "end": v(-24.4, -20.53) * mm});
            skLineSegment(sketch, "E1405", {"start": v(-24.4, -20.53) * mm, "end": v(-24.37, -20.92) * mm});
            skLineSegment(sketch, "E1406", {"start": v(-24.37, -20.92) * mm, "end": v(-24.46, -21.34) * mm});
            skLineSegment(sketch, "E1407", {"start": v(-24.46, -21.34) * mm, "end": v(-24.78, -21.37) * mm});
            skLineSegment(sketch, "E1408", {"start": v(-20.55, -22.66) * mm, "end": v(-20.86, -22.51) * mm});
            skLineSegment(sketch, "E1409", {"start": v(-20.86, -22.51) * mm, "end": v(-21.29, -21.68) * mm});
            skLineSegment(sketch, "E1410", {"start": v(-21.29, -21.68) * mm, "end": v(-21.98, -22) * mm});
            skLineSegment(sketch, "E1411", {"start": v(-21.98, -22) * mm, "end": v(-22.04, -22.2) * mm});
            skLineSegment(sketch, "E1412", {"start": v(-22.04, -22.2) * mm, "end": v(-21.62, -22.82) * mm});
            skLineSegment(sketch, "E1413", {"start": v(-21.62, -22.82) * mm, "end": v(-21.2, -22.73) * mm});
            skLineSegment(sketch, "E1414", {"start": v(-21.2, -22.73) * mm, "end": v(-21.06, -22.87) * mm});
            skLineSegment(sketch, "E1415", {"start": v(-21.06, -22.87) * mm, "end": v(-20.64, -22.86) * mm});
            skLineSegment(sketch, "E1416", {"start": v(-20.64, -22.86) * mm, "end": v(-20.55, -22.66) * mm});
            skLineSegment(sketch, "E1417", {"start": v(-19.66, -22.97) * mm, "end": v(-19.8, -23.18) * mm});
            skLineSegment(sketch, "E1418", {"start": v(-19.8, -23.18) * mm, "end": v(-19.36, -23.34) * mm});
            skLineSegment(sketch, "E1419", {"start": v(-19.36, -23.34) * mm, "end": v(-18.7, -23.42) * mm});
            skLineSegment(sketch, "E1420", {"start": v(-18.7, -23.42) * mm, "end": v(-18.41, -23.25) * mm});
            skLineSegment(sketch, "E1421", {"start": v(-18.41, -23.25) * mm, "end": v(-18.41, -23.07) * mm});
            skLineSegment(sketch, "E1422", {"start": v(-18.41, -23.07) * mm, "end": v(-19.1, -23.06) * mm});
            skLineSegment(sketch, "E1423", {"start": v(-19.1, -23.06) * mm, "end": v(-19.16, -23.15) * mm});
            skLineSegment(sketch, "E1424", {"start": v(-19.16, -23.15) * mm, "end": v(-19.4, -23) * mm});
            skLineSegment(sketch, "E1425", {"start": v(-19.4, -23) * mm, "end": v(-19.66, -22.97) * mm});
            skLineSegment(sketch, "E1426", {"start": v(-18.75, -23.65) * mm, "end": v(-18.63, -23.8) * mm});
            skLineSegment(sketch, "E1427", {"start": v(-18.63, -23.8) * mm, "end": v(-18.62, -24.02) * mm});
            skLineSegment(sketch, "E1428", {"start": v(-18.62, -24.02) * mm, "end": v(-19.02, -24.2) * mm});
            skLineSegment(sketch, "E1429", {"start": v(-19.02, -24.2) * mm, "end": v(-19.22, -23.7) * mm});
            skLineSegment(sketch, "E1430", {"start": v(-19.22, -23.7) * mm, "end": v(-18.75, -23.65) * mm});
            skLineSegment(sketch, "E1431", {"start": v(-18.45, -23.62) * mm, "end": v(-18.17, -23.28) * mm});
            skLineSegment(sketch, "E1432", {"start": v(-18.17, -23.28) * mm, "end": v(-17.68, -23.56) * mm});
            skLineSegment(sketch, "E1433", {"start": v(-17.68, -23.56) * mm, "end": v(-17.27, -23.67) * mm});
            skLineSegment(sketch, "E1434", {"start": v(-17.27, -23.67) * mm, "end": v(-16.7, -23.98) * mm});
            skLineSegment(sketch, "E1435", {"start": v(-16.7, -23.98) * mm, "end": v(-16.7, -24.18) * mm});
            skLineSegment(sketch, "E1436", {"start": v(-16.7, -24.18) * mm, "end": v(-17.6, -24.53) * mm});
            skLineSegment(sketch, "E1437", {"start": v(-17.6, -24.53) * mm, "end": v(-17.86, -24.38) * mm});
            skLineSegment(sketch, "E1438", {"start": v(-17.86, -24.38) * mm, "end": v(-18.45, -23.62) * mm});
            skLineSegment(sketch, "E1439", {"start": v(-15.06, -27.62) * mm, "end": v(-14.96, -27.7) * mm});
            skLineSegment(sketch, "E1440", {"start": v(-14.96, -27.7) * mm, "end": v(-14.46, -27.58) * mm});
            skLineSegment(sketch, "E1441", {"start": v(-14.46, -27.58) * mm, "end": v(-13.96, -27.13) * mm});
            skLineSegment(sketch, "E1442", {"start": v(-13.96, -27.13) * mm, "end": v(-14.48, -26.77) * mm});
            skLineSegment(sketch, "E1443", {"start": v(-14.48, -26.77) * mm, "end": v(-14.77, -26.07) * mm});
            skLineSegment(sketch, "E1444", {"start": v(-14.77, -26.07) * mm, "end": v(-16.4, -25.25) * mm});
            skLineSegment(sketch, "E1445", {"start": v(-16.4, -25.25) * mm, "end": v(-16.6, -25.35) * mm});
            skLineSegment(sketch, "E1446", {"start": v(-16.6, -25.35) * mm, "end": v(-16.38, -25.78) * mm});
            skLineSegment(sketch, "E1447", {"start": v(-16.38, -25.78) * mm, "end": v(-16.6, -26.16) * mm});
            skLineSegment(sketch, "E1448", {"start": v(-16.6, -26.16) * mm, "end": v(-16.87, -26.25) * mm});
            skLineSegment(sketch, "E1449", {"start": v(-16.87, -26.25) * mm, "end": v(-16.95, -26.59) * mm});
            skLineSegment(sketch, "E1450", {"start": v(-16.95, -26.59) * mm, "end": v(-16.68, -26.8) * mm});
            skLineSegment(sketch, "E1451", {"start": v(-16.68, -26.8) * mm, "end": v(-16.5, -27.47) * mm});
            skLineSegment(sketch, "E1452", {"start": v(-16.5, -27.47) * mm, "end": v(-16.55, -28.2) * mm});
            skLineSegment(sketch, "E1453", {"start": v(-16.55, -28.2) * mm, "end": v(-16.04, -28.55) * mm});
            skLineSegment(sketch, "E1454", {"start": v(-16.04, -28.55) * mm, "end": v(-15.4, -27.83) * mm});
            skLineSegment(sketch, "E1455", {"start": v(-15.4, -27.83) * mm, "end": v(-15.06, -27.62) * mm});
            skLineSegment(sketch, "E1456", {"start": v(26.15, -3.3) * mm, "end": v(26.15, -3.3) * mm});
            skLineSegment(sketch, "E1457", {"start": v(-10.83, 0.24) * mm, "end": v(-10.37, 7.64) * mm});
            skLineSegment(sketch, "E1458", {"start": v(-12.62, 0.37) * mm, "end": v(-10.83, 0.24) * mm});
            skLineSegment(sketch, "E1459", {"start": v(-10.83, 0.24) * mm, "end": v(0.07, -0.1) * mm});
            skLineSegment(sketch, "E1460", {"start": v(0.07, -0.1) * mm, "end": v(3.4, -0.12) * mm});
            skLineSegment(sketch, "E1461", {"start": v(-22.96, 11.38) * mm, "end": v(-17.89, 10.74) * mm});
            skLineSegment(sketch, "E1462", {"start": v(-17.89, 10.74) * mm, "end": v(-13.86, 10.37) * mm});
            skLineSegment(sketch, "E1463", {"start": v(-13.86, 10.37) * mm, "end": v(-10.22, 10.07) * mm});
            skLineSegment(sketch, "E1464", {"start": v(-13.46, 15.24) * mm, "end": v(-13.86, 10.37) * mm});
            skLineSegment(sketch, "E1465", {"start": v(-13.46, 15.24) * mm, "end": v(-13.08, 20.1) * mm});
            skLineSegment(sketch, "E1466", {"start": v(-30.53, -28.2) * mm, "end": v(-30.61, -28.57) * mm});
            skLineSegment(sketch, "E1467", {"start": v(-24.2, 1.61) * mm, "end": v(-12.62, 0.37) * mm});
            skLineSegment(sketch, "E1468", {"start": v(-33.75, 3.22) * mm, "end": v(-24.2, 1.61) * mm});
            skLineSegment(sketch, "E1469", {"start": v(-24.2, 1.61) * mm, "end": v(-26.15, -12.1) * mm});
            skSolve(sketch);
        }
        {
            var Q0;
            Q0=makeQuery(id+"F2.imprint","IMPRINT",FACE,{"disambiguationData":[TD([[makeQuery(id+"F2.imprint","IMPRINT",EDGE,{"derivedFrom":sQuery(id+"F2.wireOp",EDGE,"E11")}),1.0]])]});
            extrude(context, id + "F3", {"entities" : qUnion([Q0]), "operationType" : NewBodyOperationType.ADD, "depth" : 4.23 * mm, "offsetDistance" : 25.4 * mm});
        }
        {
            var Q0;
            {var subQ0=sQuery(id+"F2.wireOp",EDGE,"E18");Q0=makeQuery(id+"F2.imprint","IMPRINT",FACE,{"disambiguationData":[TD([[makeQuery(id+"F2.imprint","IMPRINT",EDGE,{"derivedFrom":subQ0}),1.0]])]});}
            extrude(context, id + "F4", {"entities" : qUnion([Q0]), "operationType" : NewBodyOperationType.ADD, "depth" : 30.8 * mm, "offsetDistance" : 25.4 * mm});
        }
        {
            var Q0;
            Q0=makeQuery(id+"F2.imprint","IMPRINT",FACE,{"disambiguationData":[TD([[makeQuery(id+"F2.imprint","IMPRINT",EDGE,{"derivedFrom":sQuery(id+"F2.wireOp",EDGE,"E1")}),-1.0]])]});
            extrude(context, id + "F5", {"entities" : qUnion([Q0]), "operationType" : NewBodyOperationType.ADD, "depth" : 21.25 * mm, "offsetDistance" : 25.4 * mm});
        }
        {
            var Q0;
            Q0=makeQuery(id+"F2.imprint","IMPRINT",FACE,{"disambiguationData":[TD([[makeQuery(id+"F2.imprint","IMPRINT",EDGE,{"derivedFrom":sQuery(id+"F2.wireOp",EDGE,"E44")}),1.0]])]});
            extrude(context, id + "F6", {"entities" : qUnion([Q0]), "operationType" : NewBodyOperationType.ADD, "depth" : 15.79 * mm, "offsetDistance" : 25.4 * mm});
        }
        {
            var Q0;
            Q0=makeQuery(id+"F2.imprint","IMPRINT",FACE,{"disambiguationData":[TD([[makeQuery(id+"F2.imprint","IMPRINT",EDGE,{"derivedFrom":sQuery(id+"F2.wireOp",EDGE,"E317")}),1.0]])]});
            extrude(context, id + "F7", {"entities" : qUnion([Q0]), "operationType" : NewBodyOperationType.ADD, "depth" : 15.71 * mm, "offsetDistance" : 25.4 * mm});
        }
        {
            var Q0;
            Q0=makeQuery(id+"F2.imprint","IMPRINT",FACE,{"disambiguationData":[TD([[makeQuery(id+"F2.imprint","IMPRINT",EDGE,{"derivedFrom":sQuery(id+"F2.wireOp",EDGE,"E40")}),-1.0]])]});
            extrude(context, id + "F8", {"entities" : qUnion([Q0]), "operationType" : NewBodyOperationType.ADD, "depth" : 128821350 / 8029672510.6 * mm, "offsetDistance" : 25.4 * mm});
        }
        {
            var Q0;
            Q0=makeQuery(id+"F2.imprint","IMPRINT",FACE,{"disambiguationData":[TD([[makeQuery(id+"F2.imprint","IMPRINT",EDGE,{"derivedFrom":sQuery(id+"F2.wireOp",EDGE,"E44")}),-1.0]])]});
            extrude(context, id + "F9", {"entities" : qUnion([Q0]), "operationType" : NewBodyOperationType.ADD, "depth" : 10.26 * mm, "offsetDistance" : 25.4 * mm});
        }
        {
            var Q0;
            {var subQ0=sQuery(id+"F2.wireOp",EDGE,"E43");Q0=makeQuery(id+"F2.imprint","IMPRINT",FACE,{"disambiguationData":[TD([[makeQuery(id+"F2.imprint","IMPRINT",EDGE,{"derivedFrom":subQ0}),-1.0]])]});}
            extrude(context, id + "F10", {"entities" : qUnion([Q0]), "operationType" : NewBodyOperationType.ADD, "depth" : 9.3 * mm, "offsetDistance" : 25.4 * mm});
        }
        {
            var Q0;
            {var subQ4=sQuery(id+"F2.wireOp",EDGE,"E307");Q0=makeQuery(id+"F2.imprint","IMPRINT",FACE,{"disambiguationData":[TD([[makeQuery(id+"F2.imprint","IMPRINT",EDGE,{"derivedFrom":subQ4}),1.0]])]});}
            extrude(context, id + "F11", {"entities" : qUnion([Q0]), "operationType" : NewBodyOperationType.ADD, "depth" : 8.03 * mm, "offsetDistance" : 25.4 * mm});
        }
        {
            var Q0;
            {var subQ0=sQuery(id+"F2.wireOp",EDGE,"E41");Q0=makeQuery(id+"F2.imprint","IMPRINT",FACE,{"disambiguationData":[TD([[makeQuery(id+"F2.imprint","IMPRINT",EDGE,{"derivedFrom":subQ0}),1.0]])]});}
            var Q1;
            Q1=makeQuery(id+"F2.imprint","IMPRINT",FACE,{"disambiguationData":[TD([[makeQuery(id+"F2.imprint","IMPRINT",EDGE,{"derivedFrom":sQuery(id+"F2.wireOp",EDGE,"E577")}),-1.0]])]});
            extrude(context, id + "F12", {"entities" : qUnion([Q0, Q1]), "operationType" : NewBodyOperationType.ADD, "depth" : 7.95 * mm, "offsetDistance" : 25.4 * mm});
        }
        {
            var Q0;
            {var subQ4=sQuery(id+"F2.wireOp",EDGE,"E692");Q0=makeQuery(id+"F2.imprint","IMPRINT",FACE,{"disambiguationData":[TD([[makeQuery(id+"F2.imprint","IMPRINT",EDGE,{"derivedFrom":subQ4}),-1.0]])]});}
            extrude(context, id + "F13", {"entities" : qUnion([Q0]), "operationType" : NewBodyOperationType.ADD, "depth" : 7.9 * mm, "offsetDistance" : 25.4 * mm});
        }
        {
            var Q0;
            Q0=makeQuery(id+"F2.imprint","IMPRINT",FACE,{"disambiguationData":[TD([[makeQuery(id+"F2.imprint","IMPRINT",EDGE,{"derivedFrom":sQuery(id+"F2.wireOp",EDGE,"E186")}),-1.0]])]});
            extrude(context, id + "F14", {"entities" : qUnion([Q0]), "operationType" : NewBodyOperationType.ADD, "depth" : 7.15 * mm, "offsetDistance" : 25.4 * mm});
        }
        {
            var Q0;
            {var subQ0=sQuery(id+"F2.wireOp",EDGE,"E708");Q0=makeQuery(id+"F2.imprint","IMPRINT",FACE,{"disambiguationData":[TD([[makeQuery(id+"F2.imprint","IMPRINT",EDGE,{"derivedFrom":subQ0}),-1.0]])]});}
            extrude(context, id + "F15", {"entities" : qUnion([Q0]), "operationType" : NewBodyOperationType.ADD, "depth" : 6.64 * mm, "offsetDistance" : 25.4 * mm});
        }
        {
            var Q0;
            {var subQ0=sQuery(id+"F2.wireOp",EDGE,"E49");Q0=makeQuery(id+"F2.imprint","IMPRINT",FACE,{"disambiguationData":[TD([[makeQuery(id+"F2.imprint","IMPRINT",EDGE,{"derivedFrom":subQ0}),-1.0]])]});}
            extrude(context, id + "F16", {"entities" : qUnion([Q0]), "operationType" : NewBodyOperationType.ADD, "depth" : 5.6 * mm, "offsetDistance" : 25.4 * mm});
        }
        {
            var Q0;
            {var subQ3=sQuery(id+"F2.wireOp",EDGE,"E201");Q0=makeQuery(id+"F2.imprint","IMPRINT",FACE,{"disambiguationData":[TD([[makeQuery(id+"F2.imprint","IMPRINT",EDGE,{"derivedFrom":subQ3}),-1.0]])]});}
            extrude(context, id + "F17", {"entities" : qUnion([Q0]), "operationType" : NewBodyOperationType.ADD, "depth" : 5.38 * mm, "offsetDistance" : 25.4 * mm});
        }
        {
            var Q0;
            {var subQ3=sQuery(id+"F2.wireOp",EDGE,"E41");Q0=makeQuery(id+"F2.imprint","IMPRINT",FACE,{"disambiguationData":[TD([[makeQuery(id+"F2.imprint","IMPRINT",EDGE,{"derivedFrom":subQ3}),-1.0]])]});}
            extrude(context, id + "F18", {"entities" : qUnion([Q0]), "operationType" : NewBodyOperationType.ADD, "depth" : 5.28 * mm, "offsetDistance" : 25.4 * mm});
        }
        {
            var Q0;
            Q0=makeQuery(id+"F2.imprint","IMPRINT",FACE,{"disambiguationData":[TD([[makeQuery(id+"F2.imprint","IMPRINT",EDGE,{"derivedFrom":sQuery(id+"F2.wireOp",EDGE,"E51")}),-1.0]])]});
            extrude(context, id + "F19", {"entities" : qUnion([Q0]), "operationType" : NewBodyOperationType.ADD, "depth" : 5.22 * mm, "offsetDistance" : 25.4 * mm});
        }
        {
            var Q0;
            Q0=makeQuery(id+"F2.imprint","IMPRINT",FACE,{"disambiguationData":[TD([[makeQuery(id+"F2.imprint","IMPRINT",EDGE,{"derivedFrom":sQuery(id+"F2.wireOp",EDGE,"E39")}),-1.0]])]});
            extrude(context, id + "F20", {"entities" : qUnion([Q0]), "operationType" : NewBodyOperationType.ADD, "depth" : 4.86 * mm, "offsetDistance" : 25.4 * mm});
        }
        {
            var Q0;
            {var subQ5=sQuery(id+"F2.wireOp",EDGE,"E606");Q0=makeQuery(id+"F2.imprint","IMPRINT",FACE,{"disambiguationData":[TD([[makeQuery(id+"F2.imprint","IMPRINT",EDGE,{"derivedFrom":subQ5}),-1.0]])]});}
            extrude(context, id + "F21", {"entities" : qUnion([Q0]), "operationType" : NewBodyOperationType.ADD, "depth" : 4.76 * mm, "offsetDistance" : 25.4 * mm});
        }
        {
            var Q0;
            Q0=makeQuery(id+"F2.imprint","IMPRINT",FACE,{"disambiguationData":[TD([[makeQuery(id+"F2.imprint","IMPRINT",EDGE,{"derivedFrom":sQuery(id+"F2.wireOp",EDGE,"E40")}),1.0]])]});
            extrude(context, id + "F22", {"entities" : qUnion([Q0]), "operationType" : NewBodyOperationType.ADD, "depth" : 4.61 * mm, "offsetDistance" : 25.4 * mm});
        }
        {
            var Q0;
            {var subQ1=sQuery(id+"F2.wireOp",EDGE,"E261");Q0=makeQuery(id+"F2.imprint","IMPRINT",FACE,{"disambiguationData":[TD([[makeQuery(id+"F2.imprint","IMPRINT",EDGE,{"derivedFrom":subQ1}),-1.0]])]});}
            extrude(context, id + "F23", {"entities" : qUnion([Q0]), "operationType" : NewBodyOperationType.ADD, "depth" : 4.36 * mm, "offsetDistance" : 25.4 * mm});
        }
        {
            var Q0;
            {var subQ0=sQuery(id+"F2.wireOp",EDGE,"E307");Q0=makeQuery(id+"F2.imprint","IMPRINT",FACE,{"disambiguationData":[TD([[makeQuery(id+"F2.imprint","IMPRINT",EDGE,{"derivedFrom":subQ0}),-1.0]])]});}
            extrude(context, id + "F24", {"entities" : qUnion([Q0]), "operationType" : NewBodyOperationType.ADD, "depth" : 3.88 * mm, "offsetDistance" : 25.4 * mm});
        }
        {
            var Q0;
            Q0=makeQuery(id+"F2.imprint","IMPRINT",FACE,{"disambiguationData":[TD([[makeQuery(id+"F2.imprint","IMPRINT",EDGE,{"derivedFrom":sQuery(id+"F2.wireOp",EDGE,"E1076")}),-1.0]])]});
            extrude(context, id + "F25", {"entities" : qUnion([Q0]), "operationType" : NewBodyOperationType.ADD, "depth" : 3.84 * mm, "offsetDistance" : 25.4 * mm});
        }
        {
            var Q0;
            Q0=makeQuery(id+"F2.imprint","IMPRINT",FACE,{"disambiguationData":[TD([[makeQuery(id+"F2.imprint","IMPRINT",EDGE,{"derivedFrom":sQuery(id+"F2.wireOp",EDGE,"E54")}),-1.0]])]});
            extrude(context, id + "F26", {"entities" : qUnion([Q0]), "operationType" : NewBodyOperationType.ADD, "depth" : 3.72 * mm, "offsetDistance" : 25.4 * mm});
        }
        {
            var Q0;
            Q0=makeQuery(id+"F2.imprint","IMPRINT",FACE,{"disambiguationData":[TD([[makeQuery(id+"F2.imprint","IMPRINT",EDGE,{"derivedFrom":sQuery(id+"F2.wireOp",EDGE,"E51")}),1.0]])]});
            extrude(context, id + "F27", {"entities" : qUnion([Q0]), "operationType" : NewBodyOperationType.ADD, "depth" : 3.53 * mm, "offsetDistance" : 25.4 * mm});
        }
        {
            var Q0;
            {var subQ2=sQuery(id+"F2.wireOp",EDGE,"E122");Q0=makeQuery(id+"F2.imprint","IMPRINT",FACE,{"disambiguationData":[TD([[makeQuery(id+"F2.imprint","IMPRINT",EDGE,{"derivedFrom":subQ2}),1.0]])]});}
            extrude(context, id + "F28", {"entities" : qUnion([Q0]), "operationType" : NewBodyOperationType.ADD, "depth" : 3.16 * mm, "offsetDistance" : 25.4 * mm});
        }
        {
            var Q0;
            Q0=makeQuery(id+"F2.imprint","IMPRINT",FACE,{"disambiguationData":[TD([[makeQuery(id+"F2.imprint","IMPRINT",EDGE,{"derivedFrom":sQuery(id+"F2.wireOp",EDGE,"E24")}),-1.0]])]});
            extrude(context, id + "F29", {"entities" : qUnion([Q0]), "operationType" : NewBodyOperationType.ADD, "depth" : 3.1 * mm, "offsetDistance" : 25.4 * mm});
        }
        {
            var Q0;
            Q0=makeQuery(id+"F2.imprint","IMPRINT",FACE,{"disambiguationData":[TD([[makeQuery(id+"F2.imprint","IMPRINT",EDGE,{"derivedFrom":sQuery(id+"F2.wireOp",EDGE,"E197")}),-1.0]])]});
            extrude(context, id + "F30", {"entities" : qUnion([Q0]), "operationType" : NewBodyOperationType.ADD, "depth" : 2.9 * mm, "offsetDistance" : 25.4 * mm});
        }
        {
            var Q0;
            Q0=makeQuery(id+"F2.imprint","IMPRINT",FACE,{"disambiguationData":[TD([[makeQuery(id+"F2.imprint","IMPRINT",EDGE,{"derivedFrom":sQuery(id+"F2.wireOp",EDGE,"E39")}),1.0]])]});
            extrude(context, id + "F31", {"entities" : qUnion([Q0]), "operationType" : NewBodyOperationType.ADD, "depth" : 2.48 * mm, "offsetDistance" : 25.4 * mm});
        }
        {
            var Q0;
            {var subQ0=sQuery(id+"F2.wireOp",EDGE,"E308");Q0=makeQuery(id+"F2.imprint","IMPRINT",FACE,{"disambiguationData":[TD([[makeQuery(id+"F2.imprint","IMPRINT",EDGE,{"derivedFrom":subQ0}),-1.0]])]});}
            extrude(context, id + "F32", {"entities" : qUnion([Q0]), "operationType" : NewBodyOperationType.ADD, "depth" : 2.4 * mm, "offsetDistance" : 25.4 * mm});
        }
        {
            var Q0;
            Q0=makeQuery(id+"F2.imprint","IMPRINT",FACE,{"disambiguationData":[TD([[makeQuery(id+"F2.imprint","IMPRINT",EDGE,{"derivedFrom":sQuery(id+"F2.wireOp",EDGE,"E47")}),-1.0]])]});
            extrude(context, id + "F33", {"entities" : qUnion([Q0]), "operationType" : NewBodyOperationType.ADD, "depth" : 2.38 * mm, "offsetDistance" : 25.4 * mm});
        }
        {
            var Q0;
            Q0=makeQuery(id+"F2.imprint","IMPRINT",FACE,{"disambiguationData":[TD([[makeQuery(id+"F2.imprint","IMPRINT",EDGE,{"derivedFrom":sQuery(id+"F2.wireOp",EDGE,"E11")}),-1.0]])]});
            extrude(context, id + "F34", {"entities" : qUnion([Q0]), "operationType" : NewBodyOperationType.ADD, "depth" : 2.33 * mm, "offsetDistance" : 25.4 * mm});
        }
        {
            var Q0;
            Q0=makeQuery(id+"F2.imprint","IMPRINT",FACE,{"disambiguationData":[TD([[makeQuery(id+"F2.imprint","IMPRINT",EDGE,{"derivedFrom":sQuery(id+"F2.wireOp",EDGE,"E37")}),-1.0]])]});
            extrude(context, id + "F35", {"entities" : qUnion([Q0]), "operationType" : NewBodyOperationType.ADD, "depth" : 2.33 * mm, "offsetDistance" : 25.4 * mm});
        }
        {
            var Q0;
            {var subQ0=sQuery(id+"F2.wireOp",EDGE,"E16");Q0=makeQuery(id+"F2.imprint","IMPRINT",FACE,{"disambiguationData":[TD([[makeQuery(id+"F2.imprint","IMPRINT",EDGE,{"derivedFrom":subQ0}),1.0]])]});}
            extrude(context, id + "F36", {"entities" : qUnion([Q0]), "operationType" : NewBodyOperationType.ADD, "depth" : 2.24 * mm, "offsetDistance" : 25.4 * mm});
        }
        {
            var Q0;
            Q0=makeQuery(id+"F2.imprint","IMPRINT",FACE,{"disambiguationData":[TD([[makeQuery(id+"F2.imprint","IMPRINT",EDGE,{"derivedFrom":sQuery(id+"F2.wireOp",EDGE,"E12")}),1.0]])]});
            extrude(context, id + "F37", {"entities" : qUnion([Q0]), "operationType" : NewBodyOperationType.ADD, "depth" : 1.5 * mm, "offsetDistance" : 25.4 * mm});
        }
        {
            var Q0;
            Q0=makeQuery(id+"F2.imprint","IMPRINT",FACE,{"disambiguationData":[TD([[makeQuery(id+"F2.imprint","IMPRINT",EDGE,{"derivedFrom":sQuery(id+"F2.wireOp",EDGE,"E711")}),-1.0]])]});
            extrude(context, id + "F38", {"entities" : qUnion([Q0]), "operationType" : NewBodyOperationType.ADD, "depth" : 1.49 * mm, "offsetDistance" : 25.4 * mm});
        }
        {
            var Q0;
            {var subQ2=sQuery(id+"F2.wireOp",EDGE,"E13");Q0=makeQuery(id+"F2.imprint","IMPRINT",FACE,{"disambiguationData":[TD([[makeQuery(id+"F2.imprint","IMPRINT",EDGE,{"derivedFrom":subQ2}),1.0]])]});}
            extrude(context, id + "F39", {"entities" : qUnion([Q0]), "operationType" : NewBodyOperationType.ADD, "depth" : 1.3 * mm, "offsetDistance" : 25.4 * mm});
        }
        {
            var Q0;
            Q0=makeQuery(id+"F2.imprint","IMPRINT",FACE,{"disambiguationData":[TD([[makeQuery(id+"F2.imprint","IMPRINT",EDGE,{"derivedFrom":sQuery(id+"F2.wireOp",EDGE,"E1431")}),-1.0]])]});
            var Q1;
            Q1=makeQuery(id+"F2.imprint","IMPRINT",FACE,{"disambiguationData":[TD([[makeQuery(id+"F2.imprint","IMPRINT",EDGE,{"derivedFrom":sQuery(id+"F2.wireOp",EDGE,"E1439")}),1.0]])]});
            var Q2;
            Q2=makeQuery(id+"F2.imprint","IMPRINT",FACE,{"disambiguationData":[TD([[makeQuery(id+"F2.imprint","IMPRINT",EDGE,{"derivedFrom":sQuery(id+"F2.wireOp",EDGE,"E1408")}),1.0]])]});
            var Q3;
            Q3=makeQuery(id+"F2.imprint","IMPRINT",FACE,{"disambiguationData":[TD([[makeQuery(id+"F2.imprint","IMPRINT",EDGE,{"derivedFrom":sQuery(id+"F2.wireOp",EDGE,"E1401")}),-1.0]])]});
            var Q4;
            Q4=makeQuery(id+"F2.imprint","IMPRINT",FACE,{"disambiguationData":[TD([[makeQuery(id+"F2.imprint","IMPRINT",EDGE,{"derivedFrom":sQuery(id+"F2.wireOp",EDGE,"E1417")}),1.0]])]});
            var Q5;
            Q5=makeQuery(id+"F2.imprint","IMPRINT",FACE,{"disambiguationData":[TD([[makeQuery(id+"F2.imprint","IMPRINT",EDGE,{"derivedFrom":sQuery(id+"F2.wireOp",EDGE,"E1426")}),-1.0]])]});
            var Q6;
            Q6=makeQuery(id+"F2.imprint","IMPRINT",FACE,{"disambiguationData":[TD([[makeQuery(id+"F2.imprint","IMPRINT",EDGE,{"derivedFrom":sQuery(id+"F2.wireOp",EDGE,"E1396")}),-1.0]])]});
            extrude(context, id + "F40", {"entities" : qUnion([Q0, Q1, Q2, Q3, Q4, Q5, Q6]), "operationType" : NewBodyOperationType.ADD, "depth" : 1.13 * mm, "offsetDistance" : 25.4 * mm});
        }
        {
            var Q0;
            Q0=makeQuery(id+"F2.imprint","IMPRINT",FACE,{"disambiguationData":[TD([[makeQuery(id+"F2.imprint","IMPRINT",EDGE,{"derivedFrom":sQuery(id+"F2.wireOp",EDGE,"E854")}),-1.0]])]});
            extrude(context, id + "F41", {"entities" : qUnion([Q0]), "operationType" : NewBodyOperationType.ADD, "depth" : 1.07 * mm, "offsetDistance" : 25.4 * mm});
        }
        {
            var Q0;
            {var subQ1=sQuery(id+"F2.wireOp",EDGE,"E621");Q0=makeQuery(id+"F2.imprint","IMPRINT",FACE,{"disambiguationData":[TD([[makeQuery(id+"F2.imprint","IMPRINT",EDGE,{"derivedFrom":subQ1}),1.0]])]});}
            extrude(context, id + "F42", {"entities" : qUnion([Q0]), "operationType" : NewBodyOperationType.ADD, "depth" : 1.06 * mm, "offsetDistance" : 25.4 * mm});
        }
        {
            var Q0;
            Q0=makeQuery(id+"F2.imprint","IMPRINT",FACE,{"disambiguationData":[TD([[makeQuery(id+"F2.imprint","IMPRINT",EDGE,{"derivedFrom":sQuery(id+"F2.wireOp",EDGE,"E608")}),-1.0]])]});
            extrude(context, id + "F43", {"entities" : qUnion([Q0]), "operationType" : NewBodyOperationType.ADD, "depth" : 0.84 * mm, "offsetDistance" : 25.4 * mm});
        }
        {
            var Q0;
            {var subQ5=sQuery(id+"F2.wireOp",EDGE,"E21");Q0=makeQuery(id+"F2.imprint","IMPRINT",FACE,{"disambiguationData":[TD([[makeQuery(id+"F2.imprint","IMPRINT",EDGE,{"derivedFrom":subQ5}),-1.0]])]});}
            extrude(context, id + "F44", {"entities" : qUnion([Q0]), "operationType" : NewBodyOperationType.ADD, "depth" : 0.82 * mm, "offsetDistance" : 25.4 * mm});
        }
        {
            var Q0;
            {var subQ3=sQuery(id+"F2.wireOp",EDGE,"E606");Q0=makeQuery(id+"F2.imprint","IMPRINT",FACE,{"disambiguationData":[TD([[makeQuery(id+"F2.imprint","IMPRINT",EDGE,{"derivedFrom":subQ3}),1.0]])]});}
            extrude(context, id + "F45", {"entities" : qUnion([Q0]), "operationType" : NewBodyOperationType.ADD, "depth" : 0.74 * mm, "offsetDistance" : 25.4 * mm});
        }
        {
            var Q0;
            Q0=makeQuery(id+"F2.imprint","IMPRINT",FACE,{"disambiguationData":[TD([[makeQuery(id+"F2.imprint","IMPRINT",EDGE,{"derivedFrom":sQuery(id+"F2.wireOp",EDGE,"E36")}),1.0]])]});
            extrude(context, id + "F46", {"entities" : qUnion([Q0]), "operationType" : NewBodyOperationType.ADD, "depth" : 0.68 * mm, "offsetDistance" : 25.4 * mm});
        }
        {
            var Q0;
            Q0=makeQuery(id+"F2.imprint","IMPRINT",FACE,{"disambiguationData":[TD([[makeQuery(id+"F2.imprint","IMPRINT",EDGE,{"derivedFrom":sQuery(id+"F2.wireOp",EDGE,"E1179")}),1.0]])]});
            extrude(context, id + "F47", {"entities" : qUnion([Q0]), "operationType" : NewBodyOperationType.ADD, "depth" : 0.6 * mm, "offsetDistance" : 25.4 * mm});
        }
        {
            var Q0;
            {var subQ4=sQuery(id+"F2.wireOp",EDGE,"E260");Q0=makeQuery(id+"F2.imprint","IMPRINT",FACE,{"disambiguationData":[TD([[makeQuery(id+"F2.imprint","IMPRINT",EDGE,{"derivedFrom":subQ4}),1.0]])]});}
            extrude(context, id + "F48", {"entities" : qUnion([Q0]), "operationType" : NewBodyOperationType.ADD, "depth" : 0.58 * mm, "offsetDistance" : 25.4 * mm});
        }
        {
            var Q0;
            {var subQ1=sQuery(id+"F2.wireOp",EDGE,"E202");Q0=makeQuery(id+"F2.imprint","IMPRINT",FACE,{"disambiguationData":[TD([[makeQuery(id+"F2.imprint","IMPRINT",EDGE,{"derivedFrom":subQ1}),-1.0]])]});}
            extrude(context, id + "F49", {"entities" : qUnion([Q0]), "operationType" : NewBodyOperationType.ADD, "depth" : 0.5 * mm, "offsetDistance" : 25.4 * mm});
        }
        {
            var Q0;
            {var subQ3=sQuery(id+"F2.wireOp",EDGE,"E14");Q0=makeQuery(id+"F2.imprint","IMPRINT",FACE,{"disambiguationData":[TD([[makeQuery(id+"F2.imprint","IMPRINT",EDGE,{"derivedFrom":subQ3}),1.0]])]});}
            extrude(context, id + "F50", {"entities" : qUnion([Q0]), "operationType" : NewBodyOperationType.ADD, "depth" : 0.47 * mm, "offsetDistance" : 25.4 * mm});
        }
        {
            var Q0;
            Q0=makeQuery(id+"F2.imprint","IMPRINT",FACE,{"disambiguationData":[TD([[makeQuery(id+"F2.imprint","IMPRINT",EDGE,{"derivedFrom":sQuery(id+"F2.wireOp",EDGE,"E22")}),1.0]])]});
            extrude(context, id + "F51", {"entities" : qUnion([Q0]), "operationType" : NewBodyOperationType.ADD, "depth" : 1.68 * mm, "offsetDistance" : 25.4 * mm});
        }
    });
